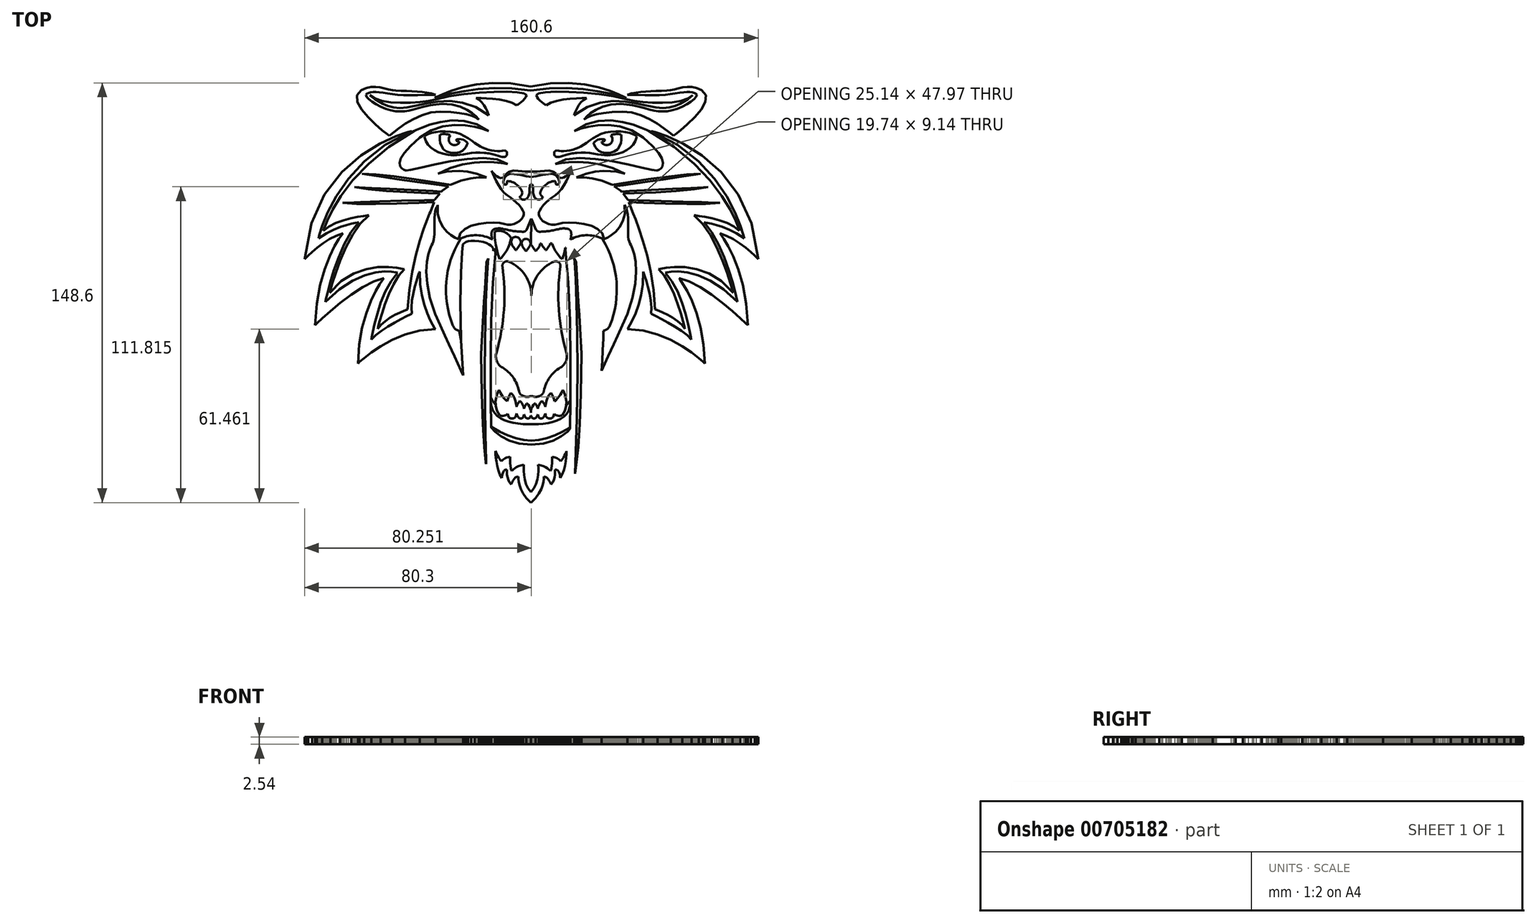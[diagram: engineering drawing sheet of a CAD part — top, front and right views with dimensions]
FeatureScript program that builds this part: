
annotation { "Feature Type Name" : "Feature", "Feature Type Description" : "" }
export const myFeature = defineFeature(function(context is Context, id is Id, definition is map)
    precondition{}
    {
        {
            var Q0;
            Q0=qCreatedBy(makeId("Top.planeOp"),FACE);
            var sketch = newSketch(context, id + "F0", { "sketchPlane" : qUnion([Q0])});
            skLineSegment(sketch, "E0", {"start": v(12.77, -75.29) * mm, "end": v(12.8, -74.69) * mm});
            skLineSegment(sketch, "E1", {"start": v(12.8, -74.69) * mm, "end": v(12.82, -74.1) * mm});
            skLineSegment(sketch, "E2", {"start": v(12.82, -74.1) * mm, "end": v(12.84, -73.5) * mm});
            skLineSegment(sketch, "E3", {"start": v(12.84, -73.5) * mm, "end": v(12.87, -72.9) * mm});
            skLineSegment(sketch, "E4", {"start": v(12.87, -72.9) * mm, "end": v(12.9, -72.3) * mm});
            skLineSegment(sketch, "E5", {"start": v(12.9, -72.3) * mm, "end": v(12.92, -71.7) * mm});
            skLineSegment(sketch, "E6", {"start": v(12.92, -71.7) * mm, "end": v(12.94, -71.1) * mm});
            skLineSegment(sketch, "E7", {"start": v(12.94, -71.1) * mm, "end": v(12.97, -70.5) * mm});
            skLineSegment(sketch, "E8", {"start": v(12.97, -70.5) * mm, "end": v(13.08, -67.74) * mm});
            skLineSegment(sketch, "E9", {"start": v(13.08, -67.74) * mm, "end": v(13.31, -60.6) * mm});
            skLineSegment(sketch, "E10", {"start": v(13.31, -60.6) * mm, "end": v(13.58, -50.1) * mm});
            skLineSegment(sketch, "E11", {"start": v(13.59, -50.63) * mm, "end": v(13.8, -37.88) * mm});
            skLineSegment(sketch, "E12", {"start": v(13.8, -37.88) * mm, "end": v(13.84, -23.18) * mm});
            skLineSegment(sketch, "E13", {"start": v(13.84, -23.18) * mm, "end": v(13.63, -8.86) * mm});
            skLineSegment(sketch, "E14", {"start": v(13.63, -8.86) * mm, "end": v(13.07, 4.68) * mm});
            skLineSegment(sketch, "E15", {"start": v(13.07, 4.68) * mm, "end": v(12.07, 16.37) * mm});
            skLineSegment(sketch, "E16", {"start": v(12.07, 16.37) * mm, "end": v(12.06, 16.4) * mm});
            skLineSegment(sketch, "E17", {"start": v(12.06, 16.4) * mm, "end": v(12.06, 16.43) * mm});
            skLineSegment(sketch, "E18", {"start": v(12.06, 16.43) * mm, "end": v(12.06, 16.46) * mm});
            skLineSegment(sketch, "E19", {"start": v(12.06, 16.46) * mm, "end": v(12.05, 16.49) * mm});
            skLineSegment(sketch, "E20", {"start": v(12.05, 16.49) * mm, "end": v(12.05, 16.52) * mm});
            skLineSegment(sketch, "E21", {"start": v(12.05, 16.52) * mm, "end": v(12.04, 16.54) * mm});
            skLineSegment(sketch, "E22", {"start": v(12.04, 16.54) * mm, "end": v(12.04, 16.57) * mm});
            skLineSegment(sketch, "E23", {"start": v(12.04, 16.57) * mm, "end": v(12.04, 16.6) * mm});
            skLineSegment(sketch, "E24", {"start": v(12.04, 16.6) * mm, "end": v(12.05, 16.63) * mm});
            skLineSegment(sketch, "E25", {"start": v(12.05, 16.63) * mm, "end": v(12.06, 16.66) * mm});
            skLineSegment(sketch, "E26", {"start": v(12.06, 16.66) * mm, "end": v(12.06, 16.69) * mm});
            skLineSegment(sketch, "E27", {"start": v(12.06, 16.69) * mm, "end": v(12.07, 16.71) * mm});
            skLineSegment(sketch, "E28", {"start": v(12.07, 16.71) * mm, "end": v(12.08, 16.74) * mm});
            skLineSegment(sketch, "E29", {"start": v(12.08, 16.74) * mm, "end": v(12.1, 16.77) * mm});
            skLineSegment(sketch, "E30", {"start": v(12.1, 16.77) * mm, "end": v(12.1, 16.8) * mm});
            skLineSegment(sketch, "E31", {"start": v(12.1, 16.8) * mm, "end": v(12.1, 16.82) * mm});
            skLineSegment(sketch, "E32", {"start": v(12.1, 16.82) * mm, "end": v(12.2, 17.03) * mm});
            skLineSegment(sketch, "E33", {"start": v(12.2, 17.03) * mm, "end": v(12.4, 17.4) * mm});
            skLineSegment(sketch, "E34", {"start": v(12.4, 17.4) * mm, "end": v(12.74, 17.88) * mm});
            skLineSegment(sketch, "E35", {"start": v(12.74, 17.88) * mm, "end": v(13.29, 18.43) * mm});
            skLineSegment(sketch, "E36", {"start": v(13.29, 18.43) * mm, "end": v(14.06, 19) * mm});
            skLineSegment(sketch, "E37", {"start": v(14.06, 19) * mm, "end": v(15.09, 19.54) * mm});
            skLineSegment(sketch, "E38", {"start": v(15.09, 19.54) * mm, "end": v(16.42, 20) * mm});
            skLineSegment(sketch, "E39", {"start": v(16.42, 20) * mm, "end": v(18.09, 20.35) * mm});
            skLineSegment(sketch, "E40", {"start": v(18.09, 20.35) * mm, "end": v(18.34, 20.38) * mm});
            skLineSegment(sketch, "E41", {"start": v(18.34, 20.38) * mm, "end": v(18.6, 20.41) * mm});
            skLineSegment(sketch, "E42", {"start": v(18.6, 20.41) * mm, "end": v(18.84, 20.44) * mm});
            skLineSegment(sketch, "E43", {"start": v(18.84, 20.44) * mm, "end": v(19.08, 20.46) * mm});
            skLineSegment(sketch, "E44", {"start": v(19.08, 20.46) * mm, "end": v(19.32, 20.47) * mm});
            skLineSegment(sketch, "E45", {"start": v(19.32, 20.47) * mm, "end": v(19.56, 20.49) * mm});
            skLineSegment(sketch, "E46", {"start": v(19.56, 20.49) * mm, "end": v(19.8, 20.5) * mm});
            skLineSegment(sketch, "E47", {"start": v(19.8, 20.5) * mm, "end": v(20.02, 20.5) * mm});
            skLineSegment(sketch, "E48", {"start": v(20.02, 20.5) * mm, "end": v(21.18, 20.43) * mm});
            skLineSegment(sketch, "E49", {"start": v(21.18, 20.43) * mm, "end": v(22.18, 20.25) * mm});
            skLineSegment(sketch, "E50", {"start": v(22.18, 20.25) * mm, "end": v(23.03, 19.98) * mm});
            skLineSegment(sketch, "E51", {"start": v(23.03, 19.98) * mm, "end": v(23.74, 19.63) * mm});
            skLineSegment(sketch, "E52", {"start": v(23.74, 19.63) * mm, "end": v(24.29, 19.24) * mm});
            skLineSegment(sketch, "E53", {"start": v(24.29, 19.24) * mm, "end": v(24.69, 18.83) * mm});
            skLineSegment(sketch, "E54", {"start": v(24.69, 18.83) * mm, "end": v(24.94, 18.42) * mm});
            skLineSegment(sketch, "E55", {"start": v(24.94, 18.42) * mm, "end": v(25.04, 18.02) * mm});
            skLineSegment(sketch, "E56", {"start": v(25.04, 18.02) * mm, "end": v(25.1, 17.3) * mm});
            skLineSegment(sketch, "E57", {"start": v(25.1, 17.3) * mm, "end": v(25.24, 15.31) * mm});
            skLineSegment(sketch, "E58", {"start": v(25.24, 15.31) * mm, "end": v(25.42, 12.2) * mm});
            skLineSegment(sketch, "E59", {"start": v(25.42, 12.2) * mm, "end": v(25.6, 8.12) * mm});
            skLineSegment(sketch, "E60", {"start": v(25.6, 8.12) * mm, "end": v(25.76, 3.17) * mm});
            skLineSegment(sketch, "E61", {"start": v(25.51, 3.31) * mm, "end": v(25.6, -2.35) * mm});
            skLineSegment(sketch, "E62", {"start": v(25.6, -2.35) * mm, "end": v(25.6, -8.6) * mm});
            skLineSegment(sketch, "E63", {"start": v(25.6, -8.6) * mm, "end": v(25.45, -15.3) * mm});
            skLineSegment(sketch, "E64", {"start": v(25.45, -15.3) * mm, "end": v(25.3, -19.29) * mm});
            skLineSegment(sketch, "E65", {"start": v(25.3, -19.29) * mm, "end": v(25.08, -23.2) * mm});
            skLineSegment(sketch, "E66", {"start": v(25.08, -23.2) * mm, "end": v(24.81, -27) * mm});
            skLineSegment(sketch, "E67", {"start": v(25.06, -27.14) * mm, "end": v(24.74, -30.85) * mm});
            skLineSegment(sketch, "E68", {"start": v(24.74, -30.85) * mm, "end": v(24.37, -34.46) * mm});
            skLineSegment(sketch, "E69", {"start": v(24.37, -34.46) * mm, "end": v(23.95, -37.96) * mm});
            skLineSegment(sketch, "E70", {"start": v(23.95, -37.96) * mm, "end": v(23.48, -41.35) * mm});
            skLineSegment(sketch, "E71", {"start": v(23.48, -41.35) * mm, "end": v(22.96, -44.63) * mm});
            skLineSegment(sketch, "E72", {"start": v(22.96, -44.63) * mm, "end": v(22.24, -48.58) * mm});
            skLineSegment(sketch, "E73", {"start": v(22.24, -48.58) * mm, "end": v(21.43, -52.36) * mm});
            skLineSegment(sketch, "E74", {"start": v(21.43, -52.36) * mm, "end": v(20.54, -55.95) * mm});
            skLineSegment(sketch, "E75", {"start": v(20.54, -55.95) * mm, "end": v(19.58, -59.35) * mm});
            skLineSegment(sketch, "E76", {"start": v(19.58, -59.35) * mm, "end": v(18.54, -62.56) * mm});
            skLineSegment(sketch, "E77", {"start": v(18.54, -62.56) * mm, "end": v(17.42, -65.58) * mm});
            skLineSegment(sketch, "E78", {"start": v(17.42, -65.58) * mm, "end": v(16.23, -68.4) * mm});
            skLineSegment(sketch, "E79", {"start": v(16.23, -68.4) * mm, "end": v(14.96, -71.03) * mm});
            skLineSegment(sketch, "E80", {"start": v(14.96, -71.03) * mm, "end": v(14.69, -71.56) * mm});
            skLineSegment(sketch, "E81", {"start": v(14.69, -71.56) * mm, "end": v(14.41, -72.1) * mm});
            skLineSegment(sketch, "E82", {"start": v(14.41, -72.1) * mm, "end": v(14.14, -72.63) * mm});
            skLineSegment(sketch, "E83", {"start": v(14.14, -72.63) * mm, "end": v(13.87, -73.16) * mm});
            skLineSegment(sketch, "E84", {"start": v(13.87, -73.16) * mm, "end": v(13.6, -73.7) * mm});
            skLineSegment(sketch, "E85", {"start": v(13.6, -73.7) * mm, "end": v(13.32, -74.22) * mm});
            skLineSegment(sketch, "E86", {"start": v(13.32, -74.22) * mm, "end": v(13.04, -74.76) * mm});
            skLineSegment(sketch, "E87", {"start": v(13.04, -74.76) * mm, "end": v(12.77, -75.29) * mm});
            skLineSegment(sketch, "E88", {"start": v(14.2, 16.3) * mm, "end": v(15.05, 6.8) * mm});
            skLineSegment(sketch, "E89", {"start": v(15.05, 6.8) * mm, "end": v(15.6, -4.05) * mm});
            skLineSegment(sketch, "E90", {"start": v(15.6, -4.05) * mm, "end": v(15.88, -15.66) * mm});
            skLineSegment(sketch, "E91", {"start": v(15.88, -15.66) * mm, "end": v(15.96, -27.46) * mm});
            skLineSegment(sketch, "E92", {"start": v(15.96, -27.46) * mm, "end": v(15.88, -38.9) * mm});
            skLineSegment(sketch, "E93", {"start": v(15.88, -38.9) * mm, "end": v(15.71, -49.38) * mm});
            skLineSegment(sketch, "E94", {"start": v(15.71, -49.38) * mm, "end": v(15.5, -58.35) * mm});
            skLineSegment(sketch, "E95", {"start": v(15.5, -58.35) * mm, "end": v(15.28, -65.25) * mm});
            skLineSegment(sketch, "E96", {"start": v(15.28, -65.25) * mm, "end": v(16.97, -60.57) * mm});
            skLineSegment(sketch, "E97", {"start": v(16.97, -60.57) * mm, "end": v(18.48, -55.42) * mm});
            skLineSegment(sketch, "E98", {"start": v(18.48, -55.42) * mm, "end": v(19.81, -49.8) * mm});
            skLineSegment(sketch, "E99", {"start": v(19.81, -49.8) * mm, "end": v(20.95, -43.74) * mm});
            skLineSegment(sketch, "E100", {"start": v(20.95, -43.74) * mm, "end": v(21.9, -37.25) * mm});
            skLineSegment(sketch, "E101", {"start": v(21.9, -37.25) * mm, "end": v(22.66, -30.35) * mm});
            skLineSegment(sketch, "E102", {"start": v(22.66, -30.35) * mm, "end": v(23.22, -23.04) * mm});
            skLineSegment(sketch, "E103", {"start": v(23.22, -23.04) * mm, "end": v(23.58, -15.36) * mm});
            skLineSegment(sketch, "E104", {"start": v(23.58, -15.36) * mm, "end": v(23.73, -9.17) * mm});
            skLineSegment(sketch, "E105", {"start": v(23.73, -9.17) * mm, "end": v(23.75, -3.37) * mm});
            skLineSegment(sketch, "E106", {"start": v(23.75, -3.37) * mm, "end": v(23.68, 1.96) * mm});
            skLineSegment(sketch, "E107", {"start": v(23.68, 1.96) * mm, "end": v(23.54, 6.7) * mm});
            skLineSegment(sketch, "E108", {"start": v(23.54, 6.7) * mm, "end": v(23.37, 10.73) * mm});
            skLineSegment(sketch, "E109", {"start": v(23.37, 10.73) * mm, "end": v(23.2, 13.96) * mm});
            skLineSegment(sketch, "E110", {"start": v(23.2, 13.96) * mm, "end": v(23.05, 16.29) * mm});
            skLineSegment(sketch, "E111", {"start": v(23.05, 16.29) * mm, "end": v(22.96, 17.6) * mm});
            skLineSegment(sketch, "E112", {"start": v(22.96, 17.6) * mm, "end": v(22.84, 17.7) * mm});
            skLineSegment(sketch, "E113", {"start": v(22.84, 17.7) * mm, "end": v(22.67, 17.8) * mm});
            skLineSegment(sketch, "E114", {"start": v(22.67, 17.8) * mm, "end": v(22.43, 17.94) * mm});
            skLineSegment(sketch, "E115", {"start": v(22.43, 17.94) * mm, "end": v(22.11, 18.07) * mm});
            skLineSegment(sketch, "E116", {"start": v(22.11, 18.07) * mm, "end": v(21.72, 18.19) * mm});
            skLineSegment(sketch, "E117", {"start": v(21.72, 18.19) * mm, "end": v(21.25, 18.29) * mm});
            skLineSegment(sketch, "E118", {"start": v(21.25, 18.29) * mm, "end": v(20.68, 18.36) * mm});
            skLineSegment(sketch, "E119", {"start": v(20.68, 18.36) * mm, "end": v(20.02, 18.38) * mm});
            skLineSegment(sketch, "E120", {"start": v(20.02, 18.38) * mm, "end": v(19.83, 18.38) * mm});
            skLineSegment(sketch, "E121", {"start": v(19.83, 18.38) * mm, "end": v(19.63, 18.37) * mm});
            skLineSegment(sketch, "E122", {"start": v(19.63, 18.37) * mm, "end": v(19.43, 18.36) * mm});
            skLineSegment(sketch, "E123", {"start": v(19.43, 18.36) * mm, "end": v(19.23, 18.35) * mm});
            skLineSegment(sketch, "E124", {"start": v(19.23, 18.35) * mm, "end": v(19.02, 18.33) * mm});
            skLineSegment(sketch, "E125", {"start": v(19.02, 18.33) * mm, "end": v(18.81, 18.31) * mm});
            skLineSegment(sketch, "E126", {"start": v(18.81, 18.31) * mm, "end": v(18.6, 18.29) * mm});
            skLineSegment(sketch, "E127", {"start": v(18.6, 18.29) * mm, "end": v(18.38, 18.26) * mm});
            skLineSegment(sketch, "E128", {"start": v(18.38, 18.26) * mm, "end": v(17.38, 18.07) * mm});
            skLineSegment(sketch, "E129", {"start": v(17.38, 18.07) * mm, "end": v(16.55, 17.84) * mm});
            skLineSegment(sketch, "E130", {"start": v(16.55, 17.84) * mm, "end": v(15.86, 17.57) * mm});
            skLineSegment(sketch, "E131", {"start": v(15.86, 17.57) * mm, "end": v(15.31, 17.28) * mm});
            skLineSegment(sketch, "E132", {"start": v(15.31, 17.28) * mm, "end": v(14.88, 17) * mm});
            skLineSegment(sketch, "E133", {"start": v(14.88, 17) * mm, "end": v(14.57, 16.73) * mm});
            skLineSegment(sketch, "E134", {"start": v(14.57, 16.73) * mm, "end": v(14.34, 16.5) * mm});
            skLineSegment(sketch, "E135", {"start": v(14.34, 16.5) * mm, "end": v(14.2, 16.3) * mm});
            skLineSegment(sketch, "E136", {"start": v(-16.27, -43.5) * mm, "end": v(-16.09, -43.9) * mm});
            skLineSegment(sketch, "E137", {"start": v(-16.09, -43.9) * mm, "end": v(-15.49, -44.96) * mm});
            skLineSegment(sketch, "E138", {"start": v(-15.49, -44.96) * mm, "end": v(-14.42, -46.45) * mm});
            skLineSegment(sketch, "E139", {"start": v(-14.42, -46.45) * mm, "end": v(-12.83, -48.16) * mm});
            skLineSegment(sketch, "E140", {"start": v(-12.83, -48.16) * mm, "end": v(-10.66, -49.87) * mm});
            skLineSegment(sketch, "E141", {"start": v(-10.66, -49.87) * mm, "end": v(-7.84, -51.36) * mm});
            skLineSegment(sketch, "E142", {"start": v(-7.84, -51.36) * mm, "end": v(-4.32, -52.41) * mm});
            skLineSegment(sketch, "E143", {"start": v(-4.32, -52.41) * mm, "end": v(-0.05, -52.81) * mm});
            skLineSegment(sketch, "E144", {"start": v(-0.05, -52.81) * mm, "end": v(4.23, -52.41) * mm});
            skLineSegment(sketch, "E145", {"start": v(4.23, -52.41) * mm, "end": v(7.74, -51.36) * mm});
            skLineSegment(sketch, "E146", {"start": v(7.74, -51.36) * mm, "end": v(10.56, -49.87) * mm});
            skLineSegment(sketch, "E147", {"start": v(10.56, -49.87) * mm, "end": v(12.74, -48.16) * mm});
            skLineSegment(sketch, "E148", {"start": v(12.74, -48.16) * mm, "end": v(14.33, -46.45) * mm});
            skLineSegment(sketch, "E149", {"start": v(14.33, -46.45) * mm, "end": v(15.4, -44.96) * mm});
            skLineSegment(sketch, "E150", {"start": v(15.4, -44.96) * mm, "end": v(15.99, -43.9) * mm});
            skLineSegment(sketch, "E151", {"start": v(15.99, -43.9) * mm, "end": v(16.17, -43.5) * mm});
            skLineSegment(sketch, "E152", {"start": v(-13.36, -75.29) * mm, "end": v(-13.64, -74.76) * mm});
            skLineSegment(sketch, "E153", {"start": v(-13.64, -74.76) * mm, "end": v(-13.9, -74.22) * mm});
            skLineSegment(sketch, "E154", {"start": v(-13.9, -74.22) * mm, "end": v(-14.18, -73.7) * mm});
            skLineSegment(sketch, "E155", {"start": v(-14.18, -73.7) * mm, "end": v(-14.46, -73.16) * mm});
            skLineSegment(sketch, "E156", {"start": v(-14.46, -73.16) * mm, "end": v(-14.73, -72.63) * mm});
            skLineSegment(sketch, "E157", {"start": v(-14.73, -72.63) * mm, "end": v(-15, -72.1) * mm});
            skLineSegment(sketch, "E158", {"start": v(-15, -72.1) * mm, "end": v(-15.28, -71.56) * mm});
            skLineSegment(sketch, "E159", {"start": v(-15.28, -71.56) * mm, "end": v(-15.56, -71.03) * mm});
            skLineSegment(sketch, "E160", {"start": v(-15.56, -71.03) * mm, "end": v(-16.83, -68.4) * mm});
            skLineSegment(sketch, "E161", {"start": v(-16.83, -68.4) * mm, "end": v(-18.02, -65.58) * mm});
            skLineSegment(sketch, "E162", {"start": v(-18.02, -65.58) * mm, "end": v(-19.13, -62.56) * mm});
            skLineSegment(sketch, "E163", {"start": v(-19.13, -62.56) * mm, "end": v(-20.18, -59.35) * mm});
            skLineSegment(sketch, "E164", {"start": v(-20.18, -59.35) * mm, "end": v(-21.14, -55.95) * mm});
            skLineSegment(sketch, "E165", {"start": v(-21.14, -55.95) * mm, "end": v(-22.02, -52.36) * mm});
            skLineSegment(sketch, "E166", {"start": v(-22.02, -52.36) * mm, "end": v(-22.83, -48.58) * mm});
            skLineSegment(sketch, "E167", {"start": v(-22.83, -48.58) * mm, "end": v(-23.56, -44.63) * mm});
            skLineSegment(sketch, "E168", {"start": v(-23.56, -44.63) * mm, "end": v(-24.08, -41.35) * mm});
            skLineSegment(sketch, "E169", {"start": v(-24.08, -41.35) * mm, "end": v(-24.55, -37.96) * mm});
            skLineSegment(sketch, "E170", {"start": v(-24.55, -37.96) * mm, "end": v(-24.97, -34.46) * mm});
            skLineSegment(sketch, "E171", {"start": v(-24.97, -34.46) * mm, "end": v(-25.34, -30.85) * mm});
            skLineSegment(sketch, "E172", {"start": v(-25.34, -30.85) * mm, "end": v(-25.65, -27.14) * mm});
            skLineSegment(sketch, "E173", {"start": v(-25.65, -27.14) * mm, "end": v(-25.92, -23.33) * mm});
            skLineSegment(sketch, "E174", {"start": v(-25.92, -23.33) * mm, "end": v(-26.13, -19.43) * mm});
            skLineSegment(sketch, "E175", {"start": v(-26.13, -19.43) * mm, "end": v(-26.3, -15.43) * mm});
            skLineSegment(sketch, "E176", {"start": v(-24.88, -16.29) * mm, "end": v(-26.15, -8.6) * mm});
            skLineSegment(sketch, "E177", {"start": v(-26.44, -8.74) * mm, "end": v(-26.45, -2.49) * mm});
            skLineSegment(sketch, "E178", {"start": v(-26.45, -2.49) * mm, "end": v(-26.35, 3.17) * mm});
            skLineSegment(sketch, "E179", {"start": v(-26.35, 3.17) * mm, "end": v(-26.2, 8.12) * mm});
            skLineSegment(sketch, "E180", {"start": v(-26.2, 8.12) * mm, "end": v(-26, 12.21) * mm});
            skLineSegment(sketch, "E181", {"start": v(-26, 12.21) * mm, "end": v(-25.83, 15.32) * mm});
            skLineSegment(sketch, "E182", {"start": v(-25.83, 15.32) * mm, "end": v(-25.7, 17.3) * mm});
            skLineSegment(sketch, "E183", {"start": v(-25.7, 17.3) * mm, "end": v(-25.64, 18.03) * mm});
            skLineSegment(sketch, "E184", {"start": v(-25.64, 18.03) * mm, "end": v(-25.53, 18.42) * mm});
            skLineSegment(sketch, "E185", {"start": v(-25.53, 18.42) * mm, "end": v(-25.28, 18.83) * mm});
            skLineSegment(sketch, "E186", {"start": v(-25.28, 18.83) * mm, "end": v(-24.88, 19.24) * mm});
            skLineSegment(sketch, "E187", {"start": v(-24.88, 19.24) * mm, "end": v(-24.33, 19.63) * mm});
            skLineSegment(sketch, "E188", {"start": v(-24.33, 19.63) * mm, "end": v(-23.63, 19.98) * mm});
            skLineSegment(sketch, "E189", {"start": v(-23.63, 19.98) * mm, "end": v(-22.78, 20.25) * mm});
            skLineSegment(sketch, "E190", {"start": v(-22.78, 20.25) * mm, "end": v(-21.77, 20.43) * mm});
            skLineSegment(sketch, "E191", {"start": v(-21.77, 20.43) * mm, "end": v(-20.62, 20.5) * mm});
            skLineSegment(sketch, "E192", {"start": v(-20.62, 20.5) * mm, "end": v(-20.39, 20.5) * mm});
            skLineSegment(sketch, "E193", {"start": v(-20.39, 20.5) * mm, "end": v(-20.15, 20.49) * mm});
            skLineSegment(sketch, "E194", {"start": v(-20.15, 20.49) * mm, "end": v(-19.92, 20.47) * mm});
            skLineSegment(sketch, "E195", {"start": v(-19.92, 20.47) * mm, "end": v(-19.68, 20.46) * mm});
            skLineSegment(sketch, "E196", {"start": v(-19.68, 20.46) * mm, "end": v(-19.43, 20.44) * mm});
            skLineSegment(sketch, "E197", {"start": v(-19.43, 20.44) * mm, "end": v(-19.18, 20.41) * mm});
            skLineSegment(sketch, "E198", {"start": v(-19.18, 20.41) * mm, "end": v(-18.93, 20.38) * mm});
            skLineSegment(sketch, "E199", {"start": v(-18.93, 20.38) * mm, "end": v(-18.68, 20.35) * mm});
            skLineSegment(sketch, "E200", {"start": v(-18.68, 20.35) * mm, "end": v(-17.02, 20) * mm});
            skLineSegment(sketch, "E201", {"start": v(-17.02, 20) * mm, "end": v(-15.68, 19.54) * mm});
            skLineSegment(sketch, "E202", {"start": v(-15.68, 19.54) * mm, "end": v(-14.65, 19) * mm});
            skLineSegment(sketch, "E203", {"start": v(-14.65, 19) * mm, "end": v(-13.88, 18.43) * mm});
            skLineSegment(sketch, "E204", {"start": v(-13.88, 18.43) * mm, "end": v(-13.34, 17.88) * mm});
            skLineSegment(sketch, "E205", {"start": v(-13.34, 17.88) * mm, "end": v(-12.99, 17.4) * mm});
            skLineSegment(sketch, "E206", {"start": v(-12.99, 17.4) * mm, "end": v(-12.79, 17.03) * mm});
            skLineSegment(sketch, "E207", {"start": v(-12.79, 17.03) * mm, "end": v(-12.7, 16.82) * mm});
            skLineSegment(sketch, "E208", {"start": v(-12.7, 16.82) * mm, "end": v(-12.7, 16.8) * mm});
            skLineSegment(sketch, "E209", {"start": v(-12.7, 16.8) * mm, "end": v(-12.69, 16.77) * mm});
            skLineSegment(sketch, "E210", {"start": v(-12.69, 16.77) * mm, "end": v(-12.68, 16.74) * mm});
            skLineSegment(sketch, "E211", {"start": v(-12.68, 16.74) * mm, "end": v(-12.67, 16.71) * mm});
            skLineSegment(sketch, "E212", {"start": v(-12.67, 16.71) * mm, "end": v(-12.66, 16.69) * mm});
            skLineSegment(sketch, "E213", {"start": v(-12.66, 16.69) * mm, "end": v(-12.65, 16.66) * mm});
            skLineSegment(sketch, "E214", {"start": v(-12.65, 16.66) * mm, "end": v(-12.64, 16.63) * mm});
            skLineSegment(sketch, "E215", {"start": v(-12.64, 16.63) * mm, "end": v(-12.63, 16.6) * mm});
            skLineSegment(sketch, "E216", {"start": v(-12.63, 16.6) * mm, "end": v(-12.64, 16.57) * mm});
            skLineSegment(sketch, "E217", {"start": v(-12.64, 16.57) * mm, "end": v(-12.64, 16.54) * mm});
            skLineSegment(sketch, "E218", {"start": v(-12.64, 16.54) * mm, "end": v(-12.64, 16.52) * mm});
            skLineSegment(sketch, "E219", {"start": v(-12.64, 16.52) * mm, "end": v(-12.65, 16.49) * mm});
            skLineSegment(sketch, "E220", {"start": v(-12.65, 16.49) * mm, "end": v(-12.65, 16.46) * mm});
            skLineSegment(sketch, "E221", {"start": v(-12.65, 16.46) * mm, "end": v(-12.65, 16.43) * mm});
            skLineSegment(sketch, "E222", {"start": v(-12.65, 16.43) * mm, "end": v(-12.66, 16.4) * mm});
            skLineSegment(sketch, "E223", {"start": v(-12.66, 16.4) * mm, "end": v(-12.66, 16.37) * mm});
            skLineSegment(sketch, "E224", {"start": v(-12.66, 16.37) * mm, "end": v(-13.67, 4.68) * mm});
            skLineSegment(sketch, "E225", {"start": v(-13.67, 4.68) * mm, "end": v(-14.22, -8.86) * mm});
            skLineSegment(sketch, "E226", {"start": v(-14.22, -8.86) * mm, "end": v(-14.43, -23.18) * mm});
            skLineSegment(sketch, "E227", {"start": v(-14.43, -23.18) * mm, "end": v(-14.38, -37.28) * mm});
            skLineSegment(sketch, "E228", {"start": v(-14.38, -37.28) * mm, "end": v(-14.18, -50.1) * mm});
            skLineSegment(sketch, "E229", {"start": v(-14.18, -50.1) * mm, "end": v(-13.9, -60.6) * mm});
            skLineSegment(sketch, "E230", {"start": v(-13.9, -60.6) * mm, "end": v(-13.67, -67.74) * mm});
            skLineSegment(sketch, "E231", {"start": v(-13.67, -67.74) * mm, "end": v(-13.56, -70.5) * mm});
            skLineSegment(sketch, "E232", {"start": v(-13.56, -70.5) * mm, "end": v(-13.54, -71.1) * mm});
            skLineSegment(sketch, "E233", {"start": v(-13.54, -71.1) * mm, "end": v(-13.51, -71.7) * mm});
            skLineSegment(sketch, "E234", {"start": v(-13.51, -71.7) * mm, "end": v(-13.49, -72.3) * mm});
            skLineSegment(sketch, "E235", {"start": v(-13.49, -72.3) * mm, "end": v(-13.46, -72.9) * mm});
            skLineSegment(sketch, "E236", {"start": v(-13.46, -72.9) * mm, "end": v(-13.44, -73.5) * mm});
            skLineSegment(sketch, "E237", {"start": v(-13.44, -73.5) * mm, "end": v(-13.41, -74.1) * mm});
            skLineSegment(sketch, "E238", {"start": v(-13.41, -74.1) * mm, "end": v(-13.39, -74.69) * mm});
            skLineSegment(sketch, "E239", {"start": v(-13.39, -74.69) * mm, "end": v(-13.36, -75.29) * mm});
            skLineSegment(sketch, "E240", {"start": v(-23.55, 17.6) * mm, "end": v(-23.65, 16.28) * mm});
            skLineSegment(sketch, "E241", {"start": v(-23.65, 16.28) * mm, "end": v(-23.8, 13.95) * mm});
            skLineSegment(sketch, "E242", {"start": v(-23.8, 13.95) * mm, "end": v(-23.97, 10.71) * mm});
            skLineSegment(sketch, "E243", {"start": v(-23.97, 10.71) * mm, "end": v(-24.14, 6.67) * mm});
            skLineSegment(sketch, "E244", {"start": v(-24.14, 6.67) * mm, "end": v(-24.27, 1.94) * mm});
            skLineSegment(sketch, "E245", {"start": v(-24.27, 1.94) * mm, "end": v(-24.34, -3.4) * mm});
            skLineSegment(sketch, "E246", {"start": v(-24.34, -3.4) * mm, "end": v(-24.32, -9.2) * mm});
            skLineSegment(sketch, "E247", {"start": v(-24.32, -9.2) * mm, "end": v(-24.18, -15.39) * mm});
            skLineSegment(sketch, "E248", {"start": v(-24.18, -15.39) * mm, "end": v(-23.82, -23.06) * mm});
            skLineSegment(sketch, "E249", {"start": v(-23.82, -23.06) * mm, "end": v(-23.26, -30.36) * mm});
            skLineSegment(sketch, "E250", {"start": v(-23.26, -30.36) * mm, "end": v(-22.5, -37.26) * mm});
            skLineSegment(sketch, "E251", {"start": v(-22.5, -37.26) * mm, "end": v(-21.55, -43.75) * mm});
            skLineSegment(sketch, "E252", {"start": v(-21.55, -43.75) * mm, "end": v(-20.4, -49.8) * mm});
            skLineSegment(sketch, "E253", {"start": v(-20.4, -49.8) * mm, "end": v(-19.08, -55.42) * mm});
            skLineSegment(sketch, "E254", {"start": v(-19.08, -55.42) * mm, "end": v(-17.57, -60.57) * mm});
            skLineSegment(sketch, "E255", {"start": v(-17.57, -60.57) * mm, "end": v(-15.87, -65.25) * mm});
            skLineSegment(sketch, "E256", {"start": v(-15.87, -65.25) * mm, "end": v(-16.08, -58.35) * mm});
            skLineSegment(sketch, "E257", {"start": v(-16.08, -58.35) * mm, "end": v(-16.3, -49.38) * mm});
            skLineSegment(sketch, "E258", {"start": v(-16.3, -49.38) * mm, "end": v(-16.48, -38.9) * mm});
            skLineSegment(sketch, "E259", {"start": v(-16.48, -38.9) * mm, "end": v(-16.55, -27.46) * mm});
            skLineSegment(sketch, "E260", {"start": v(-16.55, -27.46) * mm, "end": v(-16.47, -15.66) * mm});
            skLineSegment(sketch, "E261", {"start": v(-16.47, -15.66) * mm, "end": v(-16.19, -4.05) * mm});
            skLineSegment(sketch, "E262", {"start": v(-16.19, -4.05) * mm, "end": v(-15.65, 6.8) * mm});
            skLineSegment(sketch, "E263", {"start": v(-15.65, 6.8) * mm, "end": v(-14.8, 16.3) * mm});
            skLineSegment(sketch, "E264", {"start": v(-14.8, 16.3) * mm, "end": v(-14.94, 16.5) * mm});
            skLineSegment(sketch, "E265", {"start": v(-14.94, 16.5) * mm, "end": v(-15.16, 16.73) * mm});
            skLineSegment(sketch, "E266", {"start": v(-15.16, 16.73) * mm, "end": v(-15.48, 17) * mm});
            skLineSegment(sketch, "E267", {"start": v(-15.48, 17) * mm, "end": v(-15.9, 17.28) * mm});
            skLineSegment(sketch, "E268", {"start": v(-15.9, 17.28) * mm, "end": v(-16.46, 17.57) * mm});
            skLineSegment(sketch, "E269", {"start": v(-16.46, 17.57) * mm, "end": v(-17.14, 17.84) * mm});
            skLineSegment(sketch, "E270", {"start": v(-17.14, 17.84) * mm, "end": v(-17.98, 18.07) * mm});
            skLineSegment(sketch, "E271", {"start": v(-17.98, 18.07) * mm, "end": v(-18.98, 18.26) * mm});
            skLineSegment(sketch, "E272", {"start": v(-18.98, 18.26) * mm, "end": v(-19.2, 18.29) * mm});
            skLineSegment(sketch, "E273", {"start": v(-19.2, 18.29) * mm, "end": v(-19.4, 18.31) * mm});
            skLineSegment(sketch, "E274", {"start": v(-19.4, 18.31) * mm, "end": v(-19.62, 18.33) * mm});
            skLineSegment(sketch, "E275", {"start": v(-19.62, 18.33) * mm, "end": v(-19.82, 18.35) * mm});
            skLineSegment(sketch, "E276", {"start": v(-19.82, 18.35) * mm, "end": v(-20.03, 18.36) * mm});
            skLineSegment(sketch, "E277", {"start": v(-20.03, 18.36) * mm, "end": v(-20.23, 18.37) * mm});
            skLineSegment(sketch, "E278", {"start": v(-20.23, 18.37) * mm, "end": v(-20.42, 18.38) * mm});
            skLineSegment(sketch, "E279", {"start": v(-20.42, 18.38) * mm, "end": v(-20.62, 18.38) * mm});
            skLineSegment(sketch, "E280", {"start": v(-20.62, 18.38) * mm, "end": v(-21.28, 18.36) * mm});
            skLineSegment(sketch, "E281", {"start": v(-21.28, 18.36) * mm, "end": v(-21.84, 18.29) * mm});
            skLineSegment(sketch, "E282", {"start": v(-21.84, 18.29) * mm, "end": v(-22.32, 18.19) * mm});
            skLineSegment(sketch, "E283", {"start": v(-22.32, 18.19) * mm, "end": v(-22.7, 18.07) * mm});
            skLineSegment(sketch, "E284", {"start": v(-22.7, 18.07) * mm, "end": v(-23.02, 17.94) * mm});
            skLineSegment(sketch, "E285", {"start": v(-23.02, 17.94) * mm, "end": v(-23.26, 17.8) * mm});
            skLineSegment(sketch, "E286", {"start": v(-23.26, 17.8) * mm, "end": v(-23.43, 17.7) * mm});
            skLineSegment(sketch, "E287", {"start": v(-23.43, 17.7) * mm, "end": v(-23.55, 17.6) * mm});
            skLineSegment(sketch, "E288", {"start": v(-0.05, 43.85) * mm, "end": v(-0.03, 43.85) * mm});
            skLineSegment(sketch, "E289", {"start": v(-0.03, 43.85) * mm, "end": v(0.06, 43.84) * mm});
            skLineSegment(sketch, "E290", {"start": v(0.06, 43.84) * mm, "end": v(0.27, 43.84) * mm});
            skLineSegment(sketch, "E291", {"start": v(0.27, 43.84) * mm, "end": v(0.64, 43.86) * mm});
            skLineSegment(sketch, "E292", {"start": v(0.64, 43.86) * mm, "end": v(1.22, 43.89) * mm});
            skLineSegment(sketch, "E293", {"start": v(1.22, 43.89) * mm, "end": v(2.06, 43.95) * mm});
            skLineSegment(sketch, "E294", {"start": v(2.06, 43.95) * mm, "end": v(3.2, 44.04) * mm});
            skLineSegment(sketch, "E295", {"start": v(3.2, 44.04) * mm, "end": v(4.68, 44.17) * mm});
            skLineSegment(sketch, "E296", {"start": v(4.68, 44.17) * mm, "end": v(6.13, 44.22) * mm});
            skLineSegment(sketch, "E297", {"start": v(6.13, 44.22) * mm, "end": v(7.18, 44.08) * mm});
            skLineSegment(sketch, "E298", {"start": v(7.18, 44.08) * mm, "end": v(7.92, 43.8) * mm});
            skLineSegment(sketch, "E299", {"start": v(7.92, 43.8) * mm, "end": v(8.44, 43.4) * mm});
            skLineSegment(sketch, "E300", {"start": v(8.44, 43.4) * mm, "end": v(8.84, 42.97) * mm});
            skLineSegment(sketch, "E301", {"start": v(8.84, 42.97) * mm, "end": v(9.2, 42.52) * mm});
            skLineSegment(sketch, "E302", {"start": v(9.2, 42.52) * mm, "end": v(9.6, 42.1) * mm});
            skLineSegment(sketch, "E303", {"start": v(9.6, 42.1) * mm, "end": v(10.15, 41.77) * mm});
            skLineSegment(sketch, "E304", {"start": v(10.15, 41.77) * mm, "end": v(10.82, 41.66) * mm});
            skLineSegment(sketch, "E305", {"start": v(10.82, 41.66) * mm, "end": v(11.5, 41.83) * mm});
            skLineSegment(sketch, "E306", {"start": v(11.5, 41.83) * mm, "end": v(12.14, 42.2) * mm});
            skLineSegment(sketch, "E307", {"start": v(12.14, 42.2) * mm, "end": v(12.74, 42.7) * mm});
            skLineSegment(sketch, "E308", {"start": v(12.74, 42.7) * mm, "end": v(13.26, 43.22) * mm});
            skLineSegment(sketch, "E309", {"start": v(13.26, 43.22) * mm, "end": v(13.66, 43.7) * mm});
            skLineSegment(sketch, "E310", {"start": v(13.66, 43.7) * mm, "end": v(13.93, 44.04) * mm});
            skLineSegment(sketch, "E311", {"start": v(13.93, 44.04) * mm, "end": v(14.02, 44.17) * mm});
            skLineSegment(sketch, "E312", {"start": v(14.02, 44.17) * mm, "end": v(13.9, 43.88) * mm});
            skLineSegment(sketch, "E313", {"start": v(13.9, 43.88) * mm, "end": v(13.57, 43.1) * mm});
            skLineSegment(sketch, "E314", {"start": v(13.57, 43.1) * mm, "end": v(13.05, 41.94) * mm});
            skLineSegment(sketch, "E315", {"start": v(13.05, 41.94) * mm, "end": v(12.36, 40.57) * mm});
            skLineSegment(sketch, "E316", {"start": v(12.36, 40.57) * mm, "end": v(11.53, 39.1) * mm});
            skLineSegment(sketch, "E317", {"start": v(11.53, 39.1) * mm, "end": v(10.58, 37.67) * mm});
            skLineSegment(sketch, "E318", {"start": v(10.58, 37.67) * mm, "end": v(9.55, 36.42) * mm});
            skLineSegment(sketch, "E319", {"start": v(9.55, 36.42) * mm, "end": v(8.45, 35.47) * mm});
            skLineSegment(sketch, "E320", {"start": v(8.45, 35.47) * mm, "end": v(7.33, 34.69) * mm});
            skLineSegment(sketch, "E321", {"start": v(7.33, 34.69) * mm, "end": v(6.24, 33.84) * mm});
            skLineSegment(sketch, "E322", {"start": v(6.24, 33.84) * mm, "end": v(5.21, 32.94) * mm});
            skLineSegment(sketch, "E323", {"start": v(5.21, 32.94) * mm, "end": v(4.3, 32.03) * mm});
            skLineSegment(sketch, "E324", {"start": v(4.3, 32.03) * mm, "end": v(3.53, 31.12) * mm});
            skLineSegment(sketch, "E325", {"start": v(3.53, 31.12) * mm, "end": v(2.97, 30.23) * mm});
            skLineSegment(sketch, "E326", {"start": v(2.97, 30.23) * mm, "end": v(2.64, 29.38) * mm});
            skLineSegment(sketch, "E327", {"start": v(2.64, 29.38) * mm, "end": v(2.6, 28.6) * mm});
            skLineSegment(sketch, "E328", {"start": v(2.6, 28.6) * mm, "end": v(2.86, 27.84) * mm});
            skLineSegment(sketch, "E329", {"start": v(2.86, 27.84) * mm, "end": v(3.37, 27.1) * mm});
            skLineSegment(sketch, "E330", {"start": v(3.37, 27.1) * mm, "end": v(4.1, 26.42) * mm});
            skLineSegment(sketch, "E331", {"start": v(4.1, 26.42) * mm, "end": v(5, 25.84) * mm});
            skLineSegment(sketch, "E332", {"start": v(5, 25.84) * mm, "end": v(6.02, 25.4) * mm});
            skLineSegment(sketch, "E333", {"start": v(6.02, 25.4) * mm, "end": v(7.14, 25.15) * mm});
            skLineSegment(sketch, "E334", {"start": v(7.14, 25.15) * mm, "end": v(8.31, 25.12) * mm});
            skLineSegment(sketch, "E335", {"start": v(8.31, 25.12) * mm, "end": v(9.49, 25.36) * mm});
            skLineSegment(sketch, "E336", {"start": v(9.49, 25.36) * mm, "end": v(11.07, 25.68) * mm});
            skLineSegment(sketch, "E337", {"start": v(11.07, 25.68) * mm, "end": v(13.3, 25.83) * mm});
            skLineSegment(sketch, "E338", {"start": v(13.3, 25.83) * mm, "end": v(15.92, 25.76) * mm});
            skLineSegment(sketch, "E339", {"start": v(15.92, 25.76) * mm, "end": v(18.66, 25.4) * mm});
            skLineSegment(sketch, "E340", {"start": v(18.66, 25.4) * mm, "end": v(21.28, 24.7) * mm});
            skLineSegment(sketch, "E341", {"start": v(21.28, 24.7) * mm, "end": v(23.5, 23.59) * mm});
            skLineSegment(sketch, "E342", {"start": v(23.5, 23.59) * mm, "end": v(25.05, 22.03) * mm});
            skLineSegment(sketch, "E343", {"start": v(25.05, 22.03) * mm, "end": v(25.7, 19.95) * mm});
            skLineSegment(sketch, "E344", {"start": v(25.7, 19.95) * mm, "end": v(26.06, 20.1) * mm});
            skLineSegment(sketch, "E345", {"start": v(26.06, 20.1) * mm, "end": v(27, 20.56) * mm});
            skLineSegment(sketch, "E346", {"start": v(27, 20.56) * mm, "end": v(28.33, 21.37) * mm});
            skLineSegment(sketch, "E347", {"start": v(28.33, 21.37) * mm, "end": v(29.8, 22.58) * mm});
            skLineSegment(sketch, "E348", {"start": v(29.8, 22.58) * mm, "end": v(31.23, 24.22) * mm});
            skLineSegment(sketch, "E349", {"start": v(31.23, 24.22) * mm, "end": v(32.39, 26.32) * mm});
            skLineSegment(sketch, "E350", {"start": v(32.39, 26.32) * mm, "end": v(33.06, 28.92) * mm});
            skLineSegment(sketch, "E351", {"start": v(33.06, 28.92) * mm, "end": v(33.04, 32.06) * mm});
            skLineSegment(sketch, "E352", {"start": v(33.04, 32.06) * mm, "end": v(33.1, 31.98) * mm});
            skLineSegment(sketch, "E353", {"start": v(33.1, 31.98) * mm, "end": v(33.25, 31.74) * mm});
            skLineSegment(sketch, "E354", {"start": v(33.25, 31.74) * mm, "end": v(33.46, 31.3) * mm});
            skLineSegment(sketch, "E355", {"start": v(33.46, 31.3) * mm, "end": v(33.7, 30.67) * mm});
            skLineSegment(sketch, "E356", {"start": v(33.7, 30.67) * mm, "end": v(33.94, 29.81) * mm});
            skLineSegment(sketch, "E357", {"start": v(33.94, 29.81) * mm, "end": v(34.13, 28.71) * mm});
            skLineSegment(sketch, "E358", {"start": v(34.13, 28.71) * mm, "end": v(34.25, 27.36) * mm});
            skLineSegment(sketch, "E359", {"start": v(34.25, 27.36) * mm, "end": v(34.27, 25.73) * mm});
            skLineSegment(sketch, "E360", {"start": v(34.27, 25.73) * mm, "end": v(34.23, 24.12) * mm});
            skLineSegment(sketch, "E361", {"start": v(34.23, 24.12) * mm, "end": v(34.22, 22.78) * mm});
            skLineSegment(sketch, "E362", {"start": v(34.22, 22.78) * mm, "end": v(34.24, 21.67) * mm});
            skLineSegment(sketch, "E363", {"start": v(34.24, 21.67) * mm, "end": v(34.3, 20.74) * mm});
            skLineSegment(sketch, "E364", {"start": v(34.3, 20.74) * mm, "end": v(34.43, 19.94) * mm});
            skLineSegment(sketch, "E365", {"start": v(34.43, 19.94) * mm, "end": v(34.62, 19.22) * mm});
            skLineSegment(sketch, "E366", {"start": v(34.62, 19.22) * mm, "end": v(34.9, 18.52) * mm});
            skLineSegment(sketch, "E367", {"start": v(34.9, 18.52) * mm, "end": v(35.27, 17.8) * mm});
            skLineSegment(sketch, "E368", {"start": v(35.27, 17.8) * mm, "end": v(35.8, 16.65) * mm});
            skLineSegment(sketch, "E369", {"start": v(35.8, 16.65) * mm, "end": v(36.4, 14.71) * mm});
            skLineSegment(sketch, "E370", {"start": v(36.4, 14.71) * mm, "end": v(36.91, 12) * mm});
            skLineSegment(sketch, "E371", {"start": v(36.91, 12) * mm, "end": v(37.12, 8.52) * mm});
            skLineSegment(sketch, "E372", {"start": v(37.12, 8.52) * mm, "end": v(36.82, 4.26) * mm});
            skLineSegment(sketch, "E373", {"start": v(36.82, 4.26) * mm, "end": v(35.84, -0.75) * mm});
            skLineSegment(sketch, "E374", {"start": v(35.84, -0.75) * mm, "end": v(33.98, -6.53) * mm});
            skLineSegment(sketch, "E375", {"start": v(33.98, -6.53) * mm, "end": v(31.04, -13.05) * mm});
            skLineSegment(sketch, "E376", {"start": v(31.04, -13.05) * mm, "end": v(30.52, -14.19) * mm});
            skLineSegment(sketch, "E377", {"start": v(30.52, -14.19) * mm, "end": v(29.13, -17.2) * mm});
            skLineSegment(sketch, "E378", {"start": v(29.13, -17.2) * mm, "end": v(27.15, -21.52) * mm});
            skLineSegment(sketch, "E379", {"start": v(27.15, -21.52) * mm, "end": v(24.86, -26.57) * mm});
            skLineSegment(sketch, "E380", {"start": v(24.86, -26.57) * mm, "end": v(22.51, -31.77) * mm});
            skLineSegment(sketch, "E381", {"start": v(22.51, -31.77) * mm, "end": v(20.4, -36.55) * mm});
            skLineSegment(sketch, "E382", {"start": v(20.4, -36.55) * mm, "end": v(18.78, -40.34) * mm});
            skLineSegment(sketch, "E383", {"start": v(18.78, -40.34) * mm, "end": v(17.93, -42.56) * mm});
            skLineSegment(sketch, "E384", {"start": v(17.93, -42.56) * mm, "end": v(17.14, -43.88) * mm});
            skLineSegment(sketch, "E385", {"start": v(17.14, -43.88) * mm, "end": v(15.64, -45.33) * mm});
            skLineSegment(sketch, "E386", {"start": v(15.64, -45.33) * mm, "end": v(13.56, -46.8) * mm});
            skLineSegment(sketch, "E387", {"start": v(13.56, -46.8) * mm, "end": v(11.06, -48.2) * mm});
            skLineSegment(sketch, "E388", {"start": v(11.06, -48.2) * mm, "end": v(8.3, -49.44) * mm});
            skLineSegment(sketch, "E389", {"start": v(8.3, -49.44) * mm, "end": v(5.43, -50.44) * mm});
            skLineSegment(sketch, "E390", {"start": v(5.43, -50.44) * mm, "end": v(2.6, -51.1) * mm});
            skLineSegment(sketch, "E391", {"start": v(2.6, -51.1) * mm, "end": v(-0.05, -51.35) * mm});
            skLineSegment(sketch, "E392", {"start": v(-0.05, -51.35) * mm, "end": v(-2.7, -51.1) * mm});
            skLineSegment(sketch, "E393", {"start": v(-2.7, -51.1) * mm, "end": v(-5.53, -50.44) * mm});
            skLineSegment(sketch, "E394", {"start": v(-5.53, -50.44) * mm, "end": v(-8.4, -49.44) * mm});
            skLineSegment(sketch, "E395", {"start": v(-8.4, -49.44) * mm, "end": v(-11.16, -48.2) * mm});
            skLineSegment(sketch, "E396", {"start": v(-11.16, -48.2) * mm, "end": v(-13.66, -46.8) * mm});
            skLineSegment(sketch, "E397", {"start": v(-13.66, -46.8) * mm, "end": v(-15.73, -45.33) * mm});
            skLineSegment(sketch, "E398", {"start": v(-15.73, -45.33) * mm, "end": v(-17.24, -43.88) * mm});
            skLineSegment(sketch, "E399", {"start": v(-17.24, -43.88) * mm, "end": v(-18.03, -42.56) * mm});
            skLineSegment(sketch, "E400", {"start": v(-18.03, -42.56) * mm, "end": v(-18.87, -40.34) * mm});
            skLineSegment(sketch, "E401", {"start": v(-18.87, -40.34) * mm, "end": v(-20.5, -36.55) * mm});
            skLineSegment(sketch, "E402", {"start": v(-20.5, -36.55) * mm, "end": v(-22.61, -31.77) * mm});
            skLineSegment(sketch, "E403", {"start": v(-22.61, -31.77) * mm, "end": v(-24.95, -26.57) * mm});
            skLineSegment(sketch, "E404", {"start": v(-24.95, -26.57) * mm, "end": v(-27.25, -21.52) * mm});
            skLineSegment(sketch, "E405", {"start": v(-27.25, -21.52) * mm, "end": v(-29.23, -17.2) * mm});
            skLineSegment(sketch, "E406", {"start": v(-29.23, -17.2) * mm, "end": v(-30.61, -14.19) * mm});
            skLineSegment(sketch, "E407", {"start": v(-30.61, -14.19) * mm, "end": v(-31.14, -13.05) * mm});
            skLineSegment(sketch, "E408", {"start": v(-31.14, -13.05) * mm, "end": v(-34.08, -6.53) * mm});
            skLineSegment(sketch, "E409", {"start": v(-34.08, -6.53) * mm, "end": v(-35.94, -0.75) * mm});
            skLineSegment(sketch, "E410", {"start": v(-35.94, -0.75) * mm, "end": v(-36.92, 4.26) * mm});
            skLineSegment(sketch, "E411", {"start": v(-36.92, 4.26) * mm, "end": v(-37.21, 8.52) * mm});
            skLineSegment(sketch, "E412", {"start": v(-37.21, 8.52) * mm, "end": v(-37, 12) * mm});
            skLineSegment(sketch, "E413", {"start": v(-37, 12) * mm, "end": v(-36.5, 14.71) * mm});
            skLineSegment(sketch, "E414", {"start": v(-36.5, 14.71) * mm, "end": v(-35.89, 16.65) * mm});
            skLineSegment(sketch, "E415", {"start": v(-35.89, 16.65) * mm, "end": v(-35.36, 17.8) * mm});
            skLineSegment(sketch, "E416", {"start": v(-35.36, 17.8) * mm, "end": v(-35, 18.52) * mm});
            skLineSegment(sketch, "E417", {"start": v(-35, 18.52) * mm, "end": v(-34.72, 19.22) * mm});
            skLineSegment(sketch, "E418", {"start": v(-34.72, 19.22) * mm, "end": v(-34.52, 19.94) * mm});
            skLineSegment(sketch, "E419", {"start": v(-34.52, 19.94) * mm, "end": v(-34.4, 20.74) * mm});
            skLineSegment(sketch, "E420", {"start": v(-34.4, 20.74) * mm, "end": v(-34.33, 21.67) * mm});
            skLineSegment(sketch, "E421", {"start": v(-34.33, 21.67) * mm, "end": v(-34.31, 22.78) * mm});
            skLineSegment(sketch, "E422", {"start": v(-34.31, 22.78) * mm, "end": v(-34.33, 24.12) * mm});
            skLineSegment(sketch, "E423", {"start": v(-34.33, 24.12) * mm, "end": v(-34.37, 25.73) * mm});
            skLineSegment(sketch, "E424", {"start": v(-34.37, 25.73) * mm, "end": v(-34.35, 27.36) * mm});
            skLineSegment(sketch, "E425", {"start": v(-34.35, 27.36) * mm, "end": v(-34.23, 28.71) * mm});
            skLineSegment(sketch, "E426", {"start": v(-34.23, 28.71) * mm, "end": v(-34.03, 29.81) * mm});
            skLineSegment(sketch, "E427", {"start": v(-34.03, 29.81) * mm, "end": v(-33.8, 30.67) * mm});
            skLineSegment(sketch, "E428", {"start": v(-33.8, 30.67) * mm, "end": v(-33.56, 31.3) * mm});
            skLineSegment(sketch, "E429", {"start": v(-33.56, 31.3) * mm, "end": v(-33.35, 31.74) * mm});
            skLineSegment(sketch, "E430", {"start": v(-33.35, 31.74) * mm, "end": v(-33.2, 31.98) * mm});
            skLineSegment(sketch, "E431", {"start": v(-33.2, 31.98) * mm, "end": v(-33.14, 32.06) * mm});
            skLineSegment(sketch, "E432", {"start": v(-33.14, 32.06) * mm, "end": v(-33.16, 28.92) * mm});
            skLineSegment(sketch, "E433", {"start": v(-33.16, 28.92) * mm, "end": v(-32.49, 26.32) * mm});
            skLineSegment(sketch, "E434", {"start": v(-32.49, 26.32) * mm, "end": v(-31.33, 24.22) * mm});
            skLineSegment(sketch, "E435", {"start": v(-31.33, 24.22) * mm, "end": v(-29.9, 22.58) * mm});
            skLineSegment(sketch, "E436", {"start": v(-29.9, 22.58) * mm, "end": v(-28.42, 21.37) * mm});
            skLineSegment(sketch, "E437", {"start": v(-28.42, 21.37) * mm, "end": v(-27.1, 20.56) * mm});
            skLineSegment(sketch, "E438", {"start": v(-27.1, 20.56) * mm, "end": v(-26.15, 20.1) * mm});
            skLineSegment(sketch, "E439", {"start": v(-26.15, 20.1) * mm, "end": v(-25.79, 19.95) * mm});
            skLineSegment(sketch, "E440", {"start": v(-25.79, 19.95) * mm, "end": v(-25.15, 22.03) * mm});
            skLineSegment(sketch, "E441", {"start": v(-25.15, 22.03) * mm, "end": v(-23.6, 23.59) * mm});
            skLineSegment(sketch, "E442", {"start": v(-23.6, 23.59) * mm, "end": v(-21.37, 24.7) * mm});
            skLineSegment(sketch, "E443", {"start": v(-21.37, 24.7) * mm, "end": v(-18.76, 25.4) * mm});
            skLineSegment(sketch, "E444", {"start": v(-18.76, 25.4) * mm, "end": v(-16.01, 25.76) * mm});
            skLineSegment(sketch, "E445", {"start": v(-16.01, 25.76) * mm, "end": v(-13.4, 25.83) * mm});
            skLineSegment(sketch, "E446", {"start": v(-13.4, 25.83) * mm, "end": v(-11.16, 25.68) * mm});
            skLineSegment(sketch, "E447", {"start": v(-11.16, 25.68) * mm, "end": v(-9.59, 25.36) * mm});
            skLineSegment(sketch, "E448", {"start": v(-9.59, 25.36) * mm, "end": v(-8.4, 25.12) * mm});
            skLineSegment(sketch, "E449", {"start": v(-8.4, 25.12) * mm, "end": v(-7.24, 25.15) * mm});
            skLineSegment(sketch, "E450", {"start": v(-7.24, 25.15) * mm, "end": v(-6.12, 25.4) * mm});
            skLineSegment(sketch, "E451", {"start": v(-6.12, 25.4) * mm, "end": v(-5.09, 25.84) * mm});
            skLineSegment(sketch, "E452", {"start": v(-5.09, 25.84) * mm, "end": v(-4.19, 26.42) * mm});
            skLineSegment(sketch, "E453", {"start": v(-4.19, 26.42) * mm, "end": v(-3.46, 27.1) * mm});
            skLineSegment(sketch, "E454", {"start": v(-3.46, 27.1) * mm, "end": v(-2.95, 27.84) * mm});
            skLineSegment(sketch, "E455", {"start": v(-2.95, 27.84) * mm, "end": v(-2.7, 28.6) * mm});
            skLineSegment(sketch, "E456", {"start": v(-2.7, 28.6) * mm, "end": v(-2.74, 29.38) * mm});
            skLineSegment(sketch, "E457", {"start": v(-2.74, 29.38) * mm, "end": v(-3.07, 30.23) * mm});
            skLineSegment(sketch, "E458", {"start": v(-3.07, 30.23) * mm, "end": v(-3.63, 31.12) * mm});
            skLineSegment(sketch, "E459", {"start": v(-3.63, 31.12) * mm, "end": v(-4.4, 32.03) * mm});
            skLineSegment(sketch, "E460", {"start": v(-4.4, 32.03) * mm, "end": v(-5.3, 32.94) * mm});
            skLineSegment(sketch, "E461", {"start": v(-5.3, 32.94) * mm, "end": v(-6.34, 33.84) * mm});
            skLineSegment(sketch, "E462", {"start": v(-6.34, 33.84) * mm, "end": v(-7.43, 34.69) * mm});
            skLineSegment(sketch, "E463", {"start": v(-7.43, 34.69) * mm, "end": v(-8.55, 35.47) * mm});
            skLineSegment(sketch, "E464", {"start": v(-8.55, 35.47) * mm, "end": v(-9.65, 36.42) * mm});
            skLineSegment(sketch, "E465", {"start": v(-9.65, 36.42) * mm, "end": v(-10.68, 37.67) * mm});
            skLineSegment(sketch, "E466", {"start": v(-10.68, 37.67) * mm, "end": v(-11.62, 39.1) * mm});
            skLineSegment(sketch, "E467", {"start": v(-11.62, 39.1) * mm, "end": v(-12.45, 40.57) * mm});
            skLineSegment(sketch, "E468", {"start": v(-12.45, 40.57) * mm, "end": v(-13.14, 41.94) * mm});
            skLineSegment(sketch, "E469", {"start": v(-13.14, 41.94) * mm, "end": v(-13.67, 43.1) * mm});
            skLineSegment(sketch, "E470", {"start": v(-13.67, 43.1) * mm, "end": v(-14, 43.88) * mm});
            skLineSegment(sketch, "E471", {"start": v(-14, 43.88) * mm, "end": v(-14.12, 44.17) * mm});
            skLineSegment(sketch, "E472", {"start": v(-14.12, 44.17) * mm, "end": v(-14.03, 44.04) * mm});
            skLineSegment(sketch, "E473", {"start": v(-14.03, 44.04) * mm, "end": v(-13.76, 43.7) * mm});
            skLineSegment(sketch, "E474", {"start": v(-13.76, 43.7) * mm, "end": v(-13.35, 43.22) * mm});
            skLineSegment(sketch, "E475", {"start": v(-13.35, 43.22) * mm, "end": v(-12.84, 42.7) * mm});
            skLineSegment(sketch, "E476", {"start": v(-12.84, 42.7) * mm, "end": v(-12.24, 42.2) * mm});
            skLineSegment(sketch, "E477", {"start": v(-12.24, 42.2) * mm, "end": v(-11.59, 41.83) * mm});
            skLineSegment(sketch, "E478", {"start": v(-11.59, 41.83) * mm, "end": v(-10.92, 41.66) * mm});
            skLineSegment(sketch, "E479", {"start": v(-10.92, 41.66) * mm, "end": v(-10.25, 41.77) * mm});
            skLineSegment(sketch, "E480", {"start": v(-10.25, 41.77) * mm, "end": v(-9.7, 42.1) * mm});
            skLineSegment(sketch, "E481", {"start": v(-9.7, 42.1) * mm, "end": v(-9.3, 42.52) * mm});
            skLineSegment(sketch, "E482", {"start": v(-9.3, 42.52) * mm, "end": v(-8.93, 42.97) * mm});
            skLineSegment(sketch, "E483", {"start": v(-8.93, 42.97) * mm, "end": v(-8.54, 43.4) * mm});
            skLineSegment(sketch, "E484", {"start": v(-8.54, 43.4) * mm, "end": v(-8.02, 43.8) * mm});
            skLineSegment(sketch, "E485", {"start": v(-8.02, 43.8) * mm, "end": v(-7.28, 44.08) * mm});
            skLineSegment(sketch, "E486", {"start": v(-7.28, 44.08) * mm, "end": v(-6.23, 44.22) * mm});
            skLineSegment(sketch, "E487", {"start": v(-6.23, 44.22) * mm, "end": v(-4.78, 44.17) * mm});
            skLineSegment(sketch, "E488", {"start": v(-4.78, 44.17) * mm, "end": v(-3.3, 44.04) * mm});
            skLineSegment(sketch, "E489", {"start": v(-3.3, 44.04) * mm, "end": v(-2.15, 43.95) * mm});
            skLineSegment(sketch, "E490", {"start": v(-2.15, 43.95) * mm, "end": v(-1.32, 43.89) * mm});
            skLineSegment(sketch, "E491", {"start": v(-1.32, 43.89) * mm, "end": v(-0.74, 43.86) * mm});
            skLineSegment(sketch, "E492", {"start": v(-0.74, 43.86) * mm, "end": v(-0.37, 43.84) * mm});
            skLineSegment(sketch, "E493", {"start": v(-0.37, 43.84) * mm, "end": v(-0.16, 43.84) * mm});
            skLineSegment(sketch, "E494", {"start": v(-0.16, 43.84) * mm, "end": v(-0.07, 43.85) * mm});
            skLineSegment(sketch, "E495", {"start": v(-0.07, 43.85) * mm, "end": v(-0.05, 43.85) * mm});
            skLineSegment(sketch, "E496", {"start": v(0.06, -42.54) * mm, "end": v(0.3, -42.5) * mm});
            skLineSegment(sketch, "E497", {"start": v(0.3, -42.5) * mm, "end": v(0.96, -42.36) * mm});
            skLineSegment(sketch, "E498", {"start": v(0.96, -42.36) * mm, "end": v(1.98, -42.16) * mm});
            skLineSegment(sketch, "E499", {"start": v(1.98, -42.16) * mm, "end": v(3.3, -41.89) * mm});
            skLineSegment(sketch, "E500", {"start": v(3.3, -41.89) * mm, "end": v(4.84, -41.57) * mm});
            skLineSegment(sketch, "E501", {"start": v(4.84, -41.57) * mm, "end": v(6.55, -41.2) * mm});
            skLineSegment(sketch, "E502", {"start": v(6.55, -41.2) * mm, "end": v(8.35, -40.8) * mm});
            skLineSegment(sketch, "E503", {"start": v(8.35, -40.8) * mm, "end": v(10.2, -40.38) * mm});
            skLineSegment(sketch, "E504", {"start": v(10.2, -40.38) * mm, "end": v(11.93, -39.42) * mm});
            skLineSegment(sketch, "E505", {"start": v(11.93, -39.42) * mm, "end": v(13.48, -37.58) * mm});
            skLineSegment(sketch, "E506", {"start": v(13.48, -37.58) * mm, "end": v(14.82, -35.18) * mm});
            skLineSegment(sketch, "E507", {"start": v(14.82, -35.18) * mm, "end": v(15.95, -32.53) * mm});
            skLineSegment(sketch, "E508", {"start": v(15.95, -32.53) * mm, "end": v(16.84, -29.94) * mm});
            skLineSegment(sketch, "E509", {"start": v(16.84, -29.94) * mm, "end": v(17.5, -27.7) * mm});
            skLineSegment(sketch, "E510", {"start": v(17.5, -27.7) * mm, "end": v(17.9, -26.13) * mm});
            skLineSegment(sketch, "E511", {"start": v(17.9, -26.13) * mm, "end": v(18.04, -25.54) * mm});
            skLineSegment(sketch, "E512", {"start": v(18.04, -25.54) * mm, "end": v(17.76, -20.88) * mm});
            skLineSegment(sketch, "E513", {"start": v(17.76, -20.88) * mm, "end": v(17.48, -16.22) * mm});
            skLineSegment(sketch, "E514", {"start": v(17.48, -16.22) * mm, "end": v(17.2, -11.56) * mm});
            skLineSegment(sketch, "E515", {"start": v(17.2, -11.56) * mm, "end": v(16.92, -6.9) * mm});
            skLineSegment(sketch, "E516", {"start": v(16.92, -6.9) * mm, "end": v(16.65, -2.23) * mm});
            skLineSegment(sketch, "E517", {"start": v(16.65, -2.23) * mm, "end": v(16.37, 2.43) * mm});
            skLineSegment(sketch, "E518", {"start": v(16.37, 2.43) * mm, "end": v(16.09, 7.1) * mm});
            skLineSegment(sketch, "E519", {"start": v(16.09, 7.1) * mm, "end": v(15.8, 11.76) * mm});
            skLineSegment(sketch, "E520", {"start": v(15.8, 11.76) * mm, "end": v(14.44, 14.82) * mm});
            skLineSegment(sketch, "E521", {"start": v(14.44, 14.82) * mm, "end": v(12.32, 16.83) * mm});
            skLineSegment(sketch, "E522", {"start": v(12.32, 16.83) * mm, "end": v(9.74, 17.98) * mm});
            skLineSegment(sketch, "E523", {"start": v(9.74, 17.98) * mm, "end": v(6.98, 18.48) * mm});
            skLineSegment(sketch, "E524", {"start": v(6.98, 18.48) * mm, "end": v(4.34, 18.52) * mm});
            skLineSegment(sketch, "E525", {"start": v(4.34, 18.52) * mm, "end": v(2.1, 18.3) * mm});
            skLineSegment(sketch, "E526", {"start": v(2.1, 18.3) * mm, "end": v(0.53, 18.02) * mm});
            skLineSegment(sketch, "E527", {"start": v(0.53, 18.02) * mm, "end": v(-0.05, 17.89) * mm});
            skLineSegment(sketch, "E528", {"start": v(-0.05, 17.89) * mm, "end": v(-0.63, 18.02) * mm});
            skLineSegment(sketch, "E529", {"start": v(-0.63, 18.02) * mm, "end": v(-2.2, 18.3) * mm});
            skLineSegment(sketch, "E530", {"start": v(-2.2, 18.3) * mm, "end": v(-4.44, 18.52) * mm});
            skLineSegment(sketch, "E531", {"start": v(-4.44, 18.52) * mm, "end": v(-7.08, 18.48) * mm});
            skLineSegment(sketch, "E532", {"start": v(-7.08, 18.48) * mm, "end": v(-9.84, 17.98) * mm});
            skLineSegment(sketch, "E533", {"start": v(-9.84, 17.98) * mm, "end": v(-12.42, 16.83) * mm});
            skLineSegment(sketch, "E534", {"start": v(-12.42, 16.83) * mm, "end": v(-14.54, 14.82) * mm});
            skLineSegment(sketch, "E535", {"start": v(-14.54, 14.82) * mm, "end": v(-15.9, 11.76) * mm});
            skLineSegment(sketch, "E536", {"start": v(-15.9, 11.76) * mm, "end": v(-16.18, 7.1) * mm});
            skLineSegment(sketch, "E537", {"start": v(-16.18, 7.1) * mm, "end": v(-16.46, 2.43) * mm});
            skLineSegment(sketch, "E538", {"start": v(-16.46, 2.43) * mm, "end": v(-16.74, -2.23) * mm});
            skLineSegment(sketch, "E539", {"start": v(-16.74, -2.23) * mm, "end": v(-17.02, -6.9) * mm});
            skLineSegment(sketch, "E540", {"start": v(-17.02, -6.9) * mm, "end": v(-17.3, -11.56) * mm});
            skLineSegment(sketch, "E541", {"start": v(-17.3, -11.56) * mm, "end": v(-17.58, -16.22) * mm});
            skLineSegment(sketch, "E542", {"start": v(-17.58, -16.22) * mm, "end": v(-17.86, -20.88) * mm});
            skLineSegment(sketch, "E543", {"start": v(-17.86, -20.88) * mm, "end": v(-18.14, -25.54) * mm});
            skLineSegment(sketch, "E544", {"start": v(-18.14, -25.54) * mm, "end": v(-18, -26.13) * mm});
            skLineSegment(sketch, "E545", {"start": v(-18, -26.13) * mm, "end": v(-17.6, -27.7) * mm});
            skLineSegment(sketch, "E546", {"start": v(-17.6, -27.7) * mm, "end": v(-16.94, -29.94) * mm});
            skLineSegment(sketch, "E547", {"start": v(-16.94, -29.94) * mm, "end": v(-16.04, -32.53) * mm});
            skLineSegment(sketch, "E548", {"start": v(-16.04, -32.53) * mm, "end": v(-14.92, -35.18) * mm});
            skLineSegment(sketch, "E549", {"start": v(-14.92, -35.18) * mm, "end": v(-13.57, -37.58) * mm});
            skLineSegment(sketch, "E550", {"start": v(-13.57, -37.58) * mm, "end": v(-12.03, -39.42) * mm});
            skLineSegment(sketch, "E551", {"start": v(-12.03, -39.42) * mm, "end": v(-10.29, -40.38) * mm});
            skLineSegment(sketch, "E552", {"start": v(-10.29, -40.38) * mm, "end": v(-8.45, -40.8) * mm});
            skLineSegment(sketch, "E553", {"start": v(-8.45, -40.8) * mm, "end": v(-6.64, -41.2) * mm});
            skLineSegment(sketch, "E554", {"start": v(-6.64, -41.2) * mm, "end": v(-4.94, -41.57) * mm});
            skLineSegment(sketch, "E555", {"start": v(-4.94, -41.57) * mm, "end": v(-3.4, -41.89) * mm});
            skLineSegment(sketch, "E556", {"start": v(-3.4, -41.89) * mm, "end": v(-2.08, -42.16) * mm});
            skLineSegment(sketch, "E557", {"start": v(-2.08, -42.16) * mm, "end": v(-1.05, -42.36) * mm});
            skLineSegment(sketch, "E558", {"start": v(-1.05, -42.36) * mm, "end": v(-0.4, -42.5) * mm});
            skLineSegment(sketch, "E559", {"start": v(-0.4, -42.5) * mm, "end": v(-0.16, -42.54) * mm});
            skLineSegment(sketch, "E560", {"start": v(-0.16, -42.54) * mm, "end": v(-0.13, -42.54) * mm});
            skLineSegment(sketch, "E561", {"start": v(-0.13, -42.54) * mm, "end": v(-0.1, -42.54) * mm});
            skLineSegment(sketch, "E562", {"start": v(-0.1, -42.54) * mm, "end": v(-0.08, -42.54) * mm});
            skLineSegment(sketch, "E563", {"start": v(-0.08, -42.54) * mm, "end": v(-0.05, -42.54) * mm});
            skLineSegment(sketch, "E564", {"start": v(-0.05, -42.54) * mm, "end": v(-0.02, -42.54) * mm});
            skLineSegment(sketch, "E565", {"start": v(-0.02, -42.54) * mm, "end": v(0, -42.54) * mm});
            skLineSegment(sketch, "E566", {"start": v(0, -42.54) * mm, "end": v(0.03, -42.54) * mm});
            skLineSegment(sketch, "E567", {"start": v(0.03, -42.54) * mm, "end": v(0.06, -42.54) * mm});
            skLineSegment(sketch, "E568", {"start": v(-24.33, 17.94) * mm, "end": v(-24.52, 15.33) * mm});
            skLineSegment(sketch, "E569", {"start": v(-24.52, 15.33) * mm, "end": v(-24.9, 8.2) * mm});
            skLineSegment(sketch, "E570", {"start": v(-24.9, 8.2) * mm, "end": v(-25.14, -2.39) * mm});
            skLineSegment(sketch, "E571", {"start": v(-25.14, -2.39) * mm, "end": v(-24.99, -15.4) * mm});
            skLineSegment(sketch, "E572", {"start": v(-24.99, -15.4) * mm, "end": v(-24.13, -29.77) * mm});
            skLineSegment(sketch, "E573", {"start": v(-24.13, -29.77) * mm, "end": v(-22.27, -44.45) * mm});
            skLineSegment(sketch, "E574", {"start": v(-22.27, -44.45) * mm, "end": v(-19.11, -58.4) * mm});
            skLineSegment(sketch, "E575", {"start": v(-19.11, -58.4) * mm, "end": v(-14.37, -70.55) * mm});
            skLineSegment(sketch, "E576", {"start": v(-14.37, -70.55) * mm, "end": v(-14.47, -67.96) * mm});
            skLineSegment(sketch, "E577", {"start": v(-14.47, -67.96) * mm, "end": v(-14.7, -60.91) * mm});
            skLineSegment(sketch, "E578", {"start": v(-14.7, -60.91) * mm, "end": v(-14.98, -50.45) * mm});
            skLineSegment(sketch, "E579", {"start": v(-14.98, -50.45) * mm, "end": v(-15.2, -37.6) * mm});
            skLineSegment(sketch, "E580", {"start": v(-15.2, -37.6) * mm, "end": v(-15.25, -23.45) * mm});
            skLineSegment(sketch, "E581", {"start": v(-15.25, -23.45) * mm, "end": v(-15.04, -9) * mm});
            skLineSegment(sketch, "E582", {"start": v(-15.04, -9) * mm, "end": v(-14.48, 4.65) * mm});
            skLineSegment(sketch, "E583", {"start": v(-14.48, 4.65) * mm, "end": v(-13.46, 16.5) * mm});
            skLineSegment(sketch, "E584", {"start": v(-13.46, 16.5) * mm, "end": v(-13.5, 16.6) * mm});
            skLineSegment(sketch, "E585", {"start": v(-13.5, 16.6) * mm, "end": v(-13.64, 16.85) * mm});
            skLineSegment(sketch, "E586", {"start": v(-13.64, 16.85) * mm, "end": v(-13.92, 17.22) * mm});
            skLineSegment(sketch, "E587", {"start": v(-13.92, 17.22) * mm, "end": v(-14.37, 17.67) * mm});
            skLineSegment(sketch, "E588", {"start": v(-14.37, 17.67) * mm, "end": v(-15.02, 18.14) * mm});
            skLineSegment(sketch, "E589", {"start": v(-15.02, 18.14) * mm, "end": v(-15.92, 18.6) * mm});
            skLineSegment(sketch, "E590", {"start": v(-15.92, 18.6) * mm, "end": v(-17.1, 19) * mm});
            skLineSegment(sketch, "E591", {"start": v(-17.1, 19) * mm, "end": v(-18.58, 19.3) * mm});
            skLineSegment(sketch, "E592", {"start": v(-18.58, 19.3) * mm, "end": v(-20.09, 19.43) * mm});
            skLineSegment(sketch, "E593", {"start": v(-20.09, 19.43) * mm, "end": v(-21.33, 19.39) * mm});
            skLineSegment(sketch, "E594", {"start": v(-21.33, 19.39) * mm, "end": v(-22.33, 19.21) * mm});
            skLineSegment(sketch, "E595", {"start": v(-22.33, 19.21) * mm, "end": v(-23.1, 18.95) * mm});
            skLineSegment(sketch, "E596", {"start": v(-23.1, 18.95) * mm, "end": v(-23.66, 18.65) * mm});
            skLineSegment(sketch, "E597", {"start": v(-23.66, 18.65) * mm, "end": v(-24.04, 18.35) * mm});
            skLineSegment(sketch, "E598", {"start": v(-24.04, 18.35) * mm, "end": v(-24.26, 18.1) * mm});
            skLineSegment(sketch, "E599", {"start": v(-24.26, 18.1) * mm, "end": v(-24.33, 17.94) * mm});
            skLineSegment(sketch, "E600", {"start": v(-13.02, 22.63) * mm, "end": v(-13.02, 22.4) * mm});
            skLineSegment(sketch, "E601", {"start": v(-13.02, 22.4) * mm, "end": v(-13, 21.75) * mm});
            skLineSegment(sketch, "E602", {"start": v(-13, 21.75) * mm, "end": v(-12.93, 20.76) * mm});
            skLineSegment(sketch, "E603", {"start": v(-12.93, 20.76) * mm, "end": v(-12.8, 19.48) * mm});
            skLineSegment(sketch, "E604", {"start": v(-12.8, 19.48) * mm, "end": v(-12.6, 17.99) * mm});
            skLineSegment(sketch, "E605", {"start": v(-12.6, 17.99) * mm, "end": v(-12.28, 16.34) * mm});
            skLineSegment(sketch, "E606", {"start": v(-12.28, 16.34) * mm, "end": v(-11.84, 14.6) * mm});
            skLineSegment(sketch, "E607", {"start": v(-11.84, 14.6) * mm, "end": v(-11.26, 12.85) * mm});
            skLineSegment(sketch, "E608", {"start": v(-11.26, 12.85) * mm, "end": v(-11.12, 12.97) * mm});
            skLineSegment(sketch, "E609", {"start": v(-11.12, 12.97) * mm, "end": v(-10.75, 13.34) * mm});
            skLineSegment(sketch, "E610", {"start": v(-10.75, 13.34) * mm, "end": v(-10.2, 13.93) * mm});
            skLineSegment(sketch, "E611", {"start": v(-10.2, 13.93) * mm, "end": v(-9.54, 14.76) * mm});
            skLineSegment(sketch, "E612", {"start": v(-9.54, 14.76) * mm, "end": v(-8.85, 15.82) * mm});
            skLineSegment(sketch, "E613", {"start": v(-8.85, 15.82) * mm, "end": v(-8.18, 17.1) * mm});
            skLineSegment(sketch, "E614", {"start": v(-8.18, 17.1) * mm, "end": v(-7.6, 18.6) * mm});
            skLineSegment(sketch, "E615", {"start": v(-7.6, 18.6) * mm, "end": v(-7.18, 20.3) * mm});
            skLineSegment(sketch, "E616", {"start": v(-7.18, 20.3) * mm, "end": v(-7.21, 20.37) * mm});
            skLineSegment(sketch, "E617", {"start": v(-7.21, 20.37) * mm, "end": v(-7.3, 20.52) * mm});
            skLineSegment(sketch, "E618", {"start": v(-7.3, 20.52) * mm, "end": v(-7.43, 20.75) * mm});
            skLineSegment(sketch, "E619", {"start": v(-7.43, 20.75) * mm, "end": v(-7.63, 21.04) * mm});
            skLineSegment(sketch, "E620", {"start": v(-7.63, 21.04) * mm, "end": v(-7.9, 21.37) * mm});
            skLineSegment(sketch, "E621", {"start": v(-7.9, 21.37) * mm, "end": v(-8.23, 21.71) * mm});
            skLineSegment(sketch, "E622", {"start": v(-8.23, 21.71) * mm, "end": v(-8.64, 22.05) * mm});
            skLineSegment(sketch, "E623", {"start": v(-8.64, 22.05) * mm, "end": v(-9.13, 22.36) * mm});
            skLineSegment(sketch, "E624", {"start": v(-9.13, 22.36) * mm, "end": v(-9.53, 22.55) * mm});
            skLineSegment(sketch, "E625", {"start": v(-9.53, 22.55) * mm, "end": v(-9.98, 22.7) * mm});
            skLineSegment(sketch, "E626", {"start": v(-9.98, 22.7) * mm, "end": v(-10.47, 22.83) * mm});
            skLineSegment(sketch, "E627", {"start": v(-10.47, 22.83) * mm, "end": v(-10.98, 22.9) * mm});
            skLineSegment(sketch, "E628", {"start": v(-10.98, 22.9) * mm, "end": v(-11.5, 22.93) * mm});
            skLineSegment(sketch, "E629", {"start": v(-11.5, 22.93) * mm, "end": v(-12.02, 22.9) * mm});
            skLineSegment(sketch, "E630", {"start": v(-12.02, 22.9) * mm, "end": v(-12.54, 22.8) * mm});
            skLineSegment(sketch, "E631", {"start": v(-12.54, 22.8) * mm, "end": v(-13.02, 22.63) * mm});
            skLineSegment(sketch, "E632", {"start": v(-5.45, 20.74) * mm, "end": v(-5.03, 20.68) * mm});
            skLineSegment(sketch, "E633", {"start": v(-5.03, 20.68) * mm, "end": v(-4.65, 20.5) * mm});
            skLineSegment(sketch, "E634", {"start": v(-4.65, 20.5) * mm, "end": v(-4.32, 20.25) * mm});
            skLineSegment(sketch, "E635", {"start": v(-4.32, 20.25) * mm, "end": v(-4.05, 19.92) * mm});
            skLineSegment(sketch, "E636", {"start": v(-4.05, 19.92) * mm, "end": v(-3.85, 19.55) * mm});
            skLineSegment(sketch, "E637", {"start": v(-3.85, 19.55) * mm, "end": v(-3.74, 19.15) * mm});
            skLineSegment(sketch, "E638", {"start": v(-3.74, 19.15) * mm, "end": v(-3.74, 18.75) * mm});
            skLineSegment(sketch, "E639", {"start": v(-3.74, 18.75) * mm, "end": v(-3.85, 18.38) * mm});
            skLineSegment(sketch, "E640", {"start": v(-3.85, 18.38) * mm, "end": v(-4.05, 18) * mm});
            skLineSegment(sketch, "E641", {"start": v(-4.05, 18) * mm, "end": v(-4.29, 17.6) * mm});
            skLineSegment(sketch, "E642", {"start": v(-4.29, 17.6) * mm, "end": v(-4.55, 17.22) * mm});
            skLineSegment(sketch, "E643", {"start": v(-4.55, 17.22) * mm, "end": v(-4.82, 16.85) * mm});
            skLineSegment(sketch, "E644", {"start": v(-4.82, 16.85) * mm, "end": v(-5.07, 16.53) * mm});
            skLineSegment(sketch, "E645", {"start": v(-5.07, 16.53) * mm, "end": v(-5.27, 16.28) * mm});
            skLineSegment(sketch, "E646", {"start": v(-5.27, 16.28) * mm, "end": v(-5.4, 16.11) * mm});
            skLineSegment(sketch, "E647", {"start": v(-5.4, 16.11) * mm, "end": v(-5.46, 16.05) * mm});
            skLineSegment(sketch, "E648", {"start": v(-5.46, 16.05) * mm, "end": v(-5.53, 16.13) * mm});
            skLineSegment(sketch, "E649", {"start": v(-5.53, 16.13) * mm, "end": v(-5.71, 16.34) * mm});
            skLineSegment(sketch, "E650", {"start": v(-5.71, 16.34) * mm, "end": v(-5.98, 16.65) * mm});
            skLineSegment(sketch, "E651", {"start": v(-5.98, 16.65) * mm, "end": v(-6.29, 17.04) * mm});
            skLineSegment(sketch, "E652", {"start": v(-6.29, 17.04) * mm, "end": v(-6.6, 17.49) * mm});
            skLineSegment(sketch, "E653", {"start": v(-6.6, 17.49) * mm, "end": v(-6.88, 17.96) * mm});
            skLineSegment(sketch, "E654", {"start": v(-6.88, 17.96) * mm, "end": v(-7.08, 18.44) * mm});
            skLineSegment(sketch, "E655", {"start": v(-7.08, 18.44) * mm, "end": v(-7.18, 18.9) * mm});
            skLineSegment(sketch, "E656", {"start": v(-7.18, 18.9) * mm, "end": v(-7.17, 19.3) * mm});
            skLineSegment(sketch, "E657", {"start": v(-7.17, 19.3) * mm, "end": v(-7.08, 19.67) * mm});
            skLineSegment(sketch, "E658", {"start": v(-7.08, 19.67) * mm, "end": v(-6.93, 19.99) * mm});
            skLineSegment(sketch, "E659", {"start": v(-6.93, 19.99) * mm, "end": v(-6.72, 20.25) * mm});
            skLineSegment(sketch, "E660", {"start": v(-6.72, 20.25) * mm, "end": v(-6.45, 20.46) * mm});
            skLineSegment(sketch, "E661", {"start": v(-6.45, 20.46) * mm, "end": v(-6.15, 20.62) * mm});
            skLineSegment(sketch, "E662", {"start": v(-6.15, 20.62) * mm, "end": v(-5.81, 20.71) * mm});
            skLineSegment(sketch, "E663", {"start": v(-5.81, 20.71) * mm, "end": v(-5.45, 20.74) * mm});
            skLineSegment(sketch, "E664", {"start": v(-1.9, 20.08) * mm, "end": v(-1.5, 20.02) * mm});
            skLineSegment(sketch, "E665", {"start": v(-1.5, 20.02) * mm, "end": v(-1.15, 19.86) * mm});
            skLineSegment(sketch, "E666", {"start": v(-1.15, 19.86) * mm, "end": v(-0.84, 19.62) * mm});
            skLineSegment(sketch, "E667", {"start": v(-0.84, 19.62) * mm, "end": v(-0.6, 19.32) * mm});
            skLineSegment(sketch, "E668", {"start": v(-0.6, 19.32) * mm, "end": v(-0.41, 18.97) * mm});
            skLineSegment(sketch, "E669", {"start": v(-0.41, 18.97) * mm, "end": v(-0.31, 18.6) * mm});
            skLineSegment(sketch, "E670", {"start": v(-0.31, 18.6) * mm, "end": v(-0.3, 18.24) * mm});
            skLineSegment(sketch, "E671", {"start": v(-0.3, 18.24) * mm, "end": v(-0.4, 17.89) * mm});
            skLineSegment(sketch, "E672", {"start": v(-0.4, 17.89) * mm, "end": v(-0.6, 17.54) * mm});
            skLineSegment(sketch, "E673", {"start": v(-0.6, 17.54) * mm, "end": v(-0.82, 17.18) * mm});
            skLineSegment(sketch, "E674", {"start": v(-0.82, 17.18) * mm, "end": v(-1.06, 16.82) * mm});
            skLineSegment(sketch, "E675", {"start": v(-1.06, 16.82) * mm, "end": v(-1.3, 16.48) * mm});
            skLineSegment(sketch, "E676", {"start": v(-1.3, 16.48) * mm, "end": v(-1.54, 16.18) * mm});
            skLineSegment(sketch, "E677", {"start": v(-1.54, 16.18) * mm, "end": v(-1.72, 15.95) * mm});
            skLineSegment(sketch, "E678", {"start": v(-1.72, 15.95) * mm, "end": v(-1.85, 15.8) * mm});
            skLineSegment(sketch, "E679", {"start": v(-1.85, 15.8) * mm, "end": v(-1.9, 15.74) * mm});
            skLineSegment(sketch, "E680", {"start": v(-1.9, 15.74) * mm, "end": v(-1.96, 15.8) * mm});
            skLineSegment(sketch, "E681", {"start": v(-1.96, 15.8) * mm, "end": v(-2.14, 16) * mm});
            skLineSegment(sketch, "E682", {"start": v(-2.14, 16) * mm, "end": v(-2.38, 16.29) * mm});
            skLineSegment(sketch, "E683", {"start": v(-2.38, 16.29) * mm, "end": v(-2.67, 16.65) * mm});
            skLineSegment(sketch, "E684", {"start": v(-2.67, 16.65) * mm, "end": v(-2.95, 17.07) * mm});
            skLineSegment(sketch, "E685", {"start": v(-2.95, 17.07) * mm, "end": v(-3.21, 17.5) * mm});
            skLineSegment(sketch, "E686", {"start": v(-3.21, 17.5) * mm, "end": v(-3.4, 17.95) * mm});
            skLineSegment(sketch, "E687", {"start": v(-3.4, 17.95) * mm, "end": v(-3.5, 18.37) * mm});
            skLineSegment(sketch, "E688", {"start": v(-3.5, 18.37) * mm, "end": v(-3.48, 18.75) * mm});
            skLineSegment(sketch, "E689", {"start": v(-3.48, 18.75) * mm, "end": v(-3.4, 19.08) * mm});
            skLineSegment(sketch, "E690", {"start": v(-3.4, 19.08) * mm, "end": v(-3.26, 19.38) * mm});
            skLineSegment(sketch, "E691", {"start": v(-3.26, 19.38) * mm, "end": v(-3.06, 19.62) * mm});
            skLineSegment(sketch, "E692", {"start": v(-3.06, 19.62) * mm, "end": v(-2.82, 19.82) * mm});
            skLineSegment(sketch, "E693", {"start": v(-2.82, 19.82) * mm, "end": v(-2.54, 19.96) * mm});
            skLineSegment(sketch, "E694", {"start": v(-2.54, 19.96) * mm, "end": v(-2.23, 20.05) * mm});
            skLineSegment(sketch, "E695", {"start": v(-2.23, 20.05) * mm, "end": v(-1.9, 20.08) * mm});
            skLineSegment(sketch, "E696", {"start": v(12.68, 22.63) * mm, "end": v(12.67, 22.4) * mm});
            skLineSegment(sketch, "E697", {"start": v(12.67, 22.4) * mm, "end": v(12.65, 21.75) * mm});
            skLineSegment(sketch, "E698", {"start": v(12.65, 21.75) * mm, "end": v(12.58, 20.76) * mm});
            skLineSegment(sketch, "E699", {"start": v(12.58, 20.76) * mm, "end": v(12.46, 19.48) * mm});
            skLineSegment(sketch, "E700", {"start": v(12.46, 19.48) * mm, "end": v(12.25, 17.99) * mm});
            skLineSegment(sketch, "E701", {"start": v(12.25, 17.99) * mm, "end": v(11.94, 16.34) * mm});
            skLineSegment(sketch, "E702", {"start": v(11.94, 16.34) * mm, "end": v(11.5, 14.6) * mm});
            skLineSegment(sketch, "E703", {"start": v(11.5, 14.6) * mm, "end": v(10.92, 12.85) * mm});
            skLineSegment(sketch, "E704", {"start": v(10.92, 12.85) * mm, "end": v(10.78, 12.97) * mm});
            skLineSegment(sketch, "E705", {"start": v(10.78, 12.97) * mm, "end": v(10.4, 13.34) * mm});
            skLineSegment(sketch, "E706", {"start": v(10.4, 13.34) * mm, "end": v(9.85, 13.93) * mm});
            skLineSegment(sketch, "E707", {"start": v(9.85, 13.93) * mm, "end": v(9.2, 14.76) * mm});
            skLineSegment(sketch, "E708", {"start": v(9.2, 14.76) * mm, "end": v(8.5, 15.82) * mm});
            skLineSegment(sketch, "E709", {"start": v(8.5, 15.82) * mm, "end": v(7.83, 17.1) * mm});
            skLineSegment(sketch, "E710", {"start": v(7.83, 17.1) * mm, "end": v(7.26, 18.6) * mm});
            skLineSegment(sketch, "E711", {"start": v(7.26, 18.6) * mm, "end": v(6.84, 20.3) * mm});
            skLineSegment(sketch, "E712", {"start": v(6.84, 20.3) * mm, "end": v(6.87, 20.37) * mm});
            skLineSegment(sketch, "E713", {"start": v(6.87, 20.37) * mm, "end": v(6.95, 20.52) * mm});
            skLineSegment(sketch, "E714", {"start": v(6.95, 20.52) * mm, "end": v(7.09, 20.75) * mm});
            skLineSegment(sketch, "E715", {"start": v(7.09, 20.75) * mm, "end": v(7.29, 21.04) * mm});
            skLineSegment(sketch, "E716", {"start": v(7.29, 21.04) * mm, "end": v(7.55, 21.37) * mm});
            skLineSegment(sketch, "E717", {"start": v(7.55, 21.37) * mm, "end": v(7.89, 21.71) * mm});
            skLineSegment(sketch, "E718", {"start": v(7.89, 21.71) * mm, "end": v(8.3, 22.05) * mm});
            skLineSegment(sketch, "E719", {"start": v(8.3, 22.05) * mm, "end": v(8.79, 22.36) * mm});
            skLineSegment(sketch, "E720", {"start": v(8.79, 22.36) * mm, "end": v(9.19, 22.55) * mm});
            skLineSegment(sketch, "E721", {"start": v(9.19, 22.55) * mm, "end": v(9.64, 22.7) * mm});
            skLineSegment(sketch, "E722", {"start": v(9.64, 22.7) * mm, "end": v(10.12, 22.83) * mm});
            skLineSegment(sketch, "E723", {"start": v(10.12, 22.83) * mm, "end": v(10.63, 22.9) * mm});
            skLineSegment(sketch, "E724", {"start": v(10.63, 22.9) * mm, "end": v(11.16, 22.93) * mm});
            skLineSegment(sketch, "E725", {"start": v(11.16, 22.93) * mm, "end": v(11.68, 22.9) * mm});
            skLineSegment(sketch, "E726", {"start": v(11.68, 22.9) * mm, "end": v(12.2, 22.8) * mm});
            skLineSegment(sketch, "E727", {"start": v(12.2, 22.8) * mm, "end": v(12.68, 22.63) * mm});
            skLineSegment(sketch, "E728", {"start": v(5.1, 20.74) * mm, "end": v(4.69, 20.68) * mm});
            skLineSegment(sketch, "E729", {"start": v(4.69, 20.68) * mm, "end": v(4.3, 20.5) * mm});
            skLineSegment(sketch, "E730", {"start": v(4.3, 20.5) * mm, "end": v(3.97, 20.25) * mm});
            skLineSegment(sketch, "E731", {"start": v(3.97, 20.25) * mm, "end": v(3.7, 19.92) * mm});
            skLineSegment(sketch, "E732", {"start": v(3.7, 19.92) * mm, "end": v(3.5, 19.55) * mm});
            skLineSegment(sketch, "E733", {"start": v(3.5, 19.55) * mm, "end": v(3.4, 19.15) * mm});
            skLineSegment(sketch, "E734", {"start": v(3.4, 19.15) * mm, "end": v(3.4, 18.75) * mm});
            skLineSegment(sketch, "E735", {"start": v(3.4, 18.75) * mm, "end": v(3.5, 18.38) * mm});
            skLineSegment(sketch, "E736", {"start": v(3.5, 18.38) * mm, "end": v(3.7, 18) * mm});
            skLineSegment(sketch, "E737", {"start": v(3.7, 18) * mm, "end": v(3.94, 17.6) * mm});
            skLineSegment(sketch, "E738", {"start": v(3.94, 17.6) * mm, "end": v(4.2, 17.22) * mm});
            skLineSegment(sketch, "E739", {"start": v(4.2, 17.22) * mm, "end": v(4.47, 16.85) * mm});
            skLineSegment(sketch, "E740", {"start": v(4.47, 16.85) * mm, "end": v(4.72, 16.53) * mm});
            skLineSegment(sketch, "E741", {"start": v(4.72, 16.53) * mm, "end": v(4.92, 16.28) * mm});
            skLineSegment(sketch, "E742", {"start": v(4.92, 16.28) * mm, "end": v(5.06, 16.11) * mm});
            skLineSegment(sketch, "E743", {"start": v(5.06, 16.11) * mm, "end": v(5.1, 16.05) * mm});
            skLineSegment(sketch, "E744", {"start": v(5.1, 16.05) * mm, "end": v(5.18, 16.13) * mm});
            skLineSegment(sketch, "E745", {"start": v(5.18, 16.13) * mm, "end": v(5.37, 16.34) * mm});
            skLineSegment(sketch, "E746", {"start": v(5.37, 16.34) * mm, "end": v(5.63, 16.65) * mm});
            skLineSegment(sketch, "E747", {"start": v(5.63, 16.65) * mm, "end": v(5.94, 17.04) * mm});
            skLineSegment(sketch, "E748", {"start": v(5.94, 17.04) * mm, "end": v(6.25, 17.49) * mm});
            skLineSegment(sketch, "E749", {"start": v(6.25, 17.49) * mm, "end": v(6.53, 17.96) * mm});
            skLineSegment(sketch, "E750", {"start": v(6.53, 17.96) * mm, "end": v(6.74, 18.44) * mm});
            skLineSegment(sketch, "E751", {"start": v(6.74, 18.44) * mm, "end": v(6.83, 18.9) * mm});
            skLineSegment(sketch, "E752", {"start": v(6.83, 18.9) * mm, "end": v(6.82, 19.3) * mm});
            skLineSegment(sketch, "E753", {"start": v(6.82, 19.3) * mm, "end": v(6.74, 19.67) * mm});
            skLineSegment(sketch, "E754", {"start": v(6.74, 19.67) * mm, "end": v(6.58, 19.99) * mm});
            skLineSegment(sketch, "E755", {"start": v(6.58, 19.99) * mm, "end": v(6.37, 20.25) * mm});
            skLineSegment(sketch, "E756", {"start": v(6.37, 20.25) * mm, "end": v(6.1, 20.46) * mm});
            skLineSegment(sketch, "E757", {"start": v(6.1, 20.46) * mm, "end": v(5.8, 20.62) * mm});
            skLineSegment(sketch, "E758", {"start": v(5.8, 20.62) * mm, "end": v(5.47, 20.71) * mm});
            skLineSegment(sketch, "E759", {"start": v(5.47, 20.71) * mm, "end": v(5.1, 20.74) * mm});
            skLineSegment(sketch, "E760", {"start": v(1.55, 20.08) * mm, "end": v(1.16, 20.02) * mm});
            skLineSegment(sketch, "E761", {"start": v(1.16, 20.02) * mm, "end": v(0.8, 19.86) * mm});
            skLineSegment(sketch, "E762", {"start": v(0.8, 19.86) * mm, "end": v(0.5, 19.62) * mm});
            skLineSegment(sketch, "E763", {"start": v(0.5, 19.62) * mm, "end": v(0.25, 19.32) * mm});
            skLineSegment(sketch, "E764", {"start": v(0.25, 19.32) * mm, "end": v(0.07, 18.97) * mm});
            skLineSegment(sketch, "E765", {"start": v(0.07, 18.97) * mm, "end": v(-0.03, 18.6) * mm});
            skLineSegment(sketch, "E766", {"start": v(-0.03, 18.6) * mm, "end": v(-0.04, 18.24) * mm});
            skLineSegment(sketch, "E767", {"start": v(-0.04, 18.24) * mm, "end": v(0.06, 17.89) * mm});
            skLineSegment(sketch, "E768", {"start": v(0.06, 17.89) * mm, "end": v(0.25, 17.54) * mm});
            skLineSegment(sketch, "E769", {"start": v(0.25, 17.54) * mm, "end": v(0.47, 17.18) * mm});
            skLineSegment(sketch, "E770", {"start": v(0.47, 17.18) * mm, "end": v(0.72, 16.82) * mm});
            skLineSegment(sketch, "E771", {"start": v(0.72, 16.82) * mm, "end": v(0.96, 16.48) * mm});
            skLineSegment(sketch, "E772", {"start": v(0.96, 16.48) * mm, "end": v(1.2, 16.18) * mm});
            skLineSegment(sketch, "E773", {"start": v(1.2, 16.18) * mm, "end": v(1.38, 15.95) * mm});
            skLineSegment(sketch, "E774", {"start": v(1.38, 15.95) * mm, "end": v(1.5, 15.8) * mm});
            skLineSegment(sketch, "E775", {"start": v(1.5, 15.8) * mm, "end": v(1.55, 15.74) * mm});
            skLineSegment(sketch, "E776", {"start": v(1.55, 15.74) * mm, "end": v(1.62, 15.8) * mm});
            skLineSegment(sketch, "E777", {"start": v(1.62, 15.8) * mm, "end": v(1.8, 16) * mm});
            skLineSegment(sketch, "E778", {"start": v(1.8, 16) * mm, "end": v(2.04, 16.29) * mm});
            skLineSegment(sketch, "E779", {"start": v(2.04, 16.29) * mm, "end": v(2.32, 16.65) * mm});
            skLineSegment(sketch, "E780", {"start": v(2.32, 16.65) * mm, "end": v(2.6, 17.07) * mm});
            skLineSegment(sketch, "E781", {"start": v(2.6, 17.07) * mm, "end": v(2.87, 17.5) * mm});
            skLineSegment(sketch, "E782", {"start": v(2.87, 17.5) * mm, "end": v(3.06, 17.95) * mm});
            skLineSegment(sketch, "E783", {"start": v(3.06, 17.95) * mm, "end": v(3.15, 18.37) * mm});
            skLineSegment(sketch, "E784", {"start": v(3.15, 18.37) * mm, "end": v(3.14, 18.75) * mm});
            skLineSegment(sketch, "E785", {"start": v(3.14, 18.75) * mm, "end": v(3.06, 19.08) * mm});
            skLineSegment(sketch, "E786", {"start": v(3.06, 19.08) * mm, "end": v(2.92, 19.38) * mm});
            skLineSegment(sketch, "E787", {"start": v(2.92, 19.38) * mm, "end": v(2.72, 19.62) * mm});
            skLineSegment(sketch, "E788", {"start": v(2.72, 19.62) * mm, "end": v(2.48, 19.82) * mm});
            skLineSegment(sketch, "E789", {"start": v(2.48, 19.82) * mm, "end": v(2.2, 19.96) * mm});
            skLineSegment(sketch, "E790", {"start": v(2.2, 19.96) * mm, "end": v(1.88, 20.05) * mm});
            skLineSegment(sketch, "E791", {"start": v(1.88, 20.05) * mm, "end": v(1.55, 20.08) * mm});
            skLineSegment(sketch, "E792", {"start": v(-8.28, -41.69) * mm, "end": v(-8.62, -42.08) * mm});
            skLineSegment(sketch, "E793", {"start": v(-8.62, -42.08) * mm, "end": v(-9.07, -42.34) * mm});
            skLineSegment(sketch, "E794", {"start": v(-9.07, -42.34) * mm, "end": v(-9.56, -42.49) * mm});
            skLineSegment(sketch, "E795", {"start": v(-9.56, -42.49) * mm, "end": v(-10.06, -42.55) * mm});
            skLineSegment(sketch, "E796", {"start": v(-10.06, -42.55) * mm, "end": v(-10.53, -42.56) * mm});
            skLineSegment(sketch, "E797", {"start": v(-10.53, -42.56) * mm, "end": v(-10.91, -42.53) * mm});
            skLineSegment(sketch, "E798", {"start": v(-10.91, -42.53) * mm, "end": v(-11.18, -42.49) * mm});
            skLineSegment(sketch, "E799", {"start": v(-11.18, -42.49) * mm, "end": v(-11.28, -42.47) * mm});
            skLineSegment(sketch, "E800", {"start": v(-11.28, -42.47) * mm, "end": v(-12.19, -40.75) * mm});
            skLineSegment(sketch, "E801", {"start": v(-12.19, -40.75) * mm, "end": v(-12.63, -39.1) * mm});
            skLineSegment(sketch, "E802", {"start": v(-12.63, -39.1) * mm, "end": v(-12.7, -37.56) * mm});
            skLineSegment(sketch, "E803", {"start": v(-12.7, -37.56) * mm, "end": v(-12.53, -36.2) * mm});
            skLineSegment(sketch, "E804", {"start": v(-12.53, -36.2) * mm, "end": v(-12.2, -35.05) * mm});
            skLineSegment(sketch, "E805", {"start": v(-12.2, -35.05) * mm, "end": v(-11.84, -34.17) * mm});
            skLineSegment(sketch, "E806", {"start": v(-11.84, -34.17) * mm, "end": v(-11.55, -33.6) * mm});
            skLineSegment(sketch, "E807", {"start": v(-11.55, -33.6) * mm, "end": v(-11.42, -33.4) * mm});
            skLineSegment(sketch, "E808", {"start": v(-11.42, -33.4) * mm, "end": v(-11.37, -33.53) * mm});
            skLineSegment(sketch, "E809", {"start": v(-11.37, -33.53) * mm, "end": v(-11.2, -33.9) * mm});
            skLineSegment(sketch, "E810", {"start": v(-11.2, -33.9) * mm, "end": v(-10.94, -34.41) * mm});
            skLineSegment(sketch, "E811", {"start": v(-10.94, -34.41) * mm, "end": v(-10.58, -35.04) * mm});
            skLineSegment(sketch, "E812", {"start": v(-10.58, -35.04) * mm, "end": v(-10.15, -35.72) * mm});
            skLineSegment(sketch, "E813", {"start": v(-10.15, -35.72) * mm, "end": v(-9.64, -36.4) * mm});
            skLineSegment(sketch, "E814", {"start": v(-9.64, -36.4) * mm, "end": v(-9.07, -37) * mm});
            skLineSegment(sketch, "E815", {"start": v(-9.07, -37) * mm, "end": v(-8.45, -37.47) * mm});
            skLineSegment(sketch, "E816", {"start": v(-8.45, -37.47) * mm, "end": v(-7.95, -37.96) * mm});
            skLineSegment(sketch, "E817", {"start": v(-7.95, -37.96) * mm, "end": v(-7.7, -38.58) * mm});
            skLineSegment(sketch, "E818", {"start": v(-7.7, -38.58) * mm, "end": v(-7.64, -39.27) * mm});
            skLineSegment(sketch, "E819", {"start": v(-7.64, -39.27) * mm, "end": v(-7.72, -39.97) * mm});
            skLineSegment(sketch, "E820", {"start": v(-7.72, -39.97) * mm, "end": v(-7.88, -40.63) * mm});
            skLineSegment(sketch, "E821", {"start": v(-7.88, -40.63) * mm, "end": v(-8.06, -41.17) * mm});
            skLineSegment(sketch, "E822", {"start": v(-8.06, -41.17) * mm, "end": v(-8.22, -41.55) * mm});
            skLineSegment(sketch, "E823", {"start": v(-8.22, -41.55) * mm, "end": v(-8.28, -41.69) * mm});
            skLineSegment(sketch, "E824", {"start": v(-7.3, -34.49) * mm, "end": v(-7.42, -34.65) * mm});
            skLineSegment(sketch, "E825", {"start": v(-7.42, -34.65) * mm, "end": v(-7.68, -35.1) * mm});
            skLineSegment(sketch, "E826", {"start": v(-7.68, -35.1) * mm, "end": v(-8.03, -35.85) * mm});
            skLineSegment(sketch, "E827", {"start": v(-8.03, -35.85) * mm, "end": v(-8.37, -36.85) * mm});
            skLineSegment(sketch, "E828", {"start": v(-8.37, -36.85) * mm, "end": v(-8.63, -38.08) * mm});
            skLineSegment(sketch, "E829", {"start": v(-8.63, -38.08) * mm, "end": v(-8.72, -39.54) * mm});
            skLineSegment(sketch, "E830", {"start": v(-8.72, -39.54) * mm, "end": v(-8.56, -41.19) * mm});
            skLineSegment(sketch, "E831", {"start": v(-8.56, -41.19) * mm, "end": v(-8.06, -43.02) * mm});
            skLineSegment(sketch, "E832", {"start": v(-8.06, -43.02) * mm, "end": v(-8.03, -43.06) * mm});
            skLineSegment(sketch, "E833", {"start": v(-8.03, -43.06) * mm, "end": v(-7.96, -43.14) * mm});
            skLineSegment(sketch, "E834", {"start": v(-7.96, -43.14) * mm, "end": v(-7.86, -43.22) * mm});
            skLineSegment(sketch, "E835", {"start": v(-7.86, -43.22) * mm, "end": v(-7.7, -43.32) * mm});
            skLineSegment(sketch, "E836", {"start": v(-7.7, -43.32) * mm, "end": v(-7.51, -43.4) * mm});
            skLineSegment(sketch, "E837", {"start": v(-7.51, -43.4) * mm, "end": v(-7.27, -43.47) * mm});
            skLineSegment(sketch, "E838", {"start": v(-7.27, -43.47) * mm, "end": v(-6.98, -43.5) * mm});
            skLineSegment(sketch, "E839", {"start": v(-6.98, -43.5) * mm, "end": v(-6.64, -43.5) * mm});
            skLineSegment(sketch, "E840", {"start": v(-6.64, -43.5) * mm, "end": v(-6.42, -43.45) * mm});
            skLineSegment(sketch, "E841", {"start": v(-6.42, -43.45) * mm, "end": v(-6.22, -43.4) * mm});
            skLineSegment(sketch, "E842", {"start": v(-6.22, -43.4) * mm, "end": v(-6.05, -43.33) * mm});
            skLineSegment(sketch, "E843", {"start": v(-6.05, -43.33) * mm, "end": v(-5.9, -43.24) * mm});
            skLineSegment(sketch, "E844", {"start": v(-5.9, -43.24) * mm, "end": v(-5.78, -43.16) * mm});
            skLineSegment(sketch, "E845", {"start": v(-5.78, -43.16) * mm, "end": v(-5.68, -43.07) * mm});
            skLineSegment(sketch, "E846", {"start": v(-5.68, -43.07) * mm, "end": v(-5.6, -43) * mm});
            skLineSegment(sketch, "E847", {"start": v(-5.6, -43) * mm, "end": v(-5.56, -42.92) * mm});
            skLineSegment(sketch, "E848", {"start": v(-5.56, -42.92) * mm, "end": v(-5.33, -42.2) * mm});
            skLineSegment(sketch, "E849", {"start": v(-5.33, -42.2) * mm, "end": v(-5.2, -41.2) * mm});
            skLineSegment(sketch, "E850", {"start": v(-5.2, -41.2) * mm, "end": v(-5.2, -40) * mm});
            skLineSegment(sketch, "E851", {"start": v(-5.2, -40) * mm, "end": v(-5.32, -38.72) * mm});
            skLineSegment(sketch, "E852", {"start": v(-5.32, -38.72) * mm, "end": v(-5.59, -37.43) * mm});
            skLineSegment(sketch, "E853", {"start": v(-5.59, -37.43) * mm, "end": v(-6, -36.23) * mm});
            skLineSegment(sketch, "E854", {"start": v(-6, -36.23) * mm, "end": v(-6.57, -35.22) * mm});
            skLineSegment(sketch, "E855", {"start": v(-6.57, -35.22) * mm, "end": v(-7.3, -34.49) * mm});
            skLineSegment(sketch, "E856", {"start": v(-4.14, -37.26) * mm, "end": v(-4.21, -37.35) * mm});
            skLineSegment(sketch, "E857", {"start": v(-4.21, -37.35) * mm, "end": v(-4.4, -37.6) * mm});
            skLineSegment(sketch, "E858", {"start": v(-4.4, -37.6) * mm, "end": v(-4.67, -38.01) * mm});
            skLineSegment(sketch, "E859", {"start": v(-4.67, -38.01) * mm, "end": v(-4.95, -38.55) * mm});
            skLineSegment(sketch, "E860", {"start": v(-4.95, -38.55) * mm, "end": v(-5.2, -39.18) * mm});
            skLineSegment(sketch, "E861", {"start": v(-5.2, -39.18) * mm, "end": v(-5.37, -39.9) * mm});
            skLineSegment(sketch, "E862", {"start": v(-5.37, -39.9) * mm, "end": v(-5.42, -40.7) * mm});
            skLineSegment(sketch, "E863", {"start": v(-5.42, -40.7) * mm, "end": v(-5.3, -41.52) * mm});
            skLineSegment(sketch, "E864", {"start": v(-5.3, -41.52) * mm, "end": v(-5.21, -41.81) * mm});
            skLineSegment(sketch, "E865", {"start": v(-5.21, -41.81) * mm, "end": v(-5.14, -42.06) * mm});
            skLineSegment(sketch, "E866", {"start": v(-5.14, -42.06) * mm, "end": v(-5.06, -42.28) * mm});
            skLineSegment(sketch, "E867", {"start": v(-5.06, -42.28) * mm, "end": v(-4.99, -42.47) * mm});
            skLineSegment(sketch, "E868", {"start": v(-4.99, -42.47) * mm, "end": v(-4.91, -42.63) * mm});
            skLineSegment(sketch, "E869", {"start": v(-4.91, -42.63) * mm, "end": v(-4.83, -42.78) * mm});
            skLineSegment(sketch, "E870", {"start": v(-4.83, -42.78) * mm, "end": v(-4.75, -42.9) * mm});
            skLineSegment(sketch, "E871", {"start": v(-4.75, -42.9) * mm, "end": v(-4.66, -43.01) * mm});
            skLineSegment(sketch, "E872", {"start": v(-4.66, -43.01) * mm, "end": v(-4.5, -43.18) * mm});
            skLineSegment(sketch, "E873", {"start": v(-4.5, -43.18) * mm, "end": v(-4.37, -43.3) * mm});
            skLineSegment(sketch, "E874", {"start": v(-4.37, -43.3) * mm, "end": v(-4.25, -43.38) * mm});
            skLineSegment(sketch, "E875", {"start": v(-4.25, -43.38) * mm, "end": v(-4.13, -43.44) * mm});
            skLineSegment(sketch, "E876", {"start": v(-4.13, -43.44) * mm, "end": v(-4.01, -43.48) * mm});
            skLineSegment(sketch, "E877", {"start": v(-4.01, -43.48) * mm, "end": v(-3.88, -43.5) * mm});
            skLineSegment(sketch, "E878", {"start": v(-3.88, -43.5) * mm, "end": v(-3.74, -43.5) * mm});
            skLineSegment(sketch, "E879", {"start": v(-3.74, -43.5) * mm, "end": v(-3.57, -43.5) * mm});
            skLineSegment(sketch, "E880", {"start": v(-3.57, -43.5) * mm, "end": v(-3.45, -43.49) * mm});
            skLineSegment(sketch, "E881", {"start": v(-3.45, -43.49) * mm, "end": v(-3.34, -43.44) * mm});
            skLineSegment(sketch, "E882", {"start": v(-3.34, -43.44) * mm, "end": v(-3.23, -43.38) * mm});
            skLineSegment(sketch, "E883", {"start": v(-3.23, -43.38) * mm, "end": v(-3.13, -43.3) * mm});
            skLineSegment(sketch, "E884", {"start": v(-3.13, -43.3) * mm, "end": v(-3.04, -43.2) * mm});
            skLineSegment(sketch, "E885", {"start": v(-3.04, -43.2) * mm, "end": v(-2.96, -43.08) * mm});
            skLineSegment(sketch, "E886", {"start": v(-2.96, -43.08) * mm, "end": v(-2.89, -42.97) * mm});
            skLineSegment(sketch, "E887", {"start": v(-2.89, -42.97) * mm, "end": v(-2.83, -42.85) * mm});
            skLineSegment(sketch, "E888", {"start": v(-2.83, -42.85) * mm, "end": v(-2.68, -42.34) * mm});
            skLineSegment(sketch, "E889", {"start": v(-2.68, -42.34) * mm, "end": v(-2.57, -41.7) * mm});
            skLineSegment(sketch, "E890", {"start": v(-2.57, -41.7) * mm, "end": v(-2.53, -41) * mm});
            skLineSegment(sketch, "E891", {"start": v(-2.53, -41) * mm, "end": v(-2.6, -40.22) * mm});
            skLineSegment(sketch, "E892", {"start": v(-2.6, -40.22) * mm, "end": v(-2.76, -39.43) * mm});
            skLineSegment(sketch, "E893", {"start": v(-2.76, -39.43) * mm, "end": v(-3.06, -38.65) * mm});
            skLineSegment(sketch, "E894", {"start": v(-3.06, -38.65) * mm, "end": v(-3.51, -37.92) * mm});
            skLineSegment(sketch, "E895", {"start": v(-3.51, -37.92) * mm, "end": v(-4.14, -37.26) * mm});
            skLineSegment(sketch, "E896", {"start": v(-1.6, -38.11) * mm, "end": v(-1.67, -38.2) * mm});
            skLineSegment(sketch, "E897", {"start": v(-1.67, -38.2) * mm, "end": v(-1.84, -38.42) * mm});
            skLineSegment(sketch, "E898", {"start": v(-1.84, -38.42) * mm, "end": v(-2.08, -38.77) * mm});
            skLineSegment(sketch, "E899", {"start": v(-2.08, -38.77) * mm, "end": v(-2.33, -39.22) * mm});
            skLineSegment(sketch, "E900", {"start": v(-2.33, -39.22) * mm, "end": v(-2.56, -39.77) * mm});
            skLineSegment(sketch, "E901", {"start": v(-2.56, -39.77) * mm, "end": v(-2.72, -40.4) * mm});
            skLineSegment(sketch, "E902", {"start": v(-2.72, -40.4) * mm, "end": v(-2.77, -41.08) * mm});
            skLineSegment(sketch, "E903", {"start": v(-2.77, -41.08) * mm, "end": v(-2.65, -41.8) * mm});
            skLineSegment(sketch, "E904", {"start": v(-2.65, -41.8) * mm, "end": v(-2.58, -42.02) * mm});
            skLineSegment(sketch, "E905", {"start": v(-2.58, -42.02) * mm, "end": v(-2.51, -42.23) * mm});
            skLineSegment(sketch, "E906", {"start": v(-2.51, -42.23) * mm, "end": v(-2.44, -42.42) * mm});
            skLineSegment(sketch, "E907", {"start": v(-2.44, -42.42) * mm, "end": v(-2.36, -42.6) * mm});
            skLineSegment(sketch, "E908", {"start": v(-2.36, -42.6) * mm, "end": v(-2.29, -42.74) * mm});
            skLineSegment(sketch, "E909", {"start": v(-2.29, -42.74) * mm, "end": v(-2.21, -42.88) * mm});
            skLineSegment(sketch, "E910", {"start": v(-2.21, -42.88) * mm, "end": v(-2.13, -43) * mm});
            skLineSegment(sketch, "E911", {"start": v(-2.13, -43) * mm, "end": v(-2.06, -43.1) * mm});
            skLineSegment(sketch, "E912", {"start": v(-2.06, -43.1) * mm, "end": v(-1.98, -43.19) * mm});
            skLineSegment(sketch, "E913", {"start": v(-1.98, -43.19) * mm, "end": v(-1.9, -43.27) * mm});
            skLineSegment(sketch, "E914", {"start": v(-1.9, -43.27) * mm, "end": v(-1.81, -43.34) * mm});
            skLineSegment(sketch, "E915", {"start": v(-1.81, -43.34) * mm, "end": v(-1.72, -43.4) * mm});
            skLineSegment(sketch, "E916", {"start": v(-1.72, -43.4) * mm, "end": v(-1.61, -43.44) * mm});
            skLineSegment(sketch, "E917", {"start": v(-1.61, -43.44) * mm, "end": v(-1.5, -43.47) * mm});
            skLineSegment(sketch, "E918", {"start": v(-1.5, -43.47) * mm, "end": v(-1.35, -43.5) * mm});
            skLineSegment(sketch, "E919", {"start": v(-1.35, -43.5) * mm, "end": v(-1.19, -43.5) * mm});
            skLineSegment(sketch, "E920", {"start": v(-1.19, -43.5) * mm, "end": v(-1.02, -43.49) * mm});
            skLineSegment(sketch, "E921", {"start": v(-1.02, -43.49) * mm, "end": v(-0.88, -43.45) * mm});
            skLineSegment(sketch, "E922", {"start": v(-0.88, -43.45) * mm, "end": v(-0.76, -43.4) * mm});
            skLineSegment(sketch, "E923", {"start": v(-0.76, -43.4) * mm, "end": v(-0.66, -43.33) * mm});
            skLineSegment(sketch, "E924", {"start": v(-0.66, -43.33) * mm, "end": v(-0.59, -43.25) * mm});
            skLineSegment(sketch, "E925", {"start": v(-0.59, -43.25) * mm, "end": v(-0.53, -43.18) * mm});
            skLineSegment(sketch, "E926", {"start": v(-0.53, -43.18) * mm, "end": v(-0.48, -43.1) * mm});
            skLineSegment(sketch, "E927", {"start": v(-0.48, -43.1) * mm, "end": v(-0.45, -43.05) * mm});
            skLineSegment(sketch, "E928", {"start": v(-0.45, -43.05) * mm, "end": v(-0.31, -42.6) * mm});
            skLineSegment(sketch, "E929", {"start": v(-0.31, -42.6) * mm, "end": v(-0.21, -42.04) * mm});
            skLineSegment(sketch, "E930", {"start": v(-0.21, -42.04) * mm, "end": v(-0.17, -41.4) * mm});
            skLineSegment(sketch, "E931", {"start": v(-0.17, -41.4) * mm, "end": v(-0.22, -40.72) * mm});
            skLineSegment(sketch, "E932", {"start": v(-0.22, -40.72) * mm, "end": v(-0.36, -40.02) * mm});
            skLineSegment(sketch, "E933", {"start": v(-0.36, -40.02) * mm, "end": v(-0.63, -39.33) * mm});
            skLineSegment(sketch, "E934", {"start": v(-0.63, -39.33) * mm, "end": v(-1.03, -38.69) * mm});
            skLineSegment(sketch, "E935", {"start": v(-1.03, -38.69) * mm, "end": v(-1.6, -38.11) * mm});
            skLineSegment(sketch, "E936", {"start": v(7.93, -41.69) * mm, "end": v(8.28, -42.08) * mm});
            skLineSegment(sketch, "E937", {"start": v(8.28, -42.08) * mm, "end": v(8.72, -42.34) * mm});
            skLineSegment(sketch, "E938", {"start": v(8.72, -42.34) * mm, "end": v(9.21, -42.49) * mm});
            skLineSegment(sketch, "E939", {"start": v(9.21, -42.49) * mm, "end": v(9.72, -42.55) * mm});
            skLineSegment(sketch, "E940", {"start": v(9.72, -42.55) * mm, "end": v(10.18, -42.56) * mm});
            skLineSegment(sketch, "E941", {"start": v(10.18, -42.56) * mm, "end": v(10.57, -42.53) * mm});
            skLineSegment(sketch, "E942", {"start": v(10.57, -42.53) * mm, "end": v(10.83, -42.49) * mm});
            skLineSegment(sketch, "E943", {"start": v(10.83, -42.49) * mm, "end": v(10.93, -42.47) * mm});
            skLineSegment(sketch, "E944", {"start": v(10.93, -42.47) * mm, "end": v(11.84, -40.75) * mm});
            skLineSegment(sketch, "E945", {"start": v(11.84, -40.75) * mm, "end": v(12.29, -39.1) * mm});
            skLineSegment(sketch, "E946", {"start": v(12.29, -39.1) * mm, "end": v(12.37, -37.56) * mm});
            skLineSegment(sketch, "E947", {"start": v(12.37, -37.56) * mm, "end": v(12.19, -36.2) * mm});
            skLineSegment(sketch, "E948", {"start": v(12.19, -36.2) * mm, "end": v(11.86, -35.05) * mm});
            skLineSegment(sketch, "E949", {"start": v(11.86, -35.05) * mm, "end": v(11.5, -34.17) * mm});
            skLineSegment(sketch, "E950", {"start": v(11.5, -34.17) * mm, "end": v(11.2, -33.6) * mm});
            skLineSegment(sketch, "E951", {"start": v(11.2, -33.6) * mm, "end": v(11.08, -33.4) * mm});
            skLineSegment(sketch, "E952", {"start": v(11.08, -33.4) * mm, "end": v(11.02, -33.53) * mm});
            skLineSegment(sketch, "E953", {"start": v(11.02, -33.53) * mm, "end": v(10.86, -33.9) * mm});
            skLineSegment(sketch, "E954", {"start": v(10.86, -33.9) * mm, "end": v(10.6, -34.41) * mm});
            skLineSegment(sketch, "E955", {"start": v(10.6, -34.41) * mm, "end": v(10.24, -35.04) * mm});
            skLineSegment(sketch, "E956", {"start": v(10.24, -35.04) * mm, "end": v(9.8, -35.72) * mm});
            skLineSegment(sketch, "E957", {"start": v(9.8, -35.72) * mm, "end": v(9.3, -36.4) * mm});
            skLineSegment(sketch, "E958", {"start": v(9.3, -36.4) * mm, "end": v(8.72, -37) * mm});
            skLineSegment(sketch, "E959", {"start": v(8.72, -37) * mm, "end": v(8.1, -37.47) * mm});
            skLineSegment(sketch, "E960", {"start": v(8.1, -37.47) * mm, "end": v(7.6, -37.96) * mm});
            skLineSegment(sketch, "E961", {"start": v(7.6, -37.96) * mm, "end": v(7.35, -38.58) * mm});
            skLineSegment(sketch, "E962", {"start": v(7.35, -38.58) * mm, "end": v(7.3, -39.27) * mm});
            skLineSegment(sketch, "E963", {"start": v(7.3, -39.27) * mm, "end": v(7.37, -39.97) * mm});
            skLineSegment(sketch, "E964", {"start": v(7.37, -39.97) * mm, "end": v(7.53, -40.63) * mm});
            skLineSegment(sketch, "E965", {"start": v(7.53, -40.63) * mm, "end": v(7.72, -41.17) * mm});
            skLineSegment(sketch, "E966", {"start": v(7.72, -41.17) * mm, "end": v(7.87, -41.55) * mm});
            skLineSegment(sketch, "E967", {"start": v(7.87, -41.55) * mm, "end": v(7.93, -41.69) * mm});
            skLineSegment(sketch, "E968", {"start": v(6.96, -34.49) * mm, "end": v(7.07, -34.65) * mm});
            skLineSegment(sketch, "E969", {"start": v(7.07, -34.65) * mm, "end": v(7.34, -35.1) * mm});
            skLineSegment(sketch, "E970", {"start": v(7.34, -35.1) * mm, "end": v(7.69, -35.85) * mm});
            skLineSegment(sketch, "E971", {"start": v(7.69, -35.85) * mm, "end": v(8.03, -36.85) * mm});
            skLineSegment(sketch, "E972", {"start": v(8.03, -36.85) * mm, "end": v(8.29, -38.08) * mm});
            skLineSegment(sketch, "E973", {"start": v(8.29, -38.08) * mm, "end": v(8.37, -39.54) * mm});
            skLineSegment(sketch, "E974", {"start": v(8.37, -39.54) * mm, "end": v(8.21, -41.19) * mm});
            skLineSegment(sketch, "E975", {"start": v(8.21, -41.19) * mm, "end": v(7.71, -43.02) * mm});
            skLineSegment(sketch, "E976", {"start": v(7.71, -43.02) * mm, "end": v(7.69, -43.06) * mm});
            skLineSegment(sketch, "E977", {"start": v(7.69, -43.06) * mm, "end": v(7.62, -43.14) * mm});
            skLineSegment(sketch, "E978", {"start": v(7.62, -43.14) * mm, "end": v(7.5, -43.22) * mm});
            skLineSegment(sketch, "E979", {"start": v(7.5, -43.22) * mm, "end": v(7.36, -43.32) * mm});
            skLineSegment(sketch, "E980", {"start": v(7.36, -43.32) * mm, "end": v(7.17, -43.4) * mm});
            skLineSegment(sketch, "E981", {"start": v(7.17, -43.4) * mm, "end": v(6.92, -43.47) * mm});
            skLineSegment(sketch, "E982", {"start": v(6.92, -43.47) * mm, "end": v(6.64, -43.5) * mm});
            skLineSegment(sketch, "E983", {"start": v(6.64, -43.5) * mm, "end": v(6.3, -43.5) * mm});
            skLineSegment(sketch, "E984", {"start": v(6.3, -43.5) * mm, "end": v(6.08, -43.45) * mm});
            skLineSegment(sketch, "E985", {"start": v(6.08, -43.45) * mm, "end": v(5.88, -43.4) * mm});
            skLineSegment(sketch, "E986", {"start": v(5.88, -43.4) * mm, "end": v(5.7, -43.33) * mm});
            skLineSegment(sketch, "E987", {"start": v(5.7, -43.33) * mm, "end": v(5.56, -43.24) * mm});
            skLineSegment(sketch, "E988", {"start": v(5.56, -43.24) * mm, "end": v(5.43, -43.16) * mm});
            skLineSegment(sketch, "E989", {"start": v(5.43, -43.16) * mm, "end": v(5.33, -43.07) * mm});
            skLineSegment(sketch, "E990", {"start": v(5.33, -43.07) * mm, "end": v(5.26, -43) * mm});
            skLineSegment(sketch, "E991", {"start": v(5.26, -43) * mm, "end": v(5.22, -42.92) * mm});
            skLineSegment(sketch, "E992", {"start": v(5.22, -42.92) * mm, "end": v(4.98, -42.2) * mm});
            skLineSegment(sketch, "E993", {"start": v(4.98, -42.2) * mm, "end": v(4.86, -41.2) * mm});
            skLineSegment(sketch, "E994", {"start": v(4.86, -41.2) * mm, "end": v(4.85, -40) * mm});
            skLineSegment(sketch, "E995", {"start": v(4.85, -40) * mm, "end": v(4.98, -38.72) * mm});
            skLineSegment(sketch, "E996", {"start": v(4.98, -38.72) * mm, "end": v(5.24, -37.43) * mm});
            skLineSegment(sketch, "E997", {"start": v(5.24, -37.43) * mm, "end": v(5.66, -36.23) * mm});
            skLineSegment(sketch, "E998", {"start": v(5.66, -36.23) * mm, "end": v(6.23, -35.22) * mm});
            skLineSegment(sketch, "E999", {"start": v(6.23, -35.22) * mm, "end": v(6.96, -34.49) * mm});
            skLineSegment(sketch, "E1000", {"start": v(3.8, -37.26) * mm, "end": v(3.87, -37.35) * mm});
            skLineSegment(sketch, "E1001", {"start": v(3.87, -37.35) * mm, "end": v(4.06, -37.6) * mm});
            skLineSegment(sketch, "E1002", {"start": v(4.06, -37.6) * mm, "end": v(4.32, -38.01) * mm});
            skLineSegment(sketch, "E1003", {"start": v(4.32, -38.01) * mm, "end": v(4.6, -38.55) * mm});
            skLineSegment(sketch, "E1004", {"start": v(4.6, -38.55) * mm, "end": v(4.85, -39.18) * mm});
            skLineSegment(sketch, "E1005", {"start": v(4.85, -39.18) * mm, "end": v(5.03, -39.9) * mm});
            skLineSegment(sketch, "E1006", {"start": v(5.03, -39.9) * mm, "end": v(5.08, -40.7) * mm});
            skLineSegment(sketch, "E1007", {"start": v(5.08, -40.7) * mm, "end": v(4.95, -41.52) * mm});
            skLineSegment(sketch, "E1008", {"start": v(4.95, -41.52) * mm, "end": v(4.87, -41.81) * mm});
            skLineSegment(sketch, "E1009", {"start": v(4.87, -41.81) * mm, "end": v(4.8, -42.06) * mm});
            skLineSegment(sketch, "E1010", {"start": v(4.8, -42.06) * mm, "end": v(4.72, -42.28) * mm});
            skLineSegment(sketch, "E1011", {"start": v(4.72, -42.28) * mm, "end": v(4.64, -42.47) * mm});
            skLineSegment(sketch, "E1012", {"start": v(4.64, -42.47) * mm, "end": v(4.57, -42.63) * mm});
            skLineSegment(sketch, "E1013", {"start": v(4.57, -42.63) * mm, "end": v(4.49, -42.78) * mm});
            skLineSegment(sketch, "E1014", {"start": v(4.49, -42.78) * mm, "end": v(4.4, -42.9) * mm});
            skLineSegment(sketch, "E1015", {"start": v(4.4, -42.9) * mm, "end": v(4.3, -43.01) * mm});
            skLineSegment(sketch, "E1016", {"start": v(4.3, -43.01) * mm, "end": v(4.16, -43.18) * mm});
            skLineSegment(sketch, "E1017", {"start": v(4.16, -43.18) * mm, "end": v(4.02, -43.3) * mm});
            skLineSegment(sketch, "E1018", {"start": v(4.02, -43.3) * mm, "end": v(3.9, -43.38) * mm});
            skLineSegment(sketch, "E1019", {"start": v(3.9, -43.38) * mm, "end": v(3.78, -43.44) * mm});
            skLineSegment(sketch, "E1020", {"start": v(3.78, -43.44) * mm, "end": v(3.67, -43.48) * mm});
            skLineSegment(sketch, "E1021", {"start": v(3.67, -43.48) * mm, "end": v(3.54, -43.5) * mm});
            skLineSegment(sketch, "E1022", {"start": v(3.54, -43.5) * mm, "end": v(3.4, -43.5) * mm});
            skLineSegment(sketch, "E1023", {"start": v(3.4, -43.5) * mm, "end": v(3.22, -43.5) * mm});
            skLineSegment(sketch, "E1024", {"start": v(3.22, -43.5) * mm, "end": v(3.1, -43.49) * mm});
            skLineSegment(sketch, "E1025", {"start": v(3.1, -43.49) * mm, "end": v(3, -43.44) * mm});
            skLineSegment(sketch, "E1026", {"start": v(3, -43.44) * mm, "end": v(2.88, -43.38) * mm});
            skLineSegment(sketch, "E1027", {"start": v(2.88, -43.38) * mm, "end": v(2.78, -43.3) * mm});
            skLineSegment(sketch, "E1028", {"start": v(2.78, -43.3) * mm, "end": v(2.7, -43.2) * mm});
            skLineSegment(sketch, "E1029", {"start": v(2.7, -43.2) * mm, "end": v(2.61, -43.08) * mm});
            skLineSegment(sketch, "E1030", {"start": v(2.61, -43.08) * mm, "end": v(2.54, -42.97) * mm});
            skLineSegment(sketch, "E1031", {"start": v(2.54, -42.97) * mm, "end": v(2.49, -42.85) * mm});
            skLineSegment(sketch, "E1032", {"start": v(2.49, -42.85) * mm, "end": v(2.33, -42.34) * mm});
            skLineSegment(sketch, "E1033", {"start": v(2.33, -42.34) * mm, "end": v(2.22, -41.7) * mm});
            skLineSegment(sketch, "E1034", {"start": v(2.22, -41.7) * mm, "end": v(2.19, -41) * mm});
            skLineSegment(sketch, "E1035", {"start": v(2.19, -41) * mm, "end": v(2.25, -40.22) * mm});
            skLineSegment(sketch, "E1036", {"start": v(2.25, -40.22) * mm, "end": v(2.41, -39.43) * mm});
            skLineSegment(sketch, "E1037", {"start": v(2.41, -39.43) * mm, "end": v(2.72, -38.65) * mm});
            skLineSegment(sketch, "E1038", {"start": v(2.72, -38.65) * mm, "end": v(3.17, -37.92) * mm});
            skLineSegment(sketch, "E1039", {"start": v(3.17, -37.92) * mm, "end": v(3.8, -37.26) * mm});
            skLineSegment(sketch, "E1040", {"start": v(1.25, -38.11) * mm, "end": v(1.32, -38.2) * mm});
            skLineSegment(sketch, "E1041", {"start": v(1.32, -38.2) * mm, "end": v(1.5, -38.42) * mm});
            skLineSegment(sketch, "E1042", {"start": v(1.5, -38.42) * mm, "end": v(1.73, -38.77) * mm});
            skLineSegment(sketch, "E1043", {"start": v(1.73, -38.77) * mm, "end": v(1.99, -39.22) * mm});
            skLineSegment(sketch, "E1044", {"start": v(1.99, -39.22) * mm, "end": v(2.22, -39.77) * mm});
            skLineSegment(sketch, "E1045", {"start": v(2.22, -39.77) * mm, "end": v(2.38, -40.4) * mm});
            skLineSegment(sketch, "E1046", {"start": v(2.38, -40.4) * mm, "end": v(2.42, -41.08) * mm});
            skLineSegment(sketch, "E1047", {"start": v(2.42, -41.08) * mm, "end": v(2.3, -41.8) * mm});
            skLineSegment(sketch, "E1048", {"start": v(2.3, -41.8) * mm, "end": v(2.24, -42.02) * mm});
            skLineSegment(sketch, "E1049", {"start": v(2.24, -42.02) * mm, "end": v(2.17, -42.23) * mm});
            skLineSegment(sketch, "E1050", {"start": v(2.17, -42.23) * mm, "end": v(2.1, -42.42) * mm});
            skLineSegment(sketch, "E1051", {"start": v(2.1, -42.42) * mm, "end": v(2.02, -42.6) * mm});
            skLineSegment(sketch, "E1052", {"start": v(2.02, -42.6) * mm, "end": v(1.94, -42.74) * mm});
            skLineSegment(sketch, "E1053", {"start": v(1.94, -42.74) * mm, "end": v(1.87, -42.88) * mm});
            skLineSegment(sketch, "E1054", {"start": v(1.87, -42.88) * mm, "end": v(1.79, -43) * mm});
            skLineSegment(sketch, "E1055", {"start": v(1.79, -43) * mm, "end": v(1.71, -43.1) * mm});
            skLineSegment(sketch, "E1056", {"start": v(1.71, -43.1) * mm, "end": v(1.63, -43.19) * mm});
            skLineSegment(sketch, "E1057", {"start": v(1.63, -43.19) * mm, "end": v(1.55, -43.27) * mm});
            skLineSegment(sketch, "E1058", {"start": v(1.55, -43.27) * mm, "end": v(1.47, -43.34) * mm});
            skLineSegment(sketch, "E1059", {"start": v(1.47, -43.34) * mm, "end": v(1.37, -43.4) * mm});
            skLineSegment(sketch, "E1060", {"start": v(1.37, -43.4) * mm, "end": v(1.27, -43.44) * mm});
            skLineSegment(sketch, "E1061", {"start": v(1.27, -43.44) * mm, "end": v(1.14, -43.47) * mm});
            skLineSegment(sketch, "E1062", {"start": v(1.14, -43.47) * mm, "end": v(1, -43.5) * mm});
            skLineSegment(sketch, "E1063", {"start": v(1, -43.5) * mm, "end": v(0.84, -43.5) * mm});
            skLineSegment(sketch, "E1064", {"start": v(0.84, -43.5) * mm, "end": v(0.68, -43.49) * mm});
            skLineSegment(sketch, "E1065", {"start": v(0.68, -43.49) * mm, "end": v(0.53, -43.45) * mm});
            skLineSegment(sketch, "E1066", {"start": v(0.53, -43.45) * mm, "end": v(0.42, -43.4) * mm});
            skLineSegment(sketch, "E1067", {"start": v(0.42, -43.4) * mm, "end": v(0.32, -43.33) * mm});
            skLineSegment(sketch, "E1068", {"start": v(0.32, -43.33) * mm, "end": v(0.24, -43.25) * mm});
            skLineSegment(sketch, "E1069", {"start": v(0.24, -43.25) * mm, "end": v(0.18, -43.18) * mm});
            skLineSegment(sketch, "E1070", {"start": v(0.18, -43.18) * mm, "end": v(0.14, -43.1) * mm});
            skLineSegment(sketch, "E1071", {"start": v(0.14, -43.1) * mm, "end": v(0.1, -43.05) * mm});
            skLineSegment(sketch, "E1072", {"start": v(0.1, -43.05) * mm, "end": v(-0.04, -42.6) * mm});
            skLineSegment(sketch, "E1073", {"start": v(-0.04, -42.6) * mm, "end": v(-0.14, -42.04) * mm});
            skLineSegment(sketch, "E1074", {"start": v(-0.14, -42.04) * mm, "end": v(-0.17, -41.4) * mm});
            skLineSegment(sketch, "E1075", {"start": v(-0.17, -41.4) * mm, "end": v(-0.13, -40.72) * mm});
            skLineSegment(sketch, "E1076", {"start": v(-0.13, -40.72) * mm, "end": v(0.02, -40.02) * mm});
            skLineSegment(sketch, "E1077", {"start": v(0.02, -40.02) * mm, "end": v(0.28, -39.33) * mm});
            skLineSegment(sketch, "E1078", {"start": v(0.28, -39.33) * mm, "end": v(0.69, -38.69) * mm});
            skLineSegment(sketch, "E1079", {"start": v(0.69, -38.69) * mm, "end": v(1.25, -38.11) * mm});
            skLineSegment(sketch, "E1080", {"start": v(-0.05, 39.46) * mm, "end": v(0.17, 39.39) * mm});
            skLineSegment(sketch, "E1081", {"start": v(0.17, 39.39) * mm, "end": v(0.33, 39.19) * mm});
            skLineSegment(sketch, "E1082", {"start": v(0.33, 39.19) * mm, "end": v(0.43, 38.88) * mm});
            skLineSegment(sketch, "E1083", {"start": v(0.43, 38.88) * mm, "end": v(0.5, 38.48) * mm});
            skLineSegment(sketch, "E1084", {"start": v(0.5, 38.48) * mm, "end": v(0.53, 38.02) * mm});
            skLineSegment(sketch, "E1085", {"start": v(0.53, 38.02) * mm, "end": v(0.56, 37.51) * mm});
            skLineSegment(sketch, "E1086", {"start": v(0.56, 37.51) * mm, "end": v(0.58, 36.98) * mm});
            skLineSegment(sketch, "E1087", {"start": v(0.58, 36.98) * mm, "end": v(0.62, 36.45) * mm});
            skLineSegment(sketch, "E1088", {"start": v(0.62, 36.45) * mm, "end": v(0.69, 35.95) * mm});
            skLineSegment(sketch, "E1089", {"start": v(0.69, 35.95) * mm, "end": v(0.8, 35.49) * mm});
            skLineSegment(sketch, "E1090", {"start": v(0.8, 35.49) * mm, "end": v(0.97, 35.07) * mm});
            skLineSegment(sketch, "E1091", {"start": v(0.97, 35.07) * mm, "end": v(1.17, 34.71) * mm});
            skLineSegment(sketch, "E1092", {"start": v(1.17, 34.71) * mm, "end": v(1.42, 34.41) * mm});
            skLineSegment(sketch, "E1093", {"start": v(1.42, 34.41) * mm, "end": v(1.72, 34.18) * mm});
            skLineSegment(sketch, "E1094", {"start": v(1.72, 34.18) * mm, "end": v(2.07, 34.02) * mm});
            skLineSegment(sketch, "E1095", {"start": v(2.07, 34.02) * mm, "end": v(2.47, 33.93) * mm});
            skLineSegment(sketch, "E1096", {"start": v(2.47, 33.93) * mm, "end": v(2.86, 33.95) * mm});
            skLineSegment(sketch, "E1097", {"start": v(2.86, 33.95) * mm, "end": v(3.2, 34.04) * mm});
            skLineSegment(sketch, "E1098", {"start": v(3.2, 34.04) * mm, "end": v(3.47, 34.2) * mm});
            skLineSegment(sketch, "E1099", {"start": v(3.47, 34.2) * mm, "end": v(3.69, 34.38) * mm});
            skLineSegment(sketch, "E1100", {"start": v(3.69, 34.38) * mm, "end": v(3.86, 34.57) * mm});
            skLineSegment(sketch, "E1101", {"start": v(3.86, 34.57) * mm, "end": v(3.98, 34.73) * mm});
            skLineSegment(sketch, "E1102", {"start": v(3.98, 34.73) * mm, "end": v(4.04, 34.85) * mm});
            skLineSegment(sketch, "E1103", {"start": v(4.04, 34.85) * mm, "end": v(4.07, 34.9) * mm});
            skLineSegment(sketch, "E1104", {"start": v(4.07, 34.9) * mm, "end": v(3.49, 35.36) * mm});
            skLineSegment(sketch, "E1105", {"start": v(3.49, 35.36) * mm, "end": v(3.2, 35.88) * mm});
            skLineSegment(sketch, "E1106", {"start": v(3.2, 35.88) * mm, "end": v(3.15, 36.42) * mm});
            skLineSegment(sketch, "E1107", {"start": v(3.15, 36.42) * mm, "end": v(3.27, 36.96) * mm});
            skLineSegment(sketch, "E1108", {"start": v(3.27, 36.96) * mm, "end": v(3.5, 37.47) * mm});
            skLineSegment(sketch, "E1109", {"start": v(3.5, 37.47) * mm, "end": v(3.8, 37.9) * mm});
            skLineSegment(sketch, "E1110", {"start": v(3.8, 37.9) * mm, "end": v(4.08, 38.26) * mm});
            skLineSegment(sketch, "E1111", {"start": v(4.08, 38.26) * mm, "end": v(4.3, 38.5) * mm});
            skLineSegment(sketch, "E1112", {"start": v(4.3, 38.5) * mm, "end": v(4.49, 38.68) * mm});
            skLineSegment(sketch, "E1113", {"start": v(4.49, 38.68) * mm, "end": v(4.74, 38.92) * mm});
            skLineSegment(sketch, "E1114", {"start": v(4.74, 38.92) * mm, "end": v(5.04, 39.2) * mm});
            skLineSegment(sketch, "E1115", {"start": v(5.04, 39.2) * mm, "end": v(5.4, 39.48) * mm});
            skLineSegment(sketch, "E1116", {"start": v(5.4, 39.48) * mm, "end": v(5.8, 39.76) * mm});
            skLineSegment(sketch, "E1117", {"start": v(5.8, 39.76) * mm, "end": v(6.26, 40.03) * mm});
            skLineSegment(sketch, "E1118", {"start": v(6.26, 40.03) * mm, "end": v(6.76, 40.25) * mm});
            skLineSegment(sketch, "E1119", {"start": v(6.76, 40.25) * mm, "end": v(7.3, 40.42) * mm});
            skLineSegment(sketch, "E1120", {"start": v(7.3, 40.42) * mm, "end": v(7.79, 40.52) * mm});
            skLineSegment(sketch, "E1121", {"start": v(7.79, 40.52) * mm, "end": v(8.14, 40.53) * mm});
            skLineSegment(sketch, "E1122", {"start": v(8.14, 40.53) * mm, "end": v(8.38, 40.47) * mm});
            skLineSegment(sketch, "E1123", {"start": v(8.38, 40.47) * mm, "end": v(8.53, 40.36) * mm});
            skLineSegment(sketch, "E1124", {"start": v(8.53, 40.36) * mm, "end": v(8.6, 40.21) * mm});
            skLineSegment(sketch, "E1125", {"start": v(8.6, 40.21) * mm, "end": v(8.62, 40.05) * mm});
            skLineSegment(sketch, "E1126", {"start": v(8.62, 40.05) * mm, "end": v(8.6, 39.88) * mm});
            skLineSegment(sketch, "E1127", {"start": v(8.6, 39.88) * mm, "end": v(8.59, 39.73) * mm});
            skLineSegment(sketch, "E1128", {"start": v(8.59, 39.73) * mm, "end": v(8.62, 39.59) * mm});
            skLineSegment(sketch, "E1129", {"start": v(8.62, 39.59) * mm, "end": v(8.75, 39.47) * mm});
            skLineSegment(sketch, "E1130", {"start": v(8.75, 39.47) * mm, "end": v(8.94, 39.38) * mm});
            skLineSegment(sketch, "E1131", {"start": v(8.94, 39.38) * mm, "end": v(9.16, 39.34) * mm});
            skLineSegment(sketch, "E1132", {"start": v(9.16, 39.34) * mm, "end": v(9.4, 39.36) * mm});
            skLineSegment(sketch, "E1133", {"start": v(9.4, 39.36) * mm, "end": v(9.6, 39.47) * mm});
            skLineSegment(sketch, "E1134", {"start": v(9.6, 39.47) * mm, "end": v(9.75, 39.68) * mm});
            skLineSegment(sketch, "E1135", {"start": v(9.75, 39.68) * mm, "end": v(9.82, 40) * mm});
            skLineSegment(sketch, "E1136", {"start": v(9.82, 40) * mm, "end": v(9.82, 40.4) * mm});
            skLineSegment(sketch, "E1137", {"start": v(9.82, 40.4) * mm, "end": v(9.76, 40.8) * mm});
            skLineSegment(sketch, "E1138", {"start": v(9.76, 40.8) * mm, "end": v(9.64, 41.22) * mm});
            skLineSegment(sketch, "E1139", {"start": v(9.64, 41.22) * mm, "end": v(9.44, 41.63) * mm});
            skLineSegment(sketch, "E1140", {"start": v(9.44, 41.63) * mm, "end": v(9.17, 42.02) * mm});
            skLineSegment(sketch, "E1141", {"start": v(9.17, 42.02) * mm, "end": v(8.8, 42.38) * mm});
            skLineSegment(sketch, "E1142", {"start": v(8.8, 42.38) * mm, "end": v(8.33, 42.7) * mm});
            skLineSegment(sketch, "E1143", {"start": v(8.33, 42.7) * mm, "end": v(7.75, 42.94) * mm});
            skLineSegment(sketch, "E1144", {"start": v(7.75, 42.94) * mm, "end": v(7, 43.08) * mm});
            skLineSegment(sketch, "E1145", {"start": v(7, 43.08) * mm, "end": v(6.07, 43.05) * mm});
            skLineSegment(sketch, "E1146", {"start": v(6.07, 43.05) * mm, "end": v(5, 42.92) * mm});
            skLineSegment(sketch, "E1147", {"start": v(5, 42.92) * mm, "end": v(3.87, 42.71) * mm});
            skLineSegment(sketch, "E1148", {"start": v(3.87, 42.71) * mm, "end": v(2.74, 42.48) * mm});
            skLineSegment(sketch, "E1149", {"start": v(2.74, 42.48) * mm, "end": v(1.67, 42.26) * mm});
            skLineSegment(sketch, "E1150", {"start": v(1.67, 42.26) * mm, "end": v(0.72, 42.1) * mm});
            skLineSegment(sketch, "E1151", {"start": v(0.72, 42.1) * mm, "end": v(-0.05, 42.03) * mm});
            skLineSegment(sketch, "E1152", {"start": v(-0.05, 42.03) * mm, "end": v(-0.82, 42.1) * mm});
            skLineSegment(sketch, "E1153", {"start": v(-0.82, 42.1) * mm, "end": v(-1.77, 42.26) * mm});
            skLineSegment(sketch, "E1154", {"start": v(-1.77, 42.26) * mm, "end": v(-2.84, 42.48) * mm});
            skLineSegment(sketch, "E1155", {"start": v(-2.84, 42.48) * mm, "end": v(-3.97, 42.71) * mm});
            skLineSegment(sketch, "E1156", {"start": v(-3.97, 42.71) * mm, "end": v(-5.1, 42.92) * mm});
            skLineSegment(sketch, "E1157", {"start": v(-5.1, 42.92) * mm, "end": v(-6.17, 43.05) * mm});
            skLineSegment(sketch, "E1158", {"start": v(-6.17, 43.05) * mm, "end": v(-7.1, 43.08) * mm});
            skLineSegment(sketch, "E1159", {"start": v(-7.1, 43.08) * mm, "end": v(-7.85, 42.94) * mm});
            skLineSegment(sketch, "E1160", {"start": v(-7.85, 42.94) * mm, "end": v(-8.43, 42.7) * mm});
            skLineSegment(sketch, "E1161", {"start": v(-8.43, 42.7) * mm, "end": v(-8.9, 42.38) * mm});
            skLineSegment(sketch, "E1162", {"start": v(-8.9, 42.38) * mm, "end": v(-9.26, 42.02) * mm});
            skLineSegment(sketch, "E1163", {"start": v(-9.26, 42.02) * mm, "end": v(-9.54, 41.63) * mm});
            skLineSegment(sketch, "E1164", {"start": v(-9.54, 41.63) * mm, "end": v(-9.73, 41.22) * mm});
            skLineSegment(sketch, "E1165", {"start": v(-9.73, 41.22) * mm, "end": v(-9.86, 40.8) * mm});
            skLineSegment(sketch, "E1166", {"start": v(-9.86, 40.8) * mm, "end": v(-9.91, 40.4) * mm});
            skLineSegment(sketch, "E1167", {"start": v(-9.91, 40.4) * mm, "end": v(-9.92, 40) * mm});
            skLineSegment(sketch, "E1168", {"start": v(-9.92, 40) * mm, "end": v(-9.85, 39.68) * mm});
            skLineSegment(sketch, "E1169", {"start": v(-9.85, 39.68) * mm, "end": v(-9.7, 39.47) * mm});
            skLineSegment(sketch, "E1170", {"start": v(-9.7, 39.47) * mm, "end": v(-9.5, 39.36) * mm});
            skLineSegment(sketch, "E1171", {"start": v(-9.5, 39.36) * mm, "end": v(-9.26, 39.34) * mm});
            skLineSegment(sketch, "E1172", {"start": v(-9.26, 39.34) * mm, "end": v(-9.04, 39.38) * mm});
            skLineSegment(sketch, "E1173", {"start": v(-9.04, 39.38) * mm, "end": v(-8.85, 39.47) * mm});
            skLineSegment(sketch, "E1174", {"start": v(-8.85, 39.47) * mm, "end": v(-8.72, 39.59) * mm});
            skLineSegment(sketch, "E1175", {"start": v(-8.72, 39.59) * mm, "end": v(-8.68, 39.73) * mm});
            skLineSegment(sketch, "E1176", {"start": v(-8.68, 39.73) * mm, "end": v(-8.7, 39.88) * mm});
            skLineSegment(sketch, "E1177", {"start": v(-8.7, 39.88) * mm, "end": v(-8.72, 40.05) * mm});
            skLineSegment(sketch, "E1178", {"start": v(-8.72, 40.05) * mm, "end": v(-8.7, 40.21) * mm});
            skLineSegment(sketch, "E1179", {"start": v(-8.7, 40.21) * mm, "end": v(-8.62, 40.36) * mm});
            skLineSegment(sketch, "E1180", {"start": v(-8.62, 40.36) * mm, "end": v(-8.48, 40.47) * mm});
            skLineSegment(sketch, "E1181", {"start": v(-8.48, 40.47) * mm, "end": v(-8.24, 40.53) * mm});
            skLineSegment(sketch, "E1182", {"start": v(-8.24, 40.53) * mm, "end": v(-7.89, 40.52) * mm});
            skLineSegment(sketch, "E1183", {"start": v(-7.89, 40.52) * mm, "end": v(-7.4, 40.42) * mm});
            skLineSegment(sketch, "E1184", {"start": v(-7.4, 40.42) * mm, "end": v(-6.85, 40.25) * mm});
            skLineSegment(sketch, "E1185", {"start": v(-6.85, 40.25) * mm, "end": v(-6.35, 40.03) * mm});
            skLineSegment(sketch, "E1186", {"start": v(-6.35, 40.03) * mm, "end": v(-5.9, 39.76) * mm});
            skLineSegment(sketch, "E1187", {"start": v(-5.9, 39.76) * mm, "end": v(-5.5, 39.48) * mm});
            skLineSegment(sketch, "E1188", {"start": v(-5.5, 39.48) * mm, "end": v(-5.14, 39.2) * mm});
            skLineSegment(sketch, "E1189", {"start": v(-5.14, 39.2) * mm, "end": v(-4.83, 38.92) * mm});
            skLineSegment(sketch, "E1190", {"start": v(-4.83, 38.92) * mm, "end": v(-4.58, 38.68) * mm});
            skLineSegment(sketch, "E1191", {"start": v(-4.58, 38.68) * mm, "end": v(-4.4, 38.5) * mm});
            skLineSegment(sketch, "E1192", {"start": v(-4.4, 38.5) * mm, "end": v(-4.18, 38.26) * mm});
            skLineSegment(sketch, "E1193", {"start": v(-4.18, 38.26) * mm, "end": v(-3.9, 37.9) * mm});
            skLineSegment(sketch, "E1194", {"start": v(-3.9, 37.9) * mm, "end": v(-3.6, 37.47) * mm});
            skLineSegment(sketch, "E1195", {"start": v(-3.6, 37.47) * mm, "end": v(-3.37, 36.96) * mm});
            skLineSegment(sketch, "E1196", {"start": v(-3.37, 36.96) * mm, "end": v(-3.25, 36.42) * mm});
            skLineSegment(sketch, "E1197", {"start": v(-3.25, 36.42) * mm, "end": v(-3.3, 35.88) * mm});
            skLineSegment(sketch, "E1198", {"start": v(-3.3, 35.88) * mm, "end": v(-3.58, 35.36) * mm});
            skLineSegment(sketch, "E1199", {"start": v(-3.58, 35.36) * mm, "end": v(-4.17, 34.9) * mm});
            skLineSegment(sketch, "E1200", {"start": v(-4.17, 34.9) * mm, "end": v(-4.14, 34.85) * mm});
            skLineSegment(sketch, "E1201", {"start": v(-4.14, 34.85) * mm, "end": v(-4.07, 34.73) * mm});
            skLineSegment(sketch, "E1202", {"start": v(-4.07, 34.73) * mm, "end": v(-3.95, 34.57) * mm});
            skLineSegment(sketch, "E1203", {"start": v(-3.95, 34.57) * mm, "end": v(-3.79, 34.38) * mm});
            skLineSegment(sketch, "E1204", {"start": v(-3.79, 34.38) * mm, "end": v(-3.56, 34.2) * mm});
            skLineSegment(sketch, "E1205", {"start": v(-3.56, 34.2) * mm, "end": v(-3.29, 34.04) * mm});
            skLineSegment(sketch, "E1206", {"start": v(-3.29, 34.04) * mm, "end": v(-2.95, 33.95) * mm});
            skLineSegment(sketch, "E1207", {"start": v(-2.95, 33.95) * mm, "end": v(-2.56, 33.93) * mm});
            skLineSegment(sketch, "E1208", {"start": v(-2.56, 33.93) * mm, "end": v(-2.17, 34.02) * mm});
            skLineSegment(sketch, "E1209", {"start": v(-2.17, 34.02) * mm, "end": v(-1.82, 34.18) * mm});
            skLineSegment(sketch, "E1210", {"start": v(-1.82, 34.18) * mm, "end": v(-1.52, 34.41) * mm});
            skLineSegment(sketch, "E1211", {"start": v(-1.52, 34.41) * mm, "end": v(-1.27, 34.71) * mm});
            skLineSegment(sketch, "E1212", {"start": v(-1.27, 34.71) * mm, "end": v(-1.06, 35.07) * mm});
            skLineSegment(sketch, "E1213", {"start": v(-1.06, 35.07) * mm, "end": v(-0.9, 35.49) * mm});
            skLineSegment(sketch, "E1214", {"start": v(-0.9, 35.49) * mm, "end": v(-0.79, 35.95) * mm});
            skLineSegment(sketch, "E1215", {"start": v(-0.79, 35.95) * mm, "end": v(-0.72, 36.45) * mm});
            skLineSegment(sketch, "E1216", {"start": v(-0.72, 36.45) * mm, "end": v(-0.68, 36.98) * mm});
            skLineSegment(sketch, "E1217", {"start": v(-0.68, 36.98) * mm, "end": v(-0.65, 37.51) * mm});
            skLineSegment(sketch, "E1218", {"start": v(-0.65, 37.51) * mm, "end": v(-0.63, 38.02) * mm});
            skLineSegment(sketch, "E1219", {"start": v(-0.63, 38.02) * mm, "end": v(-0.6, 38.48) * mm});
            skLineSegment(sketch, "E1220", {"start": v(-0.6, 38.48) * mm, "end": v(-0.53, 38.88) * mm});
            skLineSegment(sketch, "E1221", {"start": v(-0.53, 38.88) * mm, "end": v(-0.43, 39.19) * mm});
            skLineSegment(sketch, "E1222", {"start": v(-0.43, 39.19) * mm, "end": v(-0.27, 39.39) * mm});
            skLineSegment(sketch, "E1223", {"start": v(-0.27, 39.39) * mm, "end": v(-0.05, 39.46) * mm});
            skLineSegment(sketch, "E1224", {"start": v(-37.92, 56.2) * mm, "end": v(-37.78, 56.47) * mm});
            skLineSegment(sketch, "E1225", {"start": v(-37.78, 56.47) * mm, "end": v(-37.27, 56.81) * mm});
            skLineSegment(sketch, "E1226", {"start": v(-37.27, 56.81) * mm, "end": v(-36.43, 57.2) * mm});
            skLineSegment(sketch, "E1227", {"start": v(-36.43, 57.2) * mm, "end": v(-35.3, 57.57) * mm});
            skLineSegment(sketch, "E1228", {"start": v(-35.3, 57.57) * mm, "end": v(-33.91, 57.89) * mm});
            skLineSegment(sketch, "E1229", {"start": v(-33.91, 57.89) * mm, "end": v(-32.3, 58.1) * mm});
            skLineSegment(sketch, "E1230", {"start": v(-32.3, 58.1) * mm, "end": v(-30.5, 58.17) * mm});
            skLineSegment(sketch, "E1231", {"start": v(-30.5, 58.17) * mm, "end": v(-28.56, 58.05) * mm});
            skLineSegment(sketch, "E1232", {"start": v(-28.56, 58.05) * mm, "end": v(-26.83, 57.71) * mm});
            skLineSegment(sketch, "E1233", {"start": v(-26.83, 57.71) * mm, "end": v(-25.24, 57.17) * mm});
            skLineSegment(sketch, "E1234", {"start": v(-25.24, 57.17) * mm, "end": v(-23.78, 56.48) * mm});
            skLineSegment(sketch, "E1235", {"start": v(-23.78, 56.48) * mm, "end": v(-22.45, 55.7) * mm});
            skLineSegment(sketch, "E1236", {"start": v(-22.45, 55.7) * mm, "end": v(-21.22, 54.88) * mm});
            skLineSegment(sketch, "E1237", {"start": v(-21.22, 54.88) * mm, "end": v(-20.1, 54.08) * mm});
            skLineSegment(sketch, "E1238", {"start": v(-20.1, 54.08) * mm, "end": v(-19.07, 53.37) * mm});
            skLineSegment(sketch, "E1239", {"start": v(-19.07, 53.37) * mm, "end": v(-18.12, 52.8) * mm});
            skLineSegment(sketch, "E1240", {"start": v(-18.12, 52.8) * mm, "end": v(-17.27, 52.39) * mm});
            skLineSegment(sketch, "E1241", {"start": v(-17.27, 52.39) * mm, "end": v(-16.29, 52) * mm});
            skLineSegment(sketch, "E1242", {"start": v(-16.29, 52) * mm, "end": v(-15.24, 51.67) * mm});
            skLineSegment(sketch, "E1243", {"start": v(-15.24, 51.67) * mm, "end": v(-14.15, 51.4) * mm});
            skLineSegment(sketch, "E1244", {"start": v(-14.15, 51.4) * mm, "end": v(-13.07, 51.2) * mm});
            skLineSegment(sketch, "E1245", {"start": v(-13.07, 51.2) * mm, "end": v(-12.03, 51.11) * mm});
            skLineSegment(sketch, "E1246", {"start": v(-12.03, 51.11) * mm, "end": v(-11.09, 51.13) * mm});
            skLineSegment(sketch, "E1247", {"start": v(-11.09, 51.13) * mm, "end": v(-10.28, 51.28) * mm});
            skLineSegment(sketch, "E1248", {"start": v(-10.28, 51.28) * mm, "end": v(-9.64, 51.39) * mm});
            skLineSegment(sketch, "E1249", {"start": v(-9.64, 51.39) * mm, "end": v(-9.17, 51.29) * mm});
            skLineSegment(sketch, "E1250", {"start": v(-9.17, 51.29) * mm, "end": v(-8.86, 51.04) * mm});
            skLineSegment(sketch, "E1251", {"start": v(-8.86, 51.04) * mm, "end": v(-8.69, 50.7) * mm});
            skLineSegment(sketch, "E1252", {"start": v(-8.69, 50.7) * mm, "end": v(-8.63, 50.3) * mm});
            skLineSegment(sketch, "E1253", {"start": v(-8.63, 50.3) * mm, "end": v(-8.68, 49.9) * mm});
            skLineSegment(sketch, "E1254", {"start": v(-8.68, 49.9) * mm, "end": v(-8.8, 49.56) * mm});
            skLineSegment(sketch, "E1255", {"start": v(-8.8, 49.56) * mm, "end": v(-9, 49.33) * mm});
            skLineSegment(sketch, "E1256", {"start": v(-9, 49.33) * mm, "end": v(-9.22, 49.2) * mm});
            skLineSegment(sketch, "E1257", {"start": v(-9.22, 49.2) * mm, "end": v(-9.44, 49.1) * mm});
            skLineSegment(sketch, "E1258", {"start": v(-9.44, 49.1) * mm, "end": v(-9.7, 49.04) * mm});
            skLineSegment(sketch, "E1259", {"start": v(-9.7, 49.04) * mm, "end": v(-10.02, 49.04) * mm});
            skLineSegment(sketch, "E1260", {"start": v(-10.02, 49.04) * mm, "end": v(-10.44, 49.1) * mm});
            skLineSegment(sketch, "E1261", {"start": v(-10.44, 49.1) * mm, "end": v(-10.99, 49.24) * mm});
            skLineSegment(sketch, "E1262", {"start": v(-10.99, 49.24) * mm, "end": v(-11.68, 49.45) * mm});
            skLineSegment(sketch, "E1263", {"start": v(-11.68, 49.45) * mm, "end": v(-12.57, 49.76) * mm});
            skLineSegment(sketch, "E1264", {"start": v(-12.57, 49.76) * mm, "end": v(-13, 49.9) * mm});
            skLineSegment(sketch, "E1265", {"start": v(-13, 49.9) * mm, "end": v(-13.47, 50.02) * mm});
            skLineSegment(sketch, "E1266", {"start": v(-13.47, 50.02) * mm, "end": v(-13.97, 50.13) * mm});
            skLineSegment(sketch, "E1267", {"start": v(-13.97, 50.13) * mm, "end": v(-14.5, 50.23) * mm});
            skLineSegment(sketch, "E1268", {"start": v(-14.5, 50.23) * mm, "end": v(-15.03, 50.32) * mm});
            skLineSegment(sketch, "E1269", {"start": v(-15.03, 50.32) * mm, "end": v(-15.58, 50.4) * mm});
            skLineSegment(sketch, "E1270", {"start": v(-15.58, 50.4) * mm, "end": v(-16.13, 50.48) * mm});
            skLineSegment(sketch, "E1271", {"start": v(-16.13, 50.48) * mm, "end": v(-16.69, 50.55) * mm});
            skLineSegment(sketch, "E1272", {"start": v(-16.69, 50.55) * mm, "end": v(-18.21, 50.65) * mm});
            skLineSegment(sketch, "E1273", {"start": v(-18.21, 50.65) * mm, "end": v(-19.72, 50.6) * mm});
            skLineSegment(sketch, "E1274", {"start": v(-19.72, 50.6) * mm, "end": v(-21.2, 50.45) * mm});
            skLineSegment(sketch, "E1275", {"start": v(-21.2, 50.45) * mm, "end": v(-22.63, 50.24) * mm});
            skLineSegment(sketch, "E1276", {"start": v(-22.63, 50.24) * mm, "end": v(-24, 50.02) * mm});
            skLineSegment(sketch, "E1277", {"start": v(-24, 50.02) * mm, "end": v(-25.29, 49.82) * mm});
            skLineSegment(sketch, "E1278", {"start": v(-25.29, 49.82) * mm, "end": v(-26.47, 49.68) * mm});
            skLineSegment(sketch, "E1279", {"start": v(-26.47, 49.68) * mm, "end": v(-27.54, 49.66) * mm});
            skLineSegment(sketch, "E1280", {"start": v(-27.54, 49.66) * mm, "end": v(-29.5, 49.84) * mm});
            skLineSegment(sketch, "E1281", {"start": v(-29.5, 49.84) * mm, "end": v(-31.3, 50.2) * mm});
            skLineSegment(sketch, "E1282", {"start": v(-31.3, 50.2) * mm, "end": v(-32.94, 50.75) * mm});
            skLineSegment(sketch, "E1283", {"start": v(-32.94, 50.75) * mm, "end": v(-34.38, 51.47) * mm});
            skLineSegment(sketch, "E1284", {"start": v(-34.38, 51.47) * mm, "end": v(-35.61, 52.37) * mm});
            skLineSegment(sketch, "E1285", {"start": v(-35.61, 52.37) * mm, "end": v(-36.63, 53.46) * mm});
            skLineSegment(sketch, "E1286", {"start": v(-36.63, 53.46) * mm, "end": v(-37.4, 54.74) * mm});
            skLineSegment(sketch, "E1287", {"start": v(-37.4, 54.74) * mm, "end": v(-37.92, 56.2) * mm});
            skLineSegment(sketch, "E1288", {"start": v(-28.76, 56.87) * mm, "end": v(-28.86, 56.9) * mm});
            skLineSegment(sketch, "E1289", {"start": v(-28.86, 56.9) * mm, "end": v(-29.15, 56.96) * mm});
            skLineSegment(sketch, "E1290", {"start": v(-29.15, 56.96) * mm, "end": v(-29.59, 57.04) * mm});
            skLineSegment(sketch, "E1291", {"start": v(-29.59, 57.04) * mm, "end": v(-30.12, 57.12) * mm});
            skLineSegment(sketch, "E1292", {"start": v(-30.12, 57.12) * mm, "end": v(-30.7, 57.17) * mm});
            skLineSegment(sketch, "E1293", {"start": v(-30.7, 57.17) * mm, "end": v(-31.3, 57.17) * mm});
            skLineSegment(sketch, "E1294", {"start": v(-31.3, 57.17) * mm, "end": v(-31.87, 57.1) * mm});
            skLineSegment(sketch, "E1295", {"start": v(-31.87, 57.1) * mm, "end": v(-32.36, 56.95) * mm});
            skLineSegment(sketch, "E1296", {"start": v(-32.36, 56.95) * mm, "end": v(-32.4, 56.7) * mm});
            skLineSegment(sketch, "E1297", {"start": v(-32.4, 56.7) * mm, "end": v(-32.44, 56.05) * mm});
            skLineSegment(sketch, "E1298", {"start": v(-32.44, 56.05) * mm, "end": v(-32.42, 55.1) * mm});
            skLineSegment(sketch, "E1299", {"start": v(-32.42, 55.1) * mm, "end": v(-32.25, 54) * mm});
            skLineSegment(sketch, "E1300", {"start": v(-32.25, 54) * mm, "end": v(-31.84, 52.86) * mm});
            skLineSegment(sketch, "E1301", {"start": v(-31.84, 52.86) * mm, "end": v(-31.1, 51.82) * mm});
            skLineSegment(sketch, "E1302", {"start": v(-31.1, 51.82) * mm, "end": v(-29.95, 51) * mm});
            skLineSegment(sketch, "E1303", {"start": v(-29.95, 51) * mm, "end": v(-28.32, 50.5) * mm});
            skLineSegment(sketch, "E1304", {"start": v(-28.32, 50.5) * mm, "end": v(-26.7, 50.46) * mm});
            skLineSegment(sketch, "E1305", {"start": v(-26.7, 50.46) * mm, "end": v(-25.42, 50.76) * mm});
            skLineSegment(sketch, "E1306", {"start": v(-25.42, 50.76) * mm, "end": v(-24.43, 51.3) * mm});
            skLineSegment(sketch, "E1307", {"start": v(-24.43, 51.3) * mm, "end": v(-23.69, 52) * mm});
            skLineSegment(sketch, "E1308", {"start": v(-23.69, 52) * mm, "end": v(-23.18, 52.7) * mm});
            skLineSegment(sketch, "E1309", {"start": v(-23.18, 52.7) * mm, "end": v(-22.85, 53.35) * mm});
            skLineSegment(sketch, "E1310", {"start": v(-22.85, 53.35) * mm, "end": v(-22.68, 53.8) * mm});
            skLineSegment(sketch, "E1311", {"start": v(-22.68, 53.8) * mm, "end": v(-22.63, 53.99) * mm});
            skLineSegment(sketch, "E1312", {"start": v(-22.63, 53.99) * mm, "end": v(-22.69, 54.07) * mm});
            skLineSegment(sketch, "E1313", {"start": v(-22.69, 54.07) * mm, "end": v(-22.86, 54.27) * mm});
            skLineSegment(sketch, "E1314", {"start": v(-22.86, 54.27) * mm, "end": v(-23.15, 54.55) * mm});
            skLineSegment(sketch, "E1315", {"start": v(-23.15, 54.55) * mm, "end": v(-23.55, 54.86) * mm});
            skLineSegment(sketch, "E1316", {"start": v(-23.55, 54.86) * mm, "end": v(-24.08, 55.14) * mm});
            skLineSegment(sketch, "E1317", {"start": v(-24.08, 55.14) * mm, "end": v(-24.74, 55.35) * mm});
            skLineSegment(sketch, "E1318", {"start": v(-24.74, 55.35) * mm, "end": v(-25.53, 55.43) * mm});
            skLineSegment(sketch, "E1319", {"start": v(-25.53, 55.43) * mm, "end": v(-26.46, 55.34) * mm});
            skLineSegment(sketch, "E1320", {"start": v(-26.46, 55.34) * mm, "end": v(-26.48, 55.31) * mm});
            skLineSegment(sketch, "E1321", {"start": v(-26.48, 55.31) * mm, "end": v(-26.53, 55.25) * mm});
            skLineSegment(sketch, "E1322", {"start": v(-26.53, 55.25) * mm, "end": v(-26.58, 55.15) * mm});
            skLineSegment(sketch, "E1323", {"start": v(-26.58, 55.15) * mm, "end": v(-26.61, 55.03) * mm});
            skLineSegment(sketch, "E1324", {"start": v(-26.61, 55.03) * mm, "end": v(-26.59, 54.91) * mm});
            skLineSegment(sketch, "E1325", {"start": v(-26.59, 54.91) * mm, "end": v(-26.48, 54.8) * mm});
            skLineSegment(sketch, "E1326", {"start": v(-26.48, 54.8) * mm, "end": v(-26.27, 54.7) * mm});
            skLineSegment(sketch, "E1327", {"start": v(-26.27, 54.7) * mm, "end": v(-25.93, 54.61) * mm});
            skLineSegment(sketch, "E1328", {"start": v(-25.93, 54.61) * mm, "end": v(-25.62, 54.5) * mm});
            skLineSegment(sketch, "E1329", {"start": v(-25.62, 54.5) * mm, "end": v(-25.5, 54.32) * mm});
            skLineSegment(sketch, "E1330", {"start": v(-25.5, 54.32) * mm, "end": v(-25.56, 54.09) * mm});
            skLineSegment(sketch, "E1331", {"start": v(-25.56, 54.09) * mm, "end": v(-25.76, 53.84) * mm});
            skLineSegment(sketch, "E1332", {"start": v(-25.76, 53.84) * mm, "end": v(-26.09, 53.6) * mm});
            skLineSegment(sketch, "E1333", {"start": v(-26.09, 53.6) * mm, "end": v(-26.5, 53.42) * mm});
            skLineSegment(sketch, "E1334", {"start": v(-26.5, 53.42) * mm, "end": v(-27, 53.31) * mm});
            skLineSegment(sketch, "E1335", {"start": v(-27, 53.31) * mm, "end": v(-27.53, 53.31) * mm});
            skLineSegment(sketch, "E1336", {"start": v(-27.53, 53.31) * mm, "end": v(-28, 53.43) * mm});
            skLineSegment(sketch, "E1337", {"start": v(-28, 53.43) * mm, "end": v(-28.45, 53.66) * mm});
            skLineSegment(sketch, "E1338", {"start": v(-28.45, 53.66) * mm, "end": v(-28.83, 53.99) * mm});
            skLineSegment(sketch, "E1339", {"start": v(-28.83, 53.99) * mm, "end": v(-29.12, 54.41) * mm});
            skLineSegment(sketch, "E1340", {"start": v(-29.12, 54.41) * mm, "end": v(-29.28, 54.92) * mm});
            skLineSegment(sketch, "E1341", {"start": v(-29.28, 54.92) * mm, "end": v(-29.3, 55.51) * mm});
            skLineSegment(sketch, "E1342", {"start": v(-29.3, 55.51) * mm, "end": v(-29.13, 56.16) * mm});
            skLineSegment(sketch, "E1343", {"start": v(-29.13, 56.16) * mm, "end": v(-28.76, 56.87) * mm});
            skLineSegment(sketch, "E1344", {"start": v(37.33, 56.2) * mm, "end": v(37.19, 56.47) * mm});
            skLineSegment(sketch, "E1345", {"start": v(37.19, 56.47) * mm, "end": v(36.68, 56.81) * mm});
            skLineSegment(sketch, "E1346", {"start": v(36.68, 56.81) * mm, "end": v(35.84, 57.2) * mm});
            skLineSegment(sketch, "E1347", {"start": v(35.84, 57.2) * mm, "end": v(34.7, 57.57) * mm});
            skLineSegment(sketch, "E1348", {"start": v(34.7, 57.57) * mm, "end": v(33.32, 57.89) * mm});
            skLineSegment(sketch, "E1349", {"start": v(33.32, 57.89) * mm, "end": v(31.7, 58.1) * mm});
            skLineSegment(sketch, "E1350", {"start": v(31.7, 58.1) * mm, "end": v(29.91, 58.17) * mm});
            skLineSegment(sketch, "E1351", {"start": v(29.91, 58.17) * mm, "end": v(27.97, 58.05) * mm});
            skLineSegment(sketch, "E1352", {"start": v(27.97, 58.05) * mm, "end": v(26.24, 57.71) * mm});
            skLineSegment(sketch, "E1353", {"start": v(26.24, 57.71) * mm, "end": v(24.65, 57.17) * mm});
            skLineSegment(sketch, "E1354", {"start": v(24.65, 57.17) * mm, "end": v(23.19, 56.48) * mm});
            skLineSegment(sketch, "E1355", {"start": v(23.19, 56.48) * mm, "end": v(21.85, 55.7) * mm});
            skLineSegment(sketch, "E1356", {"start": v(21.85, 55.7) * mm, "end": v(20.63, 54.88) * mm});
            skLineSegment(sketch, "E1357", {"start": v(20.63, 54.88) * mm, "end": v(19.5, 54.08) * mm});
            skLineSegment(sketch, "E1358", {"start": v(19.5, 54.08) * mm, "end": v(18.48, 53.37) * mm});
            skLineSegment(sketch, "E1359", {"start": v(18.48, 53.37) * mm, "end": v(17.53, 52.8) * mm});
            skLineSegment(sketch, "E1360", {"start": v(17.53, 52.8) * mm, "end": v(16.67, 52.39) * mm});
            skLineSegment(sketch, "E1361", {"start": v(16.67, 52.39) * mm, "end": v(15.7, 52) * mm});
            skLineSegment(sketch, "E1362", {"start": v(15.7, 52) * mm, "end": v(14.64, 51.67) * mm});
            skLineSegment(sketch, "E1363", {"start": v(14.64, 51.67) * mm, "end": v(13.55, 51.4) * mm});
            skLineSegment(sketch, "E1364", {"start": v(13.55, 51.4) * mm, "end": v(12.47, 51.2) * mm});
            skLineSegment(sketch, "E1365", {"start": v(12.47, 51.2) * mm, "end": v(11.44, 51.11) * mm});
            skLineSegment(sketch, "E1366", {"start": v(11.44, 51.11) * mm, "end": v(10.5, 51.13) * mm});
            skLineSegment(sketch, "E1367", {"start": v(10.5, 51.13) * mm, "end": v(9.69, 51.28) * mm});
            skLineSegment(sketch, "E1368", {"start": v(9.69, 51.28) * mm, "end": v(9.05, 51.39) * mm});
            skLineSegment(sketch, "E1369", {"start": v(9.05, 51.39) * mm, "end": v(8.58, 51.29) * mm});
            skLineSegment(sketch, "E1370", {"start": v(8.58, 51.29) * mm, "end": v(8.27, 51.04) * mm});
            skLineSegment(sketch, "E1371", {"start": v(8.27, 51.04) * mm, "end": v(8.1, 50.7) * mm});
            skLineSegment(sketch, "E1372", {"start": v(8.1, 50.7) * mm, "end": v(8.04, 50.3) * mm});
            skLineSegment(sketch, "E1373", {"start": v(8.04, 50.3) * mm, "end": v(8.09, 49.9) * mm});
            skLineSegment(sketch, "E1374", {"start": v(8.09, 49.9) * mm, "end": v(8.22, 49.56) * mm});
            skLineSegment(sketch, "E1375", {"start": v(8.22, 49.56) * mm, "end": v(8.41, 49.33) * mm});
            skLineSegment(sketch, "E1376", {"start": v(8.41, 49.33) * mm, "end": v(8.63, 49.2) * mm});
            skLineSegment(sketch, "E1377", {"start": v(8.63, 49.2) * mm, "end": v(8.85, 49.1) * mm});
            skLineSegment(sketch, "E1378", {"start": v(8.85, 49.1) * mm, "end": v(9.1, 49.04) * mm});
            skLineSegment(sketch, "E1379", {"start": v(9.1, 49.04) * mm, "end": v(9.43, 49.04) * mm});
            skLineSegment(sketch, "E1380", {"start": v(9.43, 49.04) * mm, "end": v(9.85, 49.1) * mm});
            skLineSegment(sketch, "E1381", {"start": v(9.85, 49.1) * mm, "end": v(10.4, 49.24) * mm});
            skLineSegment(sketch, "E1382", {"start": v(10.4, 49.24) * mm, "end": v(11.1, 49.45) * mm});
            skLineSegment(sketch, "E1383", {"start": v(11.1, 49.45) * mm, "end": v(11.97, 49.76) * mm});
            skLineSegment(sketch, "E1384", {"start": v(11.97, 49.76) * mm, "end": v(12.4, 49.9) * mm});
            skLineSegment(sketch, "E1385", {"start": v(12.4, 49.9) * mm, "end": v(12.88, 50.02) * mm});
            skLineSegment(sketch, "E1386", {"start": v(12.88, 50.02) * mm, "end": v(13.38, 50.13) * mm});
            skLineSegment(sketch, "E1387", {"start": v(13.38, 50.13) * mm, "end": v(13.9, 50.23) * mm});
            skLineSegment(sketch, "E1388", {"start": v(13.9, 50.23) * mm, "end": v(14.44, 50.32) * mm});
            skLineSegment(sketch, "E1389", {"start": v(14.44, 50.32) * mm, "end": v(14.98, 50.4) * mm});
            skLineSegment(sketch, "E1390", {"start": v(14.98, 50.4) * mm, "end": v(15.54, 50.48) * mm});
            skLineSegment(sketch, "E1391", {"start": v(15.54, 50.48) * mm, "end": v(16.1, 50.55) * mm});
            skLineSegment(sketch, "E1392", {"start": v(16.1, 50.55) * mm, "end": v(17.62, 50.65) * mm});
            skLineSegment(sketch, "E1393", {"start": v(17.62, 50.65) * mm, "end": v(19.13, 50.6) * mm});
            skLineSegment(sketch, "E1394", {"start": v(19.13, 50.6) * mm, "end": v(20.6, 50.45) * mm});
            skLineSegment(sketch, "E1395", {"start": v(20.6, 50.45) * mm, "end": v(22.04, 50.24) * mm});
            skLineSegment(sketch, "E1396", {"start": v(22.04, 50.24) * mm, "end": v(23.4, 50.02) * mm});
            skLineSegment(sketch, "E1397", {"start": v(23.4, 50.02) * mm, "end": v(24.7, 49.82) * mm});
            skLineSegment(sketch, "E1398", {"start": v(24.7, 49.82) * mm, "end": v(25.88, 49.68) * mm});
            skLineSegment(sketch, "E1399", {"start": v(25.88, 49.68) * mm, "end": v(26.95, 49.66) * mm});
            skLineSegment(sketch, "E1400", {"start": v(26.95, 49.66) * mm, "end": v(28.9, 49.84) * mm});
            skLineSegment(sketch, "E1401", {"start": v(28.9, 49.84) * mm, "end": v(30.71, 50.2) * mm});
            skLineSegment(sketch, "E1402", {"start": v(30.71, 50.2) * mm, "end": v(32.34, 50.75) * mm});
            skLineSegment(sketch, "E1403", {"start": v(32.34, 50.75) * mm, "end": v(33.78, 51.47) * mm});
            skLineSegment(sketch, "E1404", {"start": v(33.78, 51.47) * mm, "end": v(35.02, 52.37) * mm});
            skLineSegment(sketch, "E1405", {"start": v(35.02, 52.37) * mm, "end": v(36.03, 53.46) * mm});
            skLineSegment(sketch, "E1406", {"start": v(36.03, 53.46) * mm, "end": v(36.8, 54.74) * mm});
            skLineSegment(sketch, "E1407", {"start": v(36.8, 54.74) * mm, "end": v(37.33, 56.2) * mm});
            skLineSegment(sketch, "E1408", {"start": v(28.16, 56.87) * mm, "end": v(28.27, 56.9) * mm});
            skLineSegment(sketch, "E1409", {"start": v(28.27, 56.9) * mm, "end": v(28.56, 56.96) * mm});
            skLineSegment(sketch, "E1410", {"start": v(28.56, 56.96) * mm, "end": v(29, 57.04) * mm});
            skLineSegment(sketch, "E1411", {"start": v(29, 57.04) * mm, "end": v(29.52, 57.12) * mm});
            skLineSegment(sketch, "E1412", {"start": v(29.52, 57.12) * mm, "end": v(30.1, 57.17) * mm});
            skLineSegment(sketch, "E1413", {"start": v(30.1, 57.17) * mm, "end": v(30.7, 57.17) * mm});
            skLineSegment(sketch, "E1414", {"start": v(30.7, 57.17) * mm, "end": v(31.27, 57.1) * mm});
            skLineSegment(sketch, "E1415", {"start": v(31.27, 57.1) * mm, "end": v(31.77, 56.95) * mm});
            skLineSegment(sketch, "E1416", {"start": v(31.77, 56.95) * mm, "end": v(31.8, 56.7) * mm});
            skLineSegment(sketch, "E1417", {"start": v(31.8, 56.7) * mm, "end": v(31.85, 56.05) * mm});
            skLineSegment(sketch, "E1418", {"start": v(31.85, 56.05) * mm, "end": v(31.83, 55.1) * mm});
            skLineSegment(sketch, "E1419", {"start": v(31.83, 55.1) * mm, "end": v(31.66, 54) * mm});
            skLineSegment(sketch, "E1420", {"start": v(31.66, 54) * mm, "end": v(31.24, 52.86) * mm});
            skLineSegment(sketch, "E1421", {"start": v(31.24, 52.86) * mm, "end": v(30.5, 51.82) * mm});
            skLineSegment(sketch, "E1422", {"start": v(30.5, 51.82) * mm, "end": v(29.36, 51) * mm});
            skLineSegment(sketch, "E1423", {"start": v(29.36, 51) * mm, "end": v(27.72, 50.5) * mm});
            skLineSegment(sketch, "E1424", {"start": v(27.72, 50.5) * mm, "end": v(26.11, 50.46) * mm});
            skLineSegment(sketch, "E1425", {"start": v(26.11, 50.46) * mm, "end": v(24.83, 50.76) * mm});
            skLineSegment(sketch, "E1426", {"start": v(24.83, 50.76) * mm, "end": v(23.83, 51.3) * mm});
            skLineSegment(sketch, "E1427", {"start": v(23.83, 51.3) * mm, "end": v(23.1, 52) * mm});
            skLineSegment(sketch, "E1428", {"start": v(23.1, 52) * mm, "end": v(22.58, 52.7) * mm});
            skLineSegment(sketch, "E1429", {"start": v(22.58, 52.7) * mm, "end": v(22.26, 53.35) * mm});
            skLineSegment(sketch, "E1430", {"start": v(22.26, 53.35) * mm, "end": v(22.09, 53.8) * mm});
            skLineSegment(sketch, "E1431", {"start": v(22.09, 53.8) * mm, "end": v(22.04, 53.99) * mm});
            skLineSegment(sketch, "E1432", {"start": v(22.04, 53.99) * mm, "end": v(22.1, 54.07) * mm});
            skLineSegment(sketch, "E1433", {"start": v(22.1, 54.07) * mm, "end": v(22.26, 54.27) * mm});
            skLineSegment(sketch, "E1434", {"start": v(22.26, 54.27) * mm, "end": v(22.55, 54.55) * mm});
            skLineSegment(sketch, "E1435", {"start": v(22.55, 54.55) * mm, "end": v(22.96, 54.86) * mm});
            skLineSegment(sketch, "E1436", {"start": v(22.96, 54.86) * mm, "end": v(23.49, 55.14) * mm});
            skLineSegment(sketch, "E1437", {"start": v(23.49, 55.14) * mm, "end": v(24.15, 55.35) * mm});
            skLineSegment(sketch, "E1438", {"start": v(24.15, 55.35) * mm, "end": v(24.94, 55.43) * mm});
            skLineSegment(sketch, "E1439", {"start": v(24.94, 55.43) * mm, "end": v(25.86, 55.34) * mm});
            skLineSegment(sketch, "E1440", {"start": v(25.86, 55.34) * mm, "end": v(25.88, 55.31) * mm});
            skLineSegment(sketch, "E1441", {"start": v(25.88, 55.31) * mm, "end": v(25.94, 55.25) * mm});
            skLineSegment(sketch, "E1442", {"start": v(25.94, 55.25) * mm, "end": v(25.99, 55.15) * mm});
            skLineSegment(sketch, "E1443", {"start": v(25.99, 55.15) * mm, "end": v(26.02, 55.03) * mm});
            skLineSegment(sketch, "E1444", {"start": v(26.02, 55.03) * mm, "end": v(26, 54.91) * mm});
            skLineSegment(sketch, "E1445", {"start": v(26, 54.91) * mm, "end": v(25.9, 54.8) * mm});
            skLineSegment(sketch, "E1446", {"start": v(25.9, 54.8) * mm, "end": v(25.68, 54.7) * mm});
            skLineSegment(sketch, "E1447", {"start": v(25.68, 54.7) * mm, "end": v(25.34, 54.61) * mm});
            skLineSegment(sketch, "E1448", {"start": v(25.34, 54.61) * mm, "end": v(25.03, 54.5) * mm});
            skLineSegment(sketch, "E1449", {"start": v(25.03, 54.5) * mm, "end": v(24.92, 54.32) * mm});
            skLineSegment(sketch, "E1450", {"start": v(24.92, 54.32) * mm, "end": v(24.97, 54.09) * mm});
            skLineSegment(sketch, "E1451", {"start": v(24.97, 54.09) * mm, "end": v(25.17, 53.84) * mm});
            skLineSegment(sketch, "E1452", {"start": v(25.17, 53.84) * mm, "end": v(25.5, 53.6) * mm});
            skLineSegment(sketch, "E1453", {"start": v(25.5, 53.6) * mm, "end": v(25.9, 53.42) * mm});
            skLineSegment(sketch, "E1454", {"start": v(25.9, 53.42) * mm, "end": v(26.4, 53.31) * mm});
            skLineSegment(sketch, "E1455", {"start": v(26.4, 53.31) * mm, "end": v(26.93, 53.31) * mm});
            skLineSegment(sketch, "E1456", {"start": v(26.93, 53.31) * mm, "end": v(27.4, 53.43) * mm});
            skLineSegment(sketch, "E1457", {"start": v(27.4, 53.43) * mm, "end": v(27.85, 53.66) * mm});
            skLineSegment(sketch, "E1458", {"start": v(27.85, 53.66) * mm, "end": v(28.23, 53.99) * mm});
            skLineSegment(sketch, "E1459", {"start": v(28.23, 53.99) * mm, "end": v(28.52, 54.41) * mm});
            skLineSegment(sketch, "E1460", {"start": v(28.52, 54.41) * mm, "end": v(28.7, 54.92) * mm});
            skLineSegment(sketch, "E1461", {"start": v(28.7, 54.92) * mm, "end": v(28.7, 55.51) * mm});
            skLineSegment(sketch, "E1462", {"start": v(28.7, 55.51) * mm, "end": v(28.54, 56.16) * mm});
            skLineSegment(sketch, "E1463", {"start": v(28.54, 56.16) * mm, "end": v(28.16, 56.87) * mm});
            skLineSegment(sketch, "E1464", {"start": v(-42.38, 58.22) * mm, "end": v(-43.9, 57.8) * mm});
            skLineSegment(sketch, "E1465", {"start": v(-43.9, 57.8) * mm, "end": v(-47.94, 56.41) * mm});
            skLineSegment(sketch, "E1466", {"start": v(-47.94, 56.41) * mm, "end": v(-53.69, 53.77) * mm});
            skLineSegment(sketch, "E1467", {"start": v(-53.69, 53.77) * mm, "end": v(-60.35, 49.62) * mm});
            skLineSegment(sketch, "E1468", {"start": v(-60.35, 49.62) * mm, "end": v(-67.15, 43.72) * mm});
            skLineSegment(sketch, "E1469", {"start": v(-67.15, 43.72) * mm, "end": v(-73.27, 35.81) * mm});
            skLineSegment(sketch, "E1470", {"start": v(-73.27, 35.81) * mm, "end": v(-77.92, 25.64) * mm});
            skLineSegment(sketch, "E1471", {"start": v(-77.92, 25.64) * mm, "end": v(-80.3, 12.94) * mm});
            skLineSegment(sketch, "E1472", {"start": v(-80.3, 12.94) * mm, "end": v(-79.98, 13.27) * mm});
            skLineSegment(sketch, "E1473", {"start": v(-79.98, 13.27) * mm, "end": v(-79.06, 14.14) * mm});
            skLineSegment(sketch, "E1474", {"start": v(-79.06, 14.14) * mm, "end": v(-77.66, 15.4) * mm});
            skLineSegment(sketch, "E1475", {"start": v(-77.66, 15.4) * mm, "end": v(-75.86, 16.9) * mm});
            skLineSegment(sketch, "E1476", {"start": v(-75.86, 16.9) * mm, "end": v(-73.77, 18.47) * mm});
            skLineSegment(sketch, "E1477", {"start": v(-73.77, 18.47) * mm, "end": v(-71.5, 19.96) * mm});
            skLineSegment(sketch, "E1478", {"start": v(-71.5, 19.96) * mm, "end": v(-69.11, 21.2) * mm});
            skLineSegment(sketch, "E1479", {"start": v(-69.11, 21.2) * mm, "end": v(-66.73, 22.03) * mm});
            skLineSegment(sketch, "E1480", {"start": v(-66.73, 22.03) * mm, "end": v(-67.13, 21.53) * mm});
            skLineSegment(sketch, "E1481", {"start": v(-67.13, 21.53) * mm, "end": v(-68.2, 20) * mm});
            skLineSegment(sketch, "E1482", {"start": v(-68.2, 20) * mm, "end": v(-69.7, 17.46) * mm});
            skLineSegment(sketch, "E1483", {"start": v(-69.7, 17.46) * mm, "end": v(-71.46, 13.9) * mm});
            skLineSegment(sketch, "E1484", {"start": v(-71.46, 13.9) * mm, "end": v(-73.23, 9.34) * mm});
            skLineSegment(sketch, "E1485", {"start": v(-73.23, 9.34) * mm, "end": v(-74.83, 3.75) * mm});
            skLineSegment(sketch, "E1486", {"start": v(-74.83, 3.75) * mm, "end": v(-76.04, -2.85) * mm});
            skLineSegment(sketch, "E1487", {"start": v(-76.04, -2.85) * mm, "end": v(-76.64, -10.46) * mm});
            skLineSegment(sketch, "E1488", {"start": v(-76.64, -10.46) * mm, "end": v(-75.95, -9.8) * mm});
            skLineSegment(sketch, "E1489", {"start": v(-75.95, -9.8) * mm, "end": v(-74.05, -8.04) * mm});
            skLineSegment(sketch, "E1490", {"start": v(-74.05, -8.04) * mm, "end": v(-71.2, -5.53) * mm});
            skLineSegment(sketch, "E1491", {"start": v(-71.2, -5.53) * mm, "end": v(-67.7, -2.61) * mm});
            skLineSegment(sketch, "E1492", {"start": v(-67.7, -2.61) * mm, "end": v(-63.78, 0.36) * mm});
            skLineSegment(sketch, "E1493", {"start": v(-63.78, 0.36) * mm, "end": v(-59.73, 3.04) * mm});
            skLineSegment(sketch, "E1494", {"start": v(-59.73, 3.04) * mm, "end": v(-55.8, 5.08) * mm});
            skLineSegment(sketch, "E1495", {"start": v(-55.8, 5.08) * mm, "end": v(-52.29, 6.13) * mm});
            skLineSegment(sketch, "E1496", {"start": v(-52.29, 6.13) * mm, "end": v(-52.68, 5.6) * mm});
            skLineSegment(sketch, "E1497", {"start": v(-52.68, 5.6) * mm, "end": v(-53.7, 4.06) * mm});
            skLineSegment(sketch, "E1498", {"start": v(-53.7, 4.06) * mm, "end": v(-55.16, 1.55) * mm});
            skLineSegment(sketch, "E1499", {"start": v(-55.16, 1.55) * mm, "end": v(-56.83, -1.9) * mm});
            skLineSegment(sketch, "E1500", {"start": v(-56.83, -1.9) * mm, "end": v(-58.5, -6.21) * mm});
            skLineSegment(sketch, "E1501", {"start": v(-58.5, -6.21) * mm, "end": v(-59.95, -11.37) * mm});
            skLineSegment(sketch, "E1502", {"start": v(-59.95, -11.37) * mm, "end": v(-60.98, -17.32) * mm});
            skLineSegment(sketch, "E1503", {"start": v(-60.98, -17.32) * mm, "end": v(-61.37, -24) * mm});
            skLineSegment(sketch, "E1504", {"start": v(-61.37, -24) * mm, "end": v(-60.81, -23.48) * mm});
            skLineSegment(sketch, "E1505", {"start": v(-60.81, -23.48) * mm, "end": v(-59.23, -22.1) * mm});
            skLineSegment(sketch, "E1506", {"start": v(-59.23, -22.1) * mm, "end": v(-56.71, -20.15) * mm});
            skLineSegment(sketch, "E1507", {"start": v(-56.71, -20.15) * mm, "end": v(-53.38, -17.9) * mm});
            skLineSegment(sketch, "E1508", {"start": v(-53.38, -17.9) * mm, "end": v(-49.34, -15.67) * mm});
            skLineSegment(sketch, "E1509", {"start": v(-49.34, -15.67) * mm, "end": v(-44.69, -13.72) * mm});
            skLineSegment(sketch, "E1510", {"start": v(-44.69, -13.72) * mm, "end": v(-39.54, -12.34) * mm});
            skLineSegment(sketch, "E1511", {"start": v(-39.54, -12.34) * mm, "end": v(-34, -11.81) * mm});
            skLineSegment(sketch, "E1512", {"start": v(-34, -11.81) * mm, "end": v(-34.26, -11.44) * mm});
            skLineSegment(sketch, "E1513", {"start": v(-34.26, -11.44) * mm, "end": v(-34.91, -10.37) * mm});
            skLineSegment(sketch, "E1514", {"start": v(-34.91, -10.37) * mm, "end": v(-35.83, -8.63) * mm});
            skLineSegment(sketch, "E1515", {"start": v(-35.83, -8.63) * mm, "end": v(-36.88, -6.27) * mm});
            skLineSegment(sketch, "E1516", {"start": v(-36.88, -6.27) * mm, "end": v(-37.92, -3.34) * mm});
            skLineSegment(sketch, "E1517", {"start": v(-37.92, -3.34) * mm, "end": v(-38.8, 0.11) * mm});
            skLineSegment(sketch, "E1518", {"start": v(-38.8, 0.11) * mm, "end": v(-39.4, 4.05) * mm});
            skLineSegment(sketch, "E1519", {"start": v(-39.4, 4.05) * mm, "end": v(-39.58, 8.42) * mm});
            skLineSegment(sketch, "E1520", {"start": v(-39.58, 8.42) * mm, "end": v(-39.74, 8.01) * mm});
            skLineSegment(sketch, "E1521", {"start": v(-39.74, 8.01) * mm, "end": v(-40.13, 6.89) * mm});
            skLineSegment(sketch, "E1522", {"start": v(-40.13, 6.89) * mm, "end": v(-40.68, 5.2) * mm});
            skLineSegment(sketch, "E1523", {"start": v(-40.68, 5.2) * mm, "end": v(-41.28, 3.1) * mm});
            skLineSegment(sketch, "E1524", {"start": v(-41.28, 3.1) * mm, "end": v(-41.84, 0.73) * mm});
            skLineSegment(sketch, "E1525", {"start": v(-41.84, 0.73) * mm, "end": v(-42.28, -1.76) * mm});
            skLineSegment(sketch, "E1526", {"start": v(-42.28, -1.76) * mm, "end": v(-42.49, -4.2) * mm});
            skLineSegment(sketch, "E1527", {"start": v(-42.49, -4.2) * mm, "end": v(-42.38, -6.45) * mm});
            skLineSegment(sketch, "E1528", {"start": v(-42.38, -6.45) * mm, "end": v(-42.87, -6.68) * mm});
            skLineSegment(sketch, "E1529", {"start": v(-42.87, -6.68) * mm, "end": v(-44.19, -7.33) * mm});
            skLineSegment(sketch, "E1530", {"start": v(-44.19, -7.33) * mm, "end": v(-46.1, -8.3) * mm});
            skLineSegment(sketch, "E1531", {"start": v(-46.1, -8.3) * mm, "end": v(-48.39, -9.55) * mm});
            skLineSegment(sketch, "E1532", {"start": v(-48.39, -9.55) * mm, "end": v(-50.8, -10.97) * mm});
            skLineSegment(sketch, "E1533", {"start": v(-50.8, -10.97) * mm, "end": v(-53.14, -12.5) * mm});
            skLineSegment(sketch, "E1534", {"start": v(-53.14, -12.5) * mm, "end": v(-55.15, -14.04) * mm});
            skLineSegment(sketch, "E1535", {"start": v(-55.15, -14.04) * mm, "end": v(-56.62, -15.54) * mm});
            skLineSegment(sketch, "E1536", {"start": v(-56.62, -15.54) * mm, "end": v(-56.5, -14.82) * mm});
            skLineSegment(sketch, "E1537", {"start": v(-56.5, -14.82) * mm, "end": v(-56.14, -12.85) * mm});
            skLineSegment(sketch, "E1538", {"start": v(-56.14, -12.85) * mm, "end": v(-55.5, -9.94) * mm});
            skLineSegment(sketch, "E1539", {"start": v(-55.5, -9.94) * mm, "end": v(-54.57, -6.39) * mm});
            skLineSegment(sketch, "E1540", {"start": v(-54.57, -6.39) * mm, "end": v(-53.32, -2.5) * mm});
            skLineSegment(sketch, "E1541", {"start": v(-53.32, -2.5) * mm, "end": v(-51.72, 1.41) * mm});
            skLineSegment(sketch, "E1542", {"start": v(-51.72, 1.41) * mm, "end": v(-49.76, 5.06) * mm});
            skLineSegment(sketch, "E1543", {"start": v(-49.76, 5.06) * mm, "end": v(-47.4, 8.13) * mm});
            skLineSegment(sketch, "E1544", {"start": v(-47.4, 8.13) * mm, "end": v(-47.95, 8.25) * mm});
            skLineSegment(sketch, "E1545", {"start": v(-47.95, 8.25) * mm, "end": v(-49.51, 8.47) * mm});
            skLineSegment(sketch, "E1546", {"start": v(-49.51, 8.47) * mm, "end": v(-51.96, 8.53) * mm});
            skLineSegment(sketch, "E1547", {"start": v(-51.96, 8.53) * mm, "end": v(-55.17, 8.18) * mm});
            skLineSegment(sketch, "E1548", {"start": v(-55.17, 8.18) * mm, "end": v(-59, 7.17) * mm});
            skLineSegment(sketch, "E1549", {"start": v(-59, 7.17) * mm, "end": v(-63.34, 5.26) * mm});
            skLineSegment(sketch, "E1550", {"start": v(-63.34, 5.26) * mm, "end": v(-68.04, 2.2) * mm});
            skLineSegment(sketch, "E1551", {"start": v(-68.04, 2.2) * mm, "end": v(-72.98, -2.27) * mm});
            skLineSegment(sketch, "E1552", {"start": v(-72.98, -2.27) * mm, "end": v(-72.8, -1.39) * mm});
            skLineSegment(sketch, "E1553", {"start": v(-72.8, -1.39) * mm, "end": v(-72.22, 1.01) * mm});
            skLineSegment(sketch, "E1554", {"start": v(-72.22, 1.01) * mm, "end": v(-71.28, 4.55) * mm});
            skLineSegment(sketch, "E1555", {"start": v(-71.28, 4.55) * mm, "end": v(-69.97, 8.84) * mm});
            skLineSegment(sketch, "E1556", {"start": v(-69.97, 8.84) * mm, "end": v(-68.3, 13.5) * mm});
            skLineSegment(sketch, "E1557", {"start": v(-68.3, 13.5) * mm, "end": v(-66.27, 18.16) * mm});
            skLineSegment(sketch, "E1558", {"start": v(-66.27, 18.16) * mm, "end": v(-63.89, 22.44) * mm});
            skLineSegment(sketch, "E1559", {"start": v(-63.89, 22.44) * mm, "end": v(-61.16, 25.95) * mm});
            skLineSegment(sketch, "E1560", {"start": v(-61.16, 25.95) * mm, "end": v(-61.46, 25.91) * mm});
            skLineSegment(sketch, "E1561", {"start": v(-61.46, 25.91) * mm, "end": v(-62.33, 25.78) * mm});
            skLineSegment(sketch, "E1562", {"start": v(-62.33, 25.78) * mm, "end": v(-63.7, 25.5) * mm});
            skLineSegment(sketch, "E1563", {"start": v(-63.7, 25.5) * mm, "end": v(-65.47, 25.03) * mm});
            skLineSegment(sketch, "E1564", {"start": v(-65.47, 25.03) * mm, "end": v(-67.6, 24.32) * mm});
            skLineSegment(sketch, "E1565", {"start": v(-67.6, 24.32) * mm, "end": v(-70, 23.33) * mm});
            skLineSegment(sketch, "E1566", {"start": v(-70, 23.33) * mm, "end": v(-72.62, 22.01) * mm});
            skLineSegment(sketch, "E1567", {"start": v(-72.62, 22.01) * mm, "end": v(-75.36, 20.32) * mm});
            skLineSegment(sketch, "E1568", {"start": v(-75.36, 20.32) * mm, "end": v(-75.07, 21.49) * mm});
            skLineSegment(sketch, "E1569", {"start": v(-75.07, 21.49) * mm, "end": v(-74.06, 24.67) * mm});
            skLineSegment(sketch, "E1570", {"start": v(-74.06, 24.67) * mm, "end": v(-72.15, 29.36) * mm});
            skLineSegment(sketch, "E1571", {"start": v(-72.15, 29.36) * mm, "end": v(-69.15, 35.07) * mm});
            skLineSegment(sketch, "E1572", {"start": v(-69.15, 35.07) * mm, "end": v(-64.87, 41.31) * mm});
            skLineSegment(sketch, "E1573", {"start": v(-64.87, 41.31) * mm, "end": v(-59.1, 47.58) * mm});
            skLineSegment(sketch, "E1574", {"start": v(-59.1, 47.58) * mm, "end": v(-51.67, 53.38) * mm});
            skLineSegment(sketch, "E1575", {"start": v(-51.67, 53.38) * mm, "end": v(-42.38, 58.22) * mm});
            skLineSegment(sketch, "E1576", {"start": v(-34, 71.13) * mm, "end": v(-35.45, 71.55) * mm});
            skLineSegment(sketch, "E1577", {"start": v(-35.45, 71.55) * mm, "end": v(-37.02, 71.87) * mm});
            skLineSegment(sketch, "E1578", {"start": v(-37.02, 71.87) * mm, "end": v(-38.7, 72.09) * mm});
            skLineSegment(sketch, "E1579", {"start": v(-38.7, 72.09) * mm, "end": v(-40.46, 72.24) * mm});
            skLineSegment(sketch, "E1580", {"start": v(-40.46, 72.24) * mm, "end": v(-42.3, 72.34) * mm});
            skLineSegment(sketch, "E1581", {"start": v(-42.3, 72.34) * mm, "end": v(-44.17, 72.4) * mm});
            skLineSegment(sketch, "E1582", {"start": v(-44.17, 72.4) * mm, "end": v(-46.08, 72.47) * mm});
            skLineSegment(sketch, "E1583", {"start": v(-46.08, 72.47) * mm, "end": v(-48, 72.55) * mm});
            skLineSegment(sketch, "E1584", {"start": v(-48, 72.55) * mm, "end": v(-49.25, 72.7) * mm});
            skLineSegment(sketch, "E1585", {"start": v(-49.25, 72.7) * mm, "end": v(-50.61, 73.01) * mm});
            skLineSegment(sketch, "E1586", {"start": v(-50.61, 73.01) * mm, "end": v(-52.06, 73.37) * mm});
            skLineSegment(sketch, "E1587", {"start": v(-52.06, 73.37) * mm, "end": v(-53.6, 73.69) * mm});
            skLineSegment(sketch, "E1588", {"start": v(-53.6, 73.69) * mm, "end": v(-55.2, 73.88) * mm});
            skLineSegment(sketch, "E1589", {"start": v(-55.2, 73.88) * mm, "end": v(-56.84, 73.85) * mm});
            skLineSegment(sketch, "E1590", {"start": v(-56.84, 73.85) * mm, "end": v(-58.52, 73.5) * mm});
            skLineSegment(sketch, "E1591", {"start": v(-58.52, 73.5) * mm, "end": v(-60.23, 72.75) * mm});
            skLineSegment(sketch, "E1592", {"start": v(-60.23, 72.75) * mm, "end": v(-61.77, 70.92) * mm});
            skLineSegment(sketch, "E1593", {"start": v(-61.77, 70.92) * mm, "end": v(-61.57, 68.55) * mm});
            skLineSegment(sketch, "E1594", {"start": v(-61.57, 68.55) * mm, "end": v(-60.1, 65.89) * mm});
            skLineSegment(sketch, "E1595", {"start": v(-60.1, 65.89) * mm, "end": v(-57.83, 63.16) * mm});
            skLineSegment(sketch, "E1596", {"start": v(-57.83, 63.16) * mm, "end": v(-55.24, 60.63) * mm});
            skLineSegment(sketch, "E1597", {"start": v(-55.24, 60.63) * mm, "end": v(-52.8, 58.52) * mm});
            skLineSegment(sketch, "E1598", {"start": v(-52.8, 58.52) * mm, "end": v(-50.99, 57.07) * mm});
            skLineSegment(sketch, "E1599", {"start": v(-50.99, 57.07) * mm, "end": v(-50.28, 56.54) * mm});
            skLineSegment(sketch, "E1600", {"start": v(-50.28, 56.54) * mm, "end": v(-49.87, 56.91) * mm});
            skLineSegment(sketch, "E1601", {"start": v(-49.87, 56.91) * mm, "end": v(-48.7, 57.9) * mm});
            skLineSegment(sketch, "E1602", {"start": v(-48.7, 57.9) * mm, "end": v(-46.89, 59.28) * mm});
            skLineSegment(sketch, "E1603", {"start": v(-46.89, 59.28) * mm, "end": v(-44.55, 60.87) * mm});
            skLineSegment(sketch, "E1604", {"start": v(-44.55, 60.87) * mm, "end": v(-41.81, 62.45) * mm});
            skLineSegment(sketch, "E1605", {"start": v(-41.81, 62.45) * mm, "end": v(-38.77, 63.82) * mm});
            skLineSegment(sketch, "E1606", {"start": v(-38.77, 63.82) * mm, "end": v(-35.56, 64.78) * mm});
            skLineSegment(sketch, "E1607", {"start": v(-35.56, 64.78) * mm, "end": v(-32.28, 65.13) * mm});
            skLineSegment(sketch, "E1608", {"start": v(-32.28, 65.13) * mm, "end": v(-28.5, 64.97) * mm});
            skLineSegment(sketch, "E1609", {"start": v(-28.5, 64.97) * mm, "end": v(-25.47, 64.63) * mm});
            skLineSegment(sketch, "E1610", {"start": v(-25.47, 64.63) * mm, "end": v(-23.08, 64.17) * mm});
            skLineSegment(sketch, "E1611", {"start": v(-23.08, 64.17) * mm, "end": v(-21.28, 63.66) * mm});
            skLineSegment(sketch, "E1612", {"start": v(-21.28, 63.66) * mm, "end": v(-20, 63.15) * mm});
            skLineSegment(sketch, "E1613", {"start": v(-20, 63.15) * mm, "end": v(-19.18, 62.7) * mm});
            skLineSegment(sketch, "E1614", {"start": v(-19.18, 62.7) * mm, "end": v(-18.73, 62.4) * mm});
            skLineSegment(sketch, "E1615", {"start": v(-18.73, 62.4) * mm, "end": v(-18.6, 62.28) * mm});
            skLineSegment(sketch, "E1616", {"start": v(-18.6, 62.28) * mm, "end": v(-18.86, 62.6) * mm});
            skLineSegment(sketch, "E1617", {"start": v(-18.86, 62.6) * mm, "end": v(-19.63, 63.42) * mm});
            skLineSegment(sketch, "E1618", {"start": v(-19.63, 63.42) * mm, "end": v(-20.93, 64.54) * mm});
            skLineSegment(sketch, "E1619", {"start": v(-20.93, 64.54) * mm, "end": v(-22.78, 65.75) * mm});
            skLineSegment(sketch, "E1620", {"start": v(-22.78, 65.75) * mm, "end": v(-25.18, 66.85) * mm});
            skLineSegment(sketch, "E1621", {"start": v(-25.18, 66.85) * mm, "end": v(-28.15, 67.62) * mm});
            skLineSegment(sketch, "E1622", {"start": v(-28.15, 67.62) * mm, "end": v(-31.7, 67.86) * mm});
            skLineSegment(sketch, "E1623", {"start": v(-31.7, 67.86) * mm, "end": v(-35.83, 67.36) * mm});
            skLineSegment(sketch, "E1624", {"start": v(-35.83, 67.36) * mm, "end": v(-38.08, 66.85) * mm});
            skLineSegment(sketch, "E1625", {"start": v(-38.08, 66.85) * mm, "end": v(-40.04, 66.35) * mm});
            skLineSegment(sketch, "E1626", {"start": v(-40.04, 66.35) * mm, "end": v(-41.78, 65.9) * mm});
            skLineSegment(sketch, "E1627", {"start": v(-41.78, 65.9) * mm, "end": v(-43.38, 65.52) * mm});
            skLineSegment(sketch, "E1628", {"start": v(-43.38, 65.52) * mm, "end": v(-44.9, 65.27) * mm});
            skLineSegment(sketch, "E1629", {"start": v(-44.9, 65.27) * mm, "end": v(-46.44, 65.17) * mm});
            skLineSegment(sketch, "E1630", {"start": v(-46.44, 65.17) * mm, "end": v(-48.04, 65.25) * mm});
            skLineSegment(sketch, "E1631", {"start": v(-48.04, 65.25) * mm, "end": v(-49.79, 65.56) * mm});
            skLineSegment(sketch, "E1632", {"start": v(-49.79, 65.56) * mm, "end": v(-51.63, 66.1) * mm});
            skLineSegment(sketch, "E1633", {"start": v(-51.63, 66.1) * mm, "end": v(-53.4, 66.85) * mm});
            skLineSegment(sketch, "E1634", {"start": v(-53.4, 66.85) * mm, "end": v(-55.04, 67.72) * mm});
            skLineSegment(sketch, "E1635", {"start": v(-55.04, 67.72) * mm, "end": v(-56.45, 68.63) * mm});
            skLineSegment(sketch, "E1636", {"start": v(-56.45, 68.63) * mm, "end": v(-57.56, 69.54) * mm});
            skLineSegment(sketch, "E1637", {"start": v(-57.56, 69.54) * mm, "end": v(-58.3, 70.36) * mm});
            skLineSegment(sketch, "E1638", {"start": v(-58.3, 70.36) * mm, "end": v(-58.57, 71.02) * mm});
            skLineSegment(sketch, "E1639", {"start": v(-58.57, 71.02) * mm, "end": v(-58.32, 71.46) * mm});
            skLineSegment(sketch, "E1640", {"start": v(-58.32, 71.46) * mm, "end": v(-57.7, 71.73) * mm});
            skLineSegment(sketch, "E1641", {"start": v(-57.7, 71.73) * mm, "end": v(-56.98, 71.92) * mm});
            skLineSegment(sketch, "E1642", {"start": v(-56.98, 71.92) * mm, "end": v(-56.1, 72.02) * mm});
            skLineSegment(sketch, "E1643", {"start": v(-56.1, 72.02) * mm, "end": v(-55.08, 72.04) * mm});
            skLineSegment(sketch, "E1644", {"start": v(-55.08, 72.04) * mm, "end": v(-53.9, 71.98) * mm});
            skLineSegment(sketch, "E1645", {"start": v(-53.9, 71.98) * mm, "end": v(-52.51, 71.84) * mm});
            skLineSegment(sketch, "E1646", {"start": v(-52.51, 71.84) * mm, "end": v(-50.93, 71.6) * mm});
            skLineSegment(sketch, "E1647", {"start": v(-50.93, 71.6) * mm, "end": v(-49.13, 71.3) * mm});
            skLineSegment(sketch, "E1648", {"start": v(-49.13, 71.3) * mm, "end": v(-47.46, 71.1) * mm});
            skLineSegment(sketch, "E1649", {"start": v(-47.46, 71.1) * mm, "end": v(-45.27, 71) * mm});
            skLineSegment(sketch, "E1650", {"start": v(-45.27, 71) * mm, "end": v(-42.78, 70.96) * mm});
            skLineSegment(sketch, "E1651", {"start": v(-42.78, 70.96) * mm, "end": v(-40.24, 70.97) * mm});
            skLineSegment(sketch, "E1652", {"start": v(-40.24, 70.97) * mm, "end": v(-37.86, 71) * mm});
            skLineSegment(sketch, "E1653", {"start": v(-37.86, 71) * mm, "end": v(-35.87, 71.06) * mm});
            skLineSegment(sketch, "E1654", {"start": v(-35.87, 71.06) * mm, "end": v(-34.51, 71.1) * mm});
            skLineSegment(sketch, "E1655", {"start": v(-34.51, 71.1) * mm, "end": v(-34, 71.13) * mm});
            skLineSegment(sketch, "E1656", {"start": v(-0.3, 72.61) * mm, "end": v(6.32, 73.37) * mm});
            skLineSegment(sketch, "E1657", {"start": v(6.32, 73.37) * mm, "end": v(12.58, 73.47) * mm});
            skLineSegment(sketch, "E1658", {"start": v(12.58, 73.47) * mm, "end": v(18.32, 73.09) * mm});
            skLineSegment(sketch, "E1659", {"start": v(18.32, 73.09) * mm, "end": v(23.38, 72.4) * mm});
            skLineSegment(sketch, "E1660", {"start": v(23.38, 72.4) * mm, "end": v(27.6, 71.56) * mm});
            skLineSegment(sketch, "E1661", {"start": v(27.6, 71.56) * mm, "end": v(30.82, 70.75) * mm});
            skLineSegment(sketch, "E1662", {"start": v(30.82, 70.75) * mm, "end": v(32.87, 70.14) * mm});
            skLineSegment(sketch, "E1663", {"start": v(32.87, 70.14) * mm, "end": v(33.59, 69.9) * mm});
            skLineSegment(sketch, "E1664", {"start": v(33.59, 69.9) * mm, "end": v(32.92, 70.26) * mm});
            skLineSegment(sketch, "E1665", {"start": v(32.92, 70.26) * mm, "end": v(31, 71.19) * mm});
            skLineSegment(sketch, "E1666", {"start": v(31, 71.19) * mm, "end": v(27.95, 72.41) * mm});
            skLineSegment(sketch, "E1667", {"start": v(27.95, 72.41) * mm, "end": v(23.87, 73.68) * mm});
            skLineSegment(sketch, "E1668", {"start": v(23.87, 73.68) * mm, "end": v(18.9, 74.72) * mm});
            skLineSegment(sketch, "E1669", {"start": v(18.9, 74.72) * mm, "end": v(13.13, 75.29) * mm});
            skLineSegment(sketch, "E1670", {"start": v(13.13, 75.29) * mm, "end": v(6.7, 75.11) * mm});
            skLineSegment(sketch, "E1671", {"start": v(6.7, 75.11) * mm, "end": v(-0.3, 73.94) * mm});
            skLineSegment(sketch, "E1672", {"start": v(-0.3, 73.94) * mm, "end": v(-7.29, 75.11) * mm});
            skLineSegment(sketch, "E1673", {"start": v(-7.29, 75.11) * mm, "end": v(-13.72, 75.29) * mm});
            skLineSegment(sketch, "E1674", {"start": v(-13.72, 75.29) * mm, "end": v(-19.49, 74.72) * mm});
            skLineSegment(sketch, "E1675", {"start": v(-19.49, 74.72) * mm, "end": v(-24.47, 73.68) * mm});
            skLineSegment(sketch, "E1676", {"start": v(-24.47, 73.68) * mm, "end": v(-28.54, 72.41) * mm});
            skLineSegment(sketch, "E1677", {"start": v(-28.54, 72.41) * mm, "end": v(-31.6, 71.19) * mm});
            skLineSegment(sketch, "E1678", {"start": v(-31.6, 71.19) * mm, "end": v(-33.51, 70.26) * mm});
            skLineSegment(sketch, "E1679", {"start": v(-33.51, 70.26) * mm, "end": v(-34.18, 69.9) * mm});
            skLineSegment(sketch, "E1680", {"start": v(-34.18, 69.9) * mm, "end": v(-33.46, 70.14) * mm});
            skLineSegment(sketch, "E1681", {"start": v(-33.46, 70.14) * mm, "end": v(-31.41, 70.75) * mm});
            skLineSegment(sketch, "E1682", {"start": v(-31.41, 70.75) * mm, "end": v(-28.2, 71.56) * mm});
            skLineSegment(sketch, "E1683", {"start": v(-28.2, 71.56) * mm, "end": v(-23.98, 72.4) * mm});
            skLineSegment(sketch, "E1684", {"start": v(-23.98, 72.4) * mm, "end": v(-18.92, 73.09) * mm});
            skLineSegment(sketch, "E1685", {"start": v(-18.92, 73.09) * mm, "end": v(-13.17, 73.47) * mm});
            skLineSegment(sketch, "E1686", {"start": v(-13.17, 73.47) * mm, "end": v(-6.91, 73.37) * mm});
            skLineSegment(sketch, "E1687", {"start": v(-6.91, 73.37) * mm, "end": v(-0.3, 72.61) * mm});
            skLineSegment(sketch, "E1688", {"start": v(-0.13, -69.53) * mm, "end": v(0.9, -68.2) * mm});
            skLineSegment(sketch, "E1689", {"start": v(0.9, -68.2) * mm, "end": v(1.62, -66.68) * mm});
            skLineSegment(sketch, "E1690", {"start": v(1.62, -66.68) * mm, "end": v(2.08, -65.07) * mm});
            skLineSegment(sketch, "E1691", {"start": v(2.08, -65.07) * mm, "end": v(2.34, -63.5) * mm});
            skLineSegment(sketch, "E1692", {"start": v(2.34, -63.5) * mm, "end": v(2.45, -62.06) * mm});
            skLineSegment(sketch, "E1693", {"start": v(2.45, -62.06) * mm, "end": v(2.46, -60.9) * mm});
            skLineSegment(sketch, "E1694", {"start": v(2.46, -60.9) * mm, "end": v(2.42, -60.11) * mm});
            skLineSegment(sketch, "E1695", {"start": v(2.42, -60.11) * mm, "end": v(2.4, -59.83) * mm});
            skLineSegment(sketch, "E1696", {"start": v(2.4, -59.83) * mm, "end": v(3.45, -60.1) * mm});
            skLineSegment(sketch, "E1697", {"start": v(3.45, -60.1) * mm, "end": v(4.33, -60.44) * mm});
            skLineSegment(sketch, "E1698", {"start": v(4.33, -60.44) * mm, "end": v(5.06, -60.8) * mm});
            skLineSegment(sketch, "E1699", {"start": v(5.06, -60.8) * mm, "end": v(5.64, -61.17) * mm});
            skLineSegment(sketch, "E1700", {"start": v(5.64, -61.17) * mm, "end": v(6.09, -61.5) * mm});
            skLineSegment(sketch, "E1701", {"start": v(6.09, -61.5) * mm, "end": v(6.4, -61.78) * mm});
            skLineSegment(sketch, "E1702", {"start": v(6.4, -61.78) * mm, "end": v(6.57, -61.96) * mm});
            skLineSegment(sketch, "E1703", {"start": v(6.57, -61.96) * mm, "end": v(6.63, -62.03) * mm});
            skLineSegment(sketch, "E1704", {"start": v(6.63, -62.03) * mm, "end": v(6.89, -61.71) * mm});
            skLineSegment(sketch, "E1705", {"start": v(6.89, -61.71) * mm, "end": v(7.07, -61.1) * mm});
            skLineSegment(sketch, "E1706", {"start": v(7.07, -61.1) * mm, "end": v(7.2, -60.3) * mm});
            skLineSegment(sketch, "E1707", {"start": v(7.2, -60.3) * mm, "end": v(7.27, -59.41) * mm});
            skLineSegment(sketch, "E1708", {"start": v(7.27, -59.41) * mm, "end": v(7.31, -58.54) * mm});
            skLineSegment(sketch, "E1709", {"start": v(7.31, -58.54) * mm, "end": v(7.33, -57.78) * mm});
            skLineSegment(sketch, "E1710", {"start": v(7.33, -57.78) * mm, "end": v(7.33, -57.26) * mm});
            skLineSegment(sketch, "E1711", {"start": v(7.33, -57.26) * mm, "end": v(7.32, -57.06) * mm});
            skLineSegment(sketch, "E1712", {"start": v(7.32, -57.06) * mm, "end": v(7.96, -57.16) * mm});
            skLineSegment(sketch, "E1713", {"start": v(7.96, -57.16) * mm, "end": v(8.54, -57.35) * mm});
            skLineSegment(sketch, "E1714", {"start": v(8.54, -57.35) * mm, "end": v(9.05, -57.6) * mm});
            skLineSegment(sketch, "E1715", {"start": v(9.05, -57.6) * mm, "end": v(9.48, -57.86) * mm});
            skLineSegment(sketch, "E1716", {"start": v(9.48, -57.86) * mm, "end": v(9.84, -58.11) * mm});
            skLineSegment(sketch, "E1717", {"start": v(9.84, -58.11) * mm, "end": v(10.1, -58.33) * mm});
            skLineSegment(sketch, "E1718", {"start": v(10.1, -58.33) * mm, "end": v(10.27, -58.49) * mm});
            skLineSegment(sketch, "E1719", {"start": v(10.27, -58.49) * mm, "end": v(10.32, -58.55) * mm});
            skLineSegment(sketch, "E1720", {"start": v(10.32, -58.55) * mm, "end": v(10.66, -58.3) * mm});
            skLineSegment(sketch, "E1721", {"start": v(10.66, -58.3) * mm, "end": v(11.02, -57.86) * mm});
            skLineSegment(sketch, "E1722", {"start": v(11.02, -57.86) * mm, "end": v(11.38, -57.3) * mm});
            skLineSegment(sketch, "E1723", {"start": v(11.38, -57.3) * mm, "end": v(11.71, -56.69) * mm});
            skLineSegment(sketch, "E1724", {"start": v(11.71, -56.69) * mm, "end": v(12.01, -56.1) * mm});
            skLineSegment(sketch, "E1725", {"start": v(12.01, -56.1) * mm, "end": v(12.25, -55.59) * mm});
            skLineSegment(sketch, "E1726", {"start": v(12.25, -55.59) * mm, "end": v(12.4, -55.23) * mm});
            skLineSegment(sketch, "E1727", {"start": v(12.4, -55.23) * mm, "end": v(12.47, -55.1) * mm});
            skLineSegment(sketch, "E1728", {"start": v(12.47, -55.1) * mm, "end": v(12.46, -55.38) * mm});
            skLineSegment(sketch, "E1729", {"start": v(12.46, -55.38) * mm, "end": v(12.42, -56.16) * mm});
            skLineSegment(sketch, "E1730", {"start": v(12.42, -56.16) * mm, "end": v(12.32, -57.31) * mm});
            skLineSegment(sketch, "E1731", {"start": v(12.32, -57.31) * mm, "end": v(12.15, -58.72) * mm});
            skLineSegment(sketch, "E1732", {"start": v(12.15, -58.72) * mm, "end": v(11.87, -60.27) * mm});
            skLineSegment(sketch, "E1733", {"start": v(11.87, -60.27) * mm, "end": v(11.48, -61.84) * mm});
            skLineSegment(sketch, "E1734", {"start": v(11.48, -61.84) * mm, "end": v(10.94, -63.3) * mm});
            skLineSegment(sketch, "E1735", {"start": v(10.94, -63.3) * mm, "end": v(10.23, -64.55) * mm});
            skLineSegment(sketch, "E1736", {"start": v(10.23, -64.55) * mm, "end": v(10.22, -64.41) * mm});
            skLineSegment(sketch, "E1737", {"start": v(10.22, -64.41) * mm, "end": v(10.18, -64.05) * mm});
            skLineSegment(sketch, "E1738", {"start": v(10.18, -64.05) * mm, "end": v(10.09, -63.55) * mm});
            skLineSegment(sketch, "E1739", {"start": v(10.09, -63.55) * mm, "end": v(9.93, -62.98) * mm});
            skLineSegment(sketch, "E1740", {"start": v(9.93, -62.98) * mm, "end": v(9.7, -62.43) * mm});
            skLineSegment(sketch, "E1741", {"start": v(9.7, -62.43) * mm, "end": v(9.37, -61.96) * mm});
            skLineSegment(sketch, "E1742", {"start": v(9.37, -61.96) * mm, "end": v(8.93, -61.67) * mm});
            skLineSegment(sketch, "E1743", {"start": v(8.93, -61.67) * mm, "end": v(8.37, -61.62) * mm});
            skLineSegment(sketch, "E1744", {"start": v(8.37, -61.62) * mm, "end": v(8.38, -61.76) * mm});
            skLineSegment(sketch, "E1745", {"start": v(8.38, -61.76) * mm, "end": v(8.4, -62.15) * mm});
            skLineSegment(sketch, "E1746", {"start": v(8.4, -62.15) * mm, "end": v(8.4, -62.74) * mm});
            skLineSegment(sketch, "E1747", {"start": v(8.4, -62.74) * mm, "end": v(8.35, -63.47) * mm});
            skLineSegment(sketch, "E1748", {"start": v(8.35, -63.47) * mm, "end": v(8.21, -64.3) * mm});
            skLineSegment(sketch, "E1749", {"start": v(8.21, -64.3) * mm, "end": v(7.95, -65.18) * mm});
            skLineSegment(sketch, "E1750", {"start": v(7.95, -65.18) * mm, "end": v(7.54, -66.05) * mm});
            skLineSegment(sketch, "E1751", {"start": v(7.54, -66.05) * mm, "end": v(6.94, -66.86) * mm});
            skLineSegment(sketch, "E1752", {"start": v(6.94, -66.86) * mm, "end": v(6.9, -66.74) * mm});
            skLineSegment(sketch, "E1753", {"start": v(6.9, -66.74) * mm, "end": v(6.76, -66.42) * mm});
            skLineSegment(sketch, "E1754", {"start": v(6.76, -66.42) * mm, "end": v(6.55, -65.97) * mm});
            skLineSegment(sketch, "E1755", {"start": v(6.55, -65.97) * mm, "end": v(6.25, -65.45) * mm});
            skLineSegment(sketch, "E1756", {"start": v(6.25, -65.45) * mm, "end": v(5.88, -64.94) * mm});
            skLineSegment(sketch, "E1757", {"start": v(5.88, -64.94) * mm, "end": v(5.44, -64.5) * mm});
            skLineSegment(sketch, "E1758", {"start": v(5.44, -64.5) * mm, "end": v(4.94, -64.2) * mm});
            skLineSegment(sketch, "E1759", {"start": v(4.94, -64.2) * mm, "end": v(4.37, -64.1) * mm});
            skLineSegment(sketch, "E1760", {"start": v(4.37, -64.1) * mm, "end": v(4.38, -64.32) * mm});
            skLineSegment(sketch, "E1761", {"start": v(4.38, -64.32) * mm, "end": v(4.37, -64.92) * mm});
            skLineSegment(sketch, "E1762", {"start": v(4.37, -64.92) * mm, "end": v(4.27, -65.85) * mm});
            skLineSegment(sketch, "E1763", {"start": v(4.27, -65.85) * mm, "end": v(4, -67.04) * mm});
            skLineSegment(sketch, "E1764", {"start": v(4, -67.04) * mm, "end": v(3.5, -68.44) * mm});
            skLineSegment(sketch, "E1765", {"start": v(3.5, -68.44) * mm, "end": v(2.69, -70) * mm});
            skLineSegment(sketch, "E1766", {"start": v(2.69, -70) * mm, "end": v(1.5, -71.64) * mm});
            skLineSegment(sketch, "E1767", {"start": v(1.5, -71.64) * mm, "end": v(-0.13, -73.3) * mm});
            skLineSegment(sketch, "E1768", {"start": v(-0.13, -73.3) * mm, "end": v(-1.76, -71.64) * mm});
            skLineSegment(sketch, "E1769", {"start": v(-1.76, -71.64) * mm, "end": v(-2.94, -70) * mm});
            skLineSegment(sketch, "E1770", {"start": v(-2.94, -70) * mm, "end": v(-3.75, -68.44) * mm});
            skLineSegment(sketch, "E1771", {"start": v(-3.75, -68.44) * mm, "end": v(-4.25, -67.04) * mm});
            skLineSegment(sketch, "E1772", {"start": v(-4.25, -67.04) * mm, "end": v(-4.52, -65.85) * mm});
            skLineSegment(sketch, "E1773", {"start": v(-4.52, -65.85) * mm, "end": v(-4.62, -64.92) * mm});
            skLineSegment(sketch, "E1774", {"start": v(-4.62, -64.92) * mm, "end": v(-4.63, -64.32) * mm});
            skLineSegment(sketch, "E1775", {"start": v(-4.63, -64.32) * mm, "end": v(-4.62, -64.1) * mm});
            skLineSegment(sketch, "E1776", {"start": v(-4.62, -64.1) * mm, "end": v(-5.19, -64.2) * mm});
            skLineSegment(sketch, "E1777", {"start": v(-5.19, -64.2) * mm, "end": v(-5.7, -64.5) * mm});
            skLineSegment(sketch, "E1778", {"start": v(-5.7, -64.5) * mm, "end": v(-6.14, -64.94) * mm});
            skLineSegment(sketch, "E1779", {"start": v(-6.14, -64.94) * mm, "end": v(-6.5, -65.45) * mm});
            skLineSegment(sketch, "E1780", {"start": v(-6.5, -65.45) * mm, "end": v(-6.8, -65.97) * mm});
            skLineSegment(sketch, "E1781", {"start": v(-6.8, -65.97) * mm, "end": v(-7.02, -66.42) * mm});
            skLineSegment(sketch, "E1782", {"start": v(-7.02, -66.42) * mm, "end": v(-7.15, -66.74) * mm});
            skLineSegment(sketch, "E1783", {"start": v(-7.15, -66.74) * mm, "end": v(-7.2, -66.86) * mm});
            skLineSegment(sketch, "E1784", {"start": v(-7.2, -66.86) * mm, "end": v(-7.8, -66.05) * mm});
            skLineSegment(sketch, "E1785", {"start": v(-7.8, -66.05) * mm, "end": v(-8.2, -65.18) * mm});
            skLineSegment(sketch, "E1786", {"start": v(-8.2, -65.18) * mm, "end": v(-8.47, -64.3) * mm});
            skLineSegment(sketch, "E1787", {"start": v(-8.47, -64.3) * mm, "end": v(-8.6, -63.47) * mm});
            skLineSegment(sketch, "E1788", {"start": v(-8.6, -63.47) * mm, "end": v(-8.66, -62.74) * mm});
            skLineSegment(sketch, "E1789", {"start": v(-8.66, -62.74) * mm, "end": v(-8.66, -62.15) * mm});
            skLineSegment(sketch, "E1790", {"start": v(-8.66, -62.15) * mm, "end": v(-8.63, -61.76) * mm});
            skLineSegment(sketch, "E1791", {"start": v(-8.63, -61.76) * mm, "end": v(-8.62, -61.62) * mm});
            skLineSegment(sketch, "E1792", {"start": v(-8.62, -61.62) * mm, "end": v(-9.18, -61.67) * mm});
            skLineSegment(sketch, "E1793", {"start": v(-9.18, -61.67) * mm, "end": v(-9.62, -61.96) * mm});
            skLineSegment(sketch, "E1794", {"start": v(-9.62, -61.96) * mm, "end": v(-9.95, -62.43) * mm});
            skLineSegment(sketch, "E1795", {"start": v(-9.95, -62.43) * mm, "end": v(-10.18, -62.98) * mm});
            skLineSegment(sketch, "E1796", {"start": v(-10.18, -62.98) * mm, "end": v(-10.34, -63.55) * mm});
            skLineSegment(sketch, "E1797", {"start": v(-10.34, -63.55) * mm, "end": v(-10.43, -64.05) * mm});
            skLineSegment(sketch, "E1798", {"start": v(-10.43, -64.05) * mm, "end": v(-10.47, -64.41) * mm});
            skLineSegment(sketch, "E1799", {"start": v(-10.47, -64.41) * mm, "end": v(-10.48, -64.55) * mm});
            skLineSegment(sketch, "E1800", {"start": v(-10.48, -64.55) * mm, "end": v(-11.2, -63.3) * mm});
            skLineSegment(sketch, "E1801", {"start": v(-11.2, -63.3) * mm, "end": v(-11.73, -61.84) * mm});
            skLineSegment(sketch, "E1802", {"start": v(-11.73, -61.84) * mm, "end": v(-12.13, -60.27) * mm});
            skLineSegment(sketch, "E1803", {"start": v(-12.13, -60.27) * mm, "end": v(-12.4, -58.72) * mm});
            skLineSegment(sketch, "E1804", {"start": v(-12.4, -58.72) * mm, "end": v(-12.57, -57.31) * mm});
            skLineSegment(sketch, "E1805", {"start": v(-12.57, -57.31) * mm, "end": v(-12.67, -56.16) * mm});
            skLineSegment(sketch, "E1806", {"start": v(-12.67, -56.16) * mm, "end": v(-12.7, -55.38) * mm});
            skLineSegment(sketch, "E1807", {"start": v(-12.7, -55.38) * mm, "end": v(-12.72, -55.1) * mm});
            skLineSegment(sketch, "E1808", {"start": v(-12.72, -55.1) * mm, "end": v(-12.66, -55.23) * mm});
            skLineSegment(sketch, "E1809", {"start": v(-12.66, -55.23) * mm, "end": v(-12.5, -55.59) * mm});
            skLineSegment(sketch, "E1810", {"start": v(-12.5, -55.59) * mm, "end": v(-12.27, -56.1) * mm});
            skLineSegment(sketch, "E1811", {"start": v(-12.27, -56.1) * mm, "end": v(-11.97, -56.69) * mm});
            skLineSegment(sketch, "E1812", {"start": v(-11.97, -56.69) * mm, "end": v(-11.63, -57.3) * mm});
            skLineSegment(sketch, "E1813", {"start": v(-11.63, -57.3) * mm, "end": v(-11.27, -57.86) * mm});
            skLineSegment(sketch, "E1814", {"start": v(-11.27, -57.86) * mm, "end": v(-10.91, -58.3) * mm});
            skLineSegment(sketch, "E1815", {"start": v(-10.91, -58.3) * mm, "end": v(-10.58, -58.55) * mm});
            skLineSegment(sketch, "E1816", {"start": v(-10.58, -58.55) * mm, "end": v(-10.52, -58.49) * mm});
            skLineSegment(sketch, "E1817", {"start": v(-10.52, -58.49) * mm, "end": v(-10.36, -58.33) * mm});
            skLineSegment(sketch, "E1818", {"start": v(-10.36, -58.33) * mm, "end": v(-10.1, -58.11) * mm});
            skLineSegment(sketch, "E1819", {"start": v(-10.1, -58.11) * mm, "end": v(-9.74, -57.86) * mm});
            skLineSegment(sketch, "E1820", {"start": v(-9.74, -57.86) * mm, "end": v(-9.3, -57.6) * mm});
            skLineSegment(sketch, "E1821", {"start": v(-9.3, -57.6) * mm, "end": v(-8.79, -57.35) * mm});
            skLineSegment(sketch, "E1822", {"start": v(-8.79, -57.35) * mm, "end": v(-8.21, -57.16) * mm});
            skLineSegment(sketch, "E1823", {"start": v(-8.21, -57.16) * mm, "end": v(-7.58, -57.06) * mm});
            skLineSegment(sketch, "E1824", {"start": v(-7.58, -57.06) * mm, "end": v(-7.58, -57.26) * mm});
            skLineSegment(sketch, "E1825", {"start": v(-7.58, -57.26) * mm, "end": v(-7.58, -57.78) * mm});
            skLineSegment(sketch, "E1826", {"start": v(-7.58, -57.78) * mm, "end": v(-7.57, -58.54) * mm});
            skLineSegment(sketch, "E1827", {"start": v(-7.57, -58.54) * mm, "end": v(-7.53, -59.41) * mm});
            skLineSegment(sketch, "E1828", {"start": v(-7.53, -59.41) * mm, "end": v(-7.45, -60.3) * mm});
            skLineSegment(sketch, "E1829", {"start": v(-7.45, -60.3) * mm, "end": v(-7.32, -61.1) * mm});
            skLineSegment(sketch, "E1830", {"start": v(-7.32, -61.1) * mm, "end": v(-7.14, -61.71) * mm});
            skLineSegment(sketch, "E1831", {"start": v(-7.14, -61.71) * mm, "end": v(-6.89, -62.03) * mm});
            skLineSegment(sketch, "E1832", {"start": v(-6.89, -62.03) * mm, "end": v(-6.83, -61.96) * mm});
            skLineSegment(sketch, "E1833", {"start": v(-6.83, -61.96) * mm, "end": v(-6.65, -61.78) * mm});
            skLineSegment(sketch, "E1834", {"start": v(-6.65, -61.78) * mm, "end": v(-6.34, -61.5) * mm});
            skLineSegment(sketch, "E1835", {"start": v(-6.34, -61.5) * mm, "end": v(-5.9, -61.17) * mm});
            skLineSegment(sketch, "E1836", {"start": v(-5.9, -61.17) * mm, "end": v(-5.32, -60.8) * mm});
            skLineSegment(sketch, "E1837", {"start": v(-5.32, -60.8) * mm, "end": v(-4.59, -60.44) * mm});
            skLineSegment(sketch, "E1838", {"start": v(-4.59, -60.44) * mm, "end": v(-3.7, -60.1) * mm});
            skLineSegment(sketch, "E1839", {"start": v(-3.7, -60.1) * mm, "end": v(-2.65, -59.83) * mm});
            skLineSegment(sketch, "E1840", {"start": v(-2.65, -59.83) * mm, "end": v(-2.68, -60.12) * mm});
            skLineSegment(sketch, "E1841", {"start": v(-2.68, -60.12) * mm, "end": v(-2.72, -60.9) * mm});
            skLineSegment(sketch, "E1842", {"start": v(-2.72, -60.9) * mm, "end": v(-2.73, -62.08) * mm});
            skLineSegment(sketch, "E1843", {"start": v(-2.73, -62.08) * mm, "end": v(-2.63, -63.51) * mm});
            skLineSegment(sketch, "E1844", {"start": v(-2.63, -63.51) * mm, "end": v(-2.38, -65.1) * mm});
            skLineSegment(sketch, "E1845", {"start": v(-2.38, -65.1) * mm, "end": v(-1.92, -66.7) * mm});
            skLineSegment(sketch, "E1846", {"start": v(-1.92, -66.7) * mm, "end": v(-1.19, -68.22) * mm});
            skLineSegment(sketch, "E1847", {"start": v(-1.19, -68.22) * mm, "end": v(-0.13, -69.53) * mm});
            skLineSegment(sketch, "E1848", {"start": v(-15.95, 41.9) * mm, "end": v(-16.7, 41.92) * mm});
            skLineSegment(sketch, "E1849", {"start": v(-16.7, 41.92) * mm, "end": v(-18.68, 41.85) * mm});
            skLineSegment(sketch, "E1850", {"start": v(-18.68, 41.85) * mm, "end": v(-21.54, 41.52) * mm});
            skLineSegment(sketch, "E1851", {"start": v(-21.54, 41.52) * mm, "end": v(-24.89, 40.75) * mm});
            skLineSegment(sketch, "E1852", {"start": v(-24.89, 40.75) * mm, "end": v(-28.36, 39.36) * mm});
            skLineSegment(sketch, "E1853", {"start": v(-28.36, 39.36) * mm, "end": v(-31.58, 37.18) * mm});
            skLineSegment(sketch, "E1854", {"start": v(-31.58, 37.18) * mm, "end": v(-34.17, 34.02) * mm});
            skLineSegment(sketch, "E1855", {"start": v(-34.17, 34.02) * mm, "end": v(-35.76, 29.72) * mm});
            skLineSegment(sketch, "E1856", {"start": v(-35.76, 29.72) * mm, "end": v(-36.07, 29) * mm});
            skLineSegment(sketch, "E1857", {"start": v(-36.07, 29) * mm, "end": v(-36.9, 26.94) * mm});
            skLineSegment(sketch, "E1858", {"start": v(-36.9, 26.94) * mm, "end": v(-38.1, 23.7) * mm});
            skLineSegment(sketch, "E1859", {"start": v(-38.1, 23.7) * mm, "end": v(-39.5, 19.43) * mm});
            skLineSegment(sketch, "E1860", {"start": v(-39.5, 19.43) * mm, "end": v(-40.93, 14.28) * mm});
            skLineSegment(sketch, "E1861", {"start": v(-40.93, 14.28) * mm, "end": v(-42.23, 8.42) * mm});
            skLineSegment(sketch, "E1862", {"start": v(-42.23, 8.42) * mm, "end": v(-43.24, 2) * mm});
            skLineSegment(sketch, "E1863", {"start": v(-43.24, 2) * mm, "end": v(-43.8, -4.84) * mm});
            skLineSegment(sketch, "E1864", {"start": v(-43.8, -4.84) * mm, "end": v(-44.16, -4.98) * mm});
            skLineSegment(sketch, "E1865", {"start": v(-44.16, -4.98) * mm, "end": v(-45.14, -5.38) * mm});
            skLineSegment(sketch, "E1866", {"start": v(-45.14, -5.38) * mm, "end": v(-46.56, -6) * mm});
            skLineSegment(sketch, "E1867", {"start": v(-46.56, -6) * mm, "end": v(-48.25, -6.84) * mm});
            skLineSegment(sketch, "E1868", {"start": v(-48.25, -6.84) * mm, "end": v(-50.05, -7.85) * mm});
            skLineSegment(sketch, "E1869", {"start": v(-50.05, -7.85) * mm, "end": v(-51.78, -9.02) * mm});
            skLineSegment(sketch, "E1870", {"start": v(-51.78, -9.02) * mm, "end": v(-53.28, -10.31) * mm});
            skLineSegment(sketch, "E1871", {"start": v(-53.28, -10.31) * mm, "end": v(-54.38, -11.7) * mm});
            skLineSegment(sketch, "E1872", {"start": v(-54.38, -11.7) * mm, "end": v(-54.2, -11) * mm});
            skLineSegment(sketch, "E1873", {"start": v(-54.2, -11) * mm, "end": v(-53.7, -9.1) * mm});
            skLineSegment(sketch, "E1874", {"start": v(-53.7, -9.1) * mm, "end": v(-52.9, -6.33) * mm});
            skLineSegment(sketch, "E1875", {"start": v(-52.9, -6.33) * mm, "end": v(-51.8, -3) * mm});
            skLineSegment(sketch, "E1876", {"start": v(-51.8, -3) * mm, "end": v(-50.45, 0.54) * mm});
            skLineSegment(sketch, "E1877", {"start": v(-50.45, 0.54) * mm, "end": v(-48.85, 4) * mm});
            skLineSegment(sketch, "E1878", {"start": v(-48.85, 4) * mm, "end": v(-47.04, 7.03) * mm});
            skLineSegment(sketch, "E1879", {"start": v(-47.04, 7.03) * mm, "end": v(-45.03, 9.31) * mm});
            skLineSegment(sketch, "E1880", {"start": v(-45.03, 9.31) * mm, "end": v(-45.74, 9.5) * mm});
            skLineSegment(sketch, "E1881", {"start": v(-45.74, 9.5) * mm, "end": v(-47.7, 9.86) * mm});
            skLineSegment(sketch, "E1882", {"start": v(-47.7, 9.86) * mm, "end": v(-50.64, 10.15) * mm});
            skLineSegment(sketch, "E1883", {"start": v(-50.64, 10.15) * mm, "end": v(-54.33, 10.08) * mm});
            skLineSegment(sketch, "E1884", {"start": v(-54.33, 10.08) * mm, "end": v(-58.5, 9.4) * mm});
            skLineSegment(sketch, "E1885", {"start": v(-58.5, 9.4) * mm, "end": v(-62.92, 7.85) * mm});
            skLineSegment(sketch, "E1886", {"start": v(-62.92, 7.85) * mm, "end": v(-67.32, 5.14) * mm});
            skLineSegment(sketch, "E1887", {"start": v(-67.32, 5.14) * mm, "end": v(-71.44, 1.02) * mm});
            skLineSegment(sketch, "E1888", {"start": v(-71.44, 1.02) * mm, "end": v(-71.2, 1.95) * mm});
            skLineSegment(sketch, "E1889", {"start": v(-71.2, 1.95) * mm, "end": v(-70.46, 4.45) * mm});
            skLineSegment(sketch, "E1890", {"start": v(-70.46, 4.45) * mm, "end": v(-69.28, 8.08) * mm});
            skLineSegment(sketch, "E1891", {"start": v(-69.28, 8.08) * mm, "end": v(-67.68, 12.43) * mm});
            skLineSegment(sketch, "E1892", {"start": v(-67.68, 12.43) * mm, "end": v(-65.68, 17.07) * mm});
            skLineSegment(sketch, "E1893", {"start": v(-65.68, 17.07) * mm, "end": v(-63.3, 21.56) * mm});
            skLineSegment(sketch, "E1894", {"start": v(-63.3, 21.56) * mm, "end": v(-60.6, 25.48) * mm});
            skLineSegment(sketch, "E1895", {"start": v(-60.6, 25.48) * mm, "end": v(-57.56, 28.4) * mm});
            skLineSegment(sketch, "E1896", {"start": v(-57.56, 28.4) * mm, "end": v(-58.07, 28.35) * mm});
            skLineSegment(sketch, "E1897", {"start": v(-58.07, 28.35) * mm, "end": v(-59.45, 28.18) * mm});
            skLineSegment(sketch, "E1898", {"start": v(-59.45, 28.18) * mm, "end": v(-61.48, 27.87) * mm});
            skLineSegment(sketch, "E1899", {"start": v(-61.48, 27.87) * mm, "end": v(-63.95, 27.38) * mm});
            skLineSegment(sketch, "E1900", {"start": v(-63.95, 27.38) * mm, "end": v(-66.61, 26.67) * mm});
            skLineSegment(sketch, "E1901", {"start": v(-66.61, 26.67) * mm, "end": v(-69.27, 25.73) * mm});
            skLineSegment(sketch, "E1902", {"start": v(-69.27, 25.73) * mm, "end": v(-71.7, 24.5) * mm});
            skLineSegment(sketch, "E1903", {"start": v(-71.7, 24.5) * mm, "end": v(-73.66, 22.98) * mm});
            skLineSegment(sketch, "E1904", {"start": v(-73.66, 22.98) * mm, "end": v(-73.35, 23.91) * mm});
            skLineSegment(sketch, "E1905", {"start": v(-73.35, 23.91) * mm, "end": v(-72.33, 26.49) * mm});
            skLineSegment(sketch, "E1906", {"start": v(-72.33, 26.49) * mm, "end": v(-70.4, 30.39) * mm});
            skLineSegment(sketch, "E1907", {"start": v(-70.4, 30.39) * mm, "end": v(-67.43, 35.28) * mm});
            skLineSegment(sketch, "E1908", {"start": v(-67.43, 35.28) * mm, "end": v(-63.23, 40.84) * mm});
            skLineSegment(sketch, "E1909", {"start": v(-63.23, 40.84) * mm, "end": v(-57.63, 46.73) * mm});
            skLineSegment(sketch, "E1910", {"start": v(-57.63, 46.73) * mm, "end": v(-50.47, 52.63) * mm});
            skLineSegment(sketch, "E1911", {"start": v(-50.47, 52.63) * mm, "end": v(-41.57, 58.22) * mm});
            skLineSegment(sketch, "E1912", {"start": v(-41.57, 58.22) * mm, "end": v(-40.86, 58.57) * mm});
            skLineSegment(sketch, "E1913", {"start": v(-40.86, 58.57) * mm, "end": v(-38.93, 59.43) * mm});
            skLineSegment(sketch, "E1914", {"start": v(-38.93, 59.43) * mm, "end": v(-36, 60.49) * mm});
            skLineSegment(sketch, "E1915", {"start": v(-36, 60.49) * mm, "end": v(-32.33, 61.44) * mm});
            skLineSegment(sketch, "E1916", {"start": v(-32.33, 61.44) * mm, "end": v(-28.16, 62) * mm});
            skLineSegment(sketch, "E1917", {"start": v(-28.16, 62) * mm, "end": v(-23.75, 61.85) * mm});
            skLineSegment(sketch, "E1918", {"start": v(-23.75, 61.85) * mm, "end": v(-19.35, 60.69) * mm});
            skLineSegment(sketch, "E1919", {"start": v(-19.35, 60.69) * mm, "end": v(-15.19, 58.22) * mm});
            skLineSegment(sketch, "E1920", {"start": v(-15.19, 58.22) * mm, "end": v(-15.8, 58.47) * mm});
            skLineSegment(sketch, "E1921", {"start": v(-15.8, 58.47) * mm, "end": v(-17.52, 59.07) * mm});
            skLineSegment(sketch, "E1922", {"start": v(-17.52, 59.07) * mm, "end": v(-20.14, 59.76) * mm});
            skLineSegment(sketch, "E1923", {"start": v(-20.14, 59.76) * mm, "end": v(-23.45, 60.3) * mm});
            skLineSegment(sketch, "E1924", {"start": v(-23.45, 60.3) * mm, "end": v(-27.25, 60.43) * mm});
            skLineSegment(sketch, "E1925", {"start": v(-27.25, 60.43) * mm, "end": v(-31.35, 59.91) * mm});
            skLineSegment(sketch, "E1926", {"start": v(-31.35, 59.91) * mm, "end": v(-35.52, 58.5) * mm});
            skLineSegment(sketch, "E1927", {"start": v(-35.52, 58.5) * mm, "end": v(-39.58, 55.92) * mm});
            skLineSegment(sketch, "E1928", {"start": v(-39.58, 55.92) * mm, "end": v(-42.88, 52.97) * mm});
            skLineSegment(sketch, "E1929", {"start": v(-42.88, 52.97) * mm, "end": v(-45.03, 50.53) * mm});
            skLineSegment(sketch, "E1930", {"start": v(-45.03, 50.53) * mm, "end": v(-46.22, 48.55) * mm});
            skLineSegment(sketch, "E1931", {"start": v(-46.22, 48.55) * mm, "end": v(-46.64, 47.01) * mm});
            skLineSegment(sketch, "E1932", {"start": v(-46.64, 47.01) * mm, "end": v(-46.48, 45.85) * mm});
            skLineSegment(sketch, "E1933", {"start": v(-46.48, 45.85) * mm, "end": v(-45.93, 45.04) * mm});
            skLineSegment(sketch, "E1934", {"start": v(-45.93, 45.04) * mm, "end": v(-45.18, 44.53) * mm});
            skLineSegment(sketch, "E1935", {"start": v(-45.18, 44.53) * mm, "end": v(-44.42, 44.27) * mm});
            skLineSegment(sketch, "E1936", {"start": v(-44.42, 44.27) * mm, "end": v(-42.66, 44.51) * mm});
            skLineSegment(sketch, "E1937", {"start": v(-42.66, 44.51) * mm, "end": v(-39.1, 45.32) * mm});
            skLineSegment(sketch, "E1938", {"start": v(-39.1, 45.32) * mm, "end": v(-34.26, 46.42) * mm});
            skLineSegment(sketch, "E1939", {"start": v(-34.26, 46.42) * mm, "end": v(-28.63, 47.54) * mm});
            skLineSegment(sketch, "E1940", {"start": v(-28.63, 47.54) * mm, "end": v(-22.73, 48.4) * mm});
            skLineSegment(sketch, "E1941", {"start": v(-22.73, 48.4) * mm, "end": v(-17.07, 48.7) * mm});
            skLineSegment(sketch, "E1942", {"start": v(-17.07, 48.7) * mm, "end": v(-12.14, 48.2) * mm});
            skLineSegment(sketch, "E1943", {"start": v(-12.14, 48.2) * mm, "end": v(-8.46, 46.6) * mm});
            skLineSegment(sketch, "E1944", {"start": v(-8.46, 46.6) * mm, "end": v(-9.05, 46.72) * mm});
            skLineSegment(sketch, "E1945", {"start": v(-9.05, 46.72) * mm, "end": v(-10.7, 46.98) * mm});
            skLineSegment(sketch, "E1946", {"start": v(-10.7, 46.98) * mm, "end": v(-13.22, 47.23) * mm});
            skLineSegment(sketch, "E1947", {"start": v(-13.22, 47.23) * mm, "end": v(-16.46, 47.32) * mm});
            skLineSegment(sketch, "E1948", {"start": v(-16.46, 47.32) * mm, "end": v(-20.24, 47.1) * mm});
            skLineSegment(sketch, "E1949", {"start": v(-20.24, 47.1) * mm, "end": v(-24.4, 46.43) * mm});
            skLineSegment(sketch, "E1950", {"start": v(-24.4, 46.43) * mm, "end": v(-28.74, 45.16) * mm});
            skLineSegment(sketch, "E1951", {"start": v(-28.74, 45.16) * mm, "end": v(-33.12, 43.13) * mm});
            skLineSegment(sketch, "E1952", {"start": v(-33.12, 43.13) * mm, "end": v(-32.77, 43.25) * mm});
            skLineSegment(sketch, "E1953", {"start": v(-32.77, 43.25) * mm, "end": v(-31.76, 43.52) * mm});
            skLineSegment(sketch, "E1954", {"start": v(-31.76, 43.52) * mm, "end": v(-30.17, 43.84) * mm});
            skLineSegment(sketch, "E1955", {"start": v(-30.17, 43.84) * mm, "end": v(-28.07, 44.07) * mm});
            skLineSegment(sketch, "E1956", {"start": v(-28.07, 44.07) * mm, "end": v(-25.52, 44.12) * mm});
            skLineSegment(sketch, "E1957", {"start": v(-25.52, 44.12) * mm, "end": v(-22.6, 43.85) * mm});
            skLineSegment(sketch, "E1958", {"start": v(-22.6, 43.85) * mm, "end": v(-19.4, 43.15) * mm});
            skLineSegment(sketch, "E1959", {"start": v(-19.4, 43.15) * mm, "end": v(-15.95, 41.9) * mm});
            skLineSegment(sketch, "E1960", {"start": v(-57.16, 70.98) * mm, "end": v(-56.95, 70.78) * mm});
            skLineSegment(sketch, "E1961", {"start": v(-56.95, 70.78) * mm, "end": v(-56.37, 70.28) * mm});
            skLineSegment(sketch, "E1962", {"start": v(-56.37, 70.28) * mm, "end": v(-55.43, 69.55) * mm});
            skLineSegment(sketch, "E1963", {"start": v(-55.43, 69.55) * mm, "end": v(-54.18, 68.72) * mm});
            skLineSegment(sketch, "E1964", {"start": v(-54.18, 68.72) * mm, "end": v(-52.63, 67.89) * mm});
            skLineSegment(sketch, "E1965", {"start": v(-52.63, 67.89) * mm, "end": v(-50.84, 67.14) * mm});
            skLineSegment(sketch, "E1966", {"start": v(-50.84, 67.14) * mm, "end": v(-48.82, 66.6) * mm});
            skLineSegment(sketch, "E1967", {"start": v(-48.82, 66.6) * mm, "end": v(-46.6, 66.37) * mm});
            skLineSegment(sketch, "E1968", {"start": v(-46.6, 66.37) * mm, "end": v(-44, 66.62) * mm});
            skLineSegment(sketch, "E1969", {"start": v(-44, 66.62) * mm, "end": v(-40.84, 67.28) * mm});
            skLineSegment(sketch, "E1970", {"start": v(-40.84, 67.28) * mm, "end": v(-37.2, 68.07) * mm});
            skLineSegment(sketch, "E1971", {"start": v(-37.2, 68.07) * mm, "end": v(-33.2, 68.7) * mm});
            skLineSegment(sketch, "E1972", {"start": v(-33.2, 68.7) * mm, "end": v(-28.9, 68.88) * mm});
            skLineSegment(sketch, "E1973", {"start": v(-28.9, 68.88) * mm, "end": v(-24.39, 68.31) * mm});
            skLineSegment(sketch, "E1974", {"start": v(-24.39, 68.31) * mm, "end": v(-19.77, 66.73) * mm});
            skLineSegment(sketch, "E1975", {"start": v(-19.77, 66.73) * mm, "end": v(-15.12, 63.82) * mm});
            skLineSegment(sketch, "E1976", {"start": v(-15.12, 63.82) * mm, "end": v(-15.18, 64.03) * mm});
            skLineSegment(sketch, "E1977", {"start": v(-15.18, 64.03) * mm, "end": v(-15.37, 64.59) * mm});
            skLineSegment(sketch, "E1978", {"start": v(-15.37, 64.59) * mm, "end": v(-15.7, 65.4) * mm});
            skLineSegment(sketch, "E1979", {"start": v(-15.7, 65.4) * mm, "end": v(-16.16, 66.38) * mm});
            skLineSegment(sketch, "E1980", {"start": v(-16.16, 66.38) * mm, "end": v(-16.77, 67.41) * mm});
            skLineSegment(sketch, "E1981", {"start": v(-16.77, 67.41) * mm, "end": v(-17.54, 68.42) * mm});
            skLineSegment(sketch, "E1982", {"start": v(-17.54, 68.42) * mm, "end": v(-18.47, 69.3) * mm});
            skLineSegment(sketch, "E1983", {"start": v(-18.47, 69.3) * mm, "end": v(-19.57, 69.94) * mm});
            skLineSegment(sketch, "E1984", {"start": v(-19.57, 69.94) * mm, "end": v(-19.1, 69.94) * mm});
            skLineSegment(sketch, "E1985", {"start": v(-19.1, 69.94) * mm, "end": v(-17.81, 69.92) * mm});
            skLineSegment(sketch, "E1986", {"start": v(-17.81, 69.92) * mm, "end": v(-15.94, 69.84) * mm});
            skLineSegment(sketch, "E1987", {"start": v(-15.94, 69.84) * mm, "end": v(-13.69, 69.67) * mm});
            skLineSegment(sketch, "E1988", {"start": v(-13.69, 69.67) * mm, "end": v(-11.28, 69.38) * mm});
            skLineSegment(sketch, "E1989", {"start": v(-11.28, 69.38) * mm, "end": v(-8.93, 68.93) * mm});
            skLineSegment(sketch, "E1990", {"start": v(-8.93, 68.93) * mm, "end": v(-6.86, 68.28) * mm});
            skLineSegment(sketch, "E1991", {"start": v(-6.86, 68.28) * mm, "end": v(-5.28, 67.4) * mm});
            skLineSegment(sketch, "E1992", {"start": v(-5.28, 67.4) * mm, "end": v(-5.14, 67.48) * mm});
            skLineSegment(sketch, "E1993", {"start": v(-5.14, 67.48) * mm, "end": v(-4.77, 67.7) * mm});
            skLineSegment(sketch, "E1994", {"start": v(-4.77, 67.7) * mm, "end": v(-4.24, 68.04) * mm});
            skLineSegment(sketch, "E1995", {"start": v(-4.24, 68.04) * mm, "end": v(-3.63, 68.48) * mm});
            skLineSegment(sketch, "E1996", {"start": v(-3.63, 68.48) * mm, "end": v(-3, 69.02) * mm});
            skLineSegment(sketch, "E1997", {"start": v(-3, 69.02) * mm, "end": v(-2.42, 69.62) * mm});
            skLineSegment(sketch, "E1998", {"start": v(-2.42, 69.62) * mm, "end": v(-1.97, 70.28) * mm});
            skLineSegment(sketch, "E1999", {"start": v(-1.97, 70.28) * mm, "end": v(-1.73, 70.98) * mm});
            skLineSegment(sketch, "E2000", {"start": v(-1.73, 70.98) * mm, "end": v(-2.53, 71.59) * mm});
            skLineSegment(sketch, "E2001", {"start": v(-2.53, 71.59) * mm, "end": v(-4.97, 72) * mm});
            skLineSegment(sketch, "E2002", {"start": v(-4.97, 72) * mm, "end": v(-8.67, 72.18) * mm});
            skLineSegment(sketch, "E2003", {"start": v(-8.67, 72.18) * mm, "end": v(-13.3, 72.14) * mm});
            skLineSegment(sketch, "E2004", {"start": v(-13.3, 72.14) * mm, "end": v(-18.5, 71.86) * mm});
            skLineSegment(sketch, "E2005", {"start": v(-18.5, 71.86) * mm, "end": v(-23.91, 71.32) * mm});
            skLineSegment(sketch, "E2006", {"start": v(-23.91, 71.32) * mm, "end": v(-29.2, 70.51) * mm});
            skLineSegment(sketch, "E2007", {"start": v(-29.2, 70.51) * mm, "end": v(-34, 69.43) * mm});
            skLineSegment(sketch, "E2008", {"start": v(-34, 69.43) * mm, "end": v(-36.42, 68.91) * mm});
            skLineSegment(sketch, "E2009", {"start": v(-36.42, 68.91) * mm, "end": v(-39.44, 68.51) * mm});
            skLineSegment(sketch, "E2010", {"start": v(-39.44, 68.51) * mm, "end": v(-42.84, 68.27) * mm});
            skLineSegment(sketch, "E2011", {"start": v(-42.84, 68.27) * mm, "end": v(-46.38, 68.23) * mm});
            skLineSegment(sketch, "E2012", {"start": v(-46.38, 68.23) * mm, "end": v(-49.82, 68.43) * mm});
            skLineSegment(sketch, "E2013", {"start": v(-49.82, 68.43) * mm, "end": v(-52.92, 68.93) * mm});
            skLineSegment(sketch, "E2014", {"start": v(-52.92, 68.93) * mm, "end": v(-55.45, 69.77) * mm});
            skLineSegment(sketch, "E2015", {"start": v(-55.45, 69.77) * mm, "end": v(-57.16, 70.98) * mm});
            skLineSegment(sketch, "E2016", {"start": v(42.38, 58.22) * mm, "end": v(43.9, 57.8) * mm});
            skLineSegment(sketch, "E2017", {"start": v(43.9, 57.8) * mm, "end": v(47.94, 56.41) * mm});
            skLineSegment(sketch, "E2018", {"start": v(47.94, 56.41) * mm, "end": v(53.69, 53.77) * mm});
            skLineSegment(sketch, "E2019", {"start": v(53.69, 53.77) * mm, "end": v(60.36, 49.62) * mm});
            skLineSegment(sketch, "E2020", {"start": v(60.36, 49.62) * mm, "end": v(67.15, 43.72) * mm});
            skLineSegment(sketch, "E2021", {"start": v(67.15, 43.72) * mm, "end": v(73.27, 35.81) * mm});
            skLineSegment(sketch, "E2022", {"start": v(73.27, 35.81) * mm, "end": v(77.92, 25.64) * mm});
            skLineSegment(sketch, "E2023", {"start": v(77.92, 25.64) * mm, "end": v(80.3, 12.94) * mm});
            skLineSegment(sketch, "E2024", {"start": v(80.3, 12.94) * mm, "end": v(79.98, 13.27) * mm});
            skLineSegment(sketch, "E2025", {"start": v(79.98, 13.27) * mm, "end": v(79.06, 14.14) * mm});
            skLineSegment(sketch, "E2026", {"start": v(79.06, 14.14) * mm, "end": v(77.66, 15.4) * mm});
            skLineSegment(sketch, "E2027", {"start": v(77.66, 15.4) * mm, "end": v(75.86, 16.9) * mm});
            skLineSegment(sketch, "E2028", {"start": v(75.86, 16.9) * mm, "end": v(73.77, 18.47) * mm});
            skLineSegment(sketch, "E2029", {"start": v(73.77, 18.47) * mm, "end": v(71.5, 19.96) * mm});
            skLineSegment(sketch, "E2030", {"start": v(71.5, 19.96) * mm, "end": v(69.11, 21.2) * mm});
            skLineSegment(sketch, "E2031", {"start": v(69.11, 21.2) * mm, "end": v(66.73, 22.03) * mm});
            skLineSegment(sketch, "E2032", {"start": v(66.73, 22.03) * mm, "end": v(67.14, 21.53) * mm});
            skLineSegment(sketch, "E2033", {"start": v(67.14, 21.53) * mm, "end": v(68.2, 20) * mm});
            skLineSegment(sketch, "E2034", {"start": v(68.2, 20) * mm, "end": v(69.7, 17.46) * mm});
            skLineSegment(sketch, "E2035", {"start": v(69.7, 17.46) * mm, "end": v(71.46, 13.9) * mm});
            skLineSegment(sketch, "E2036", {"start": v(71.46, 13.9) * mm, "end": v(73.23, 9.34) * mm});
            skLineSegment(sketch, "E2037", {"start": v(73.23, 9.34) * mm, "end": v(74.83, 3.75) * mm});
            skLineSegment(sketch, "E2038", {"start": v(74.83, 3.75) * mm, "end": v(76.04, -2.85) * mm});
            skLineSegment(sketch, "E2039", {"start": v(76.04, -2.85) * mm, "end": v(76.64, -10.46) * mm});
            skLineSegment(sketch, "E2040", {"start": v(76.64, -10.46) * mm, "end": v(75.95, -9.8) * mm});
            skLineSegment(sketch, "E2041", {"start": v(75.95, -9.8) * mm, "end": v(74.05, -8.04) * mm});
            skLineSegment(sketch, "E2042", {"start": v(74.05, -8.04) * mm, "end": v(71.21, -5.53) * mm});
            skLineSegment(sketch, "E2043", {"start": v(71.21, -5.53) * mm, "end": v(67.7, -2.61) * mm});
            skLineSegment(sketch, "E2044", {"start": v(67.7, -2.61) * mm, "end": v(63.78, 0.36) * mm});
            skLineSegment(sketch, "E2045", {"start": v(63.78, 0.36) * mm, "end": v(59.73, 3.04) * mm});
            skLineSegment(sketch, "E2046", {"start": v(59.73, 3.04) * mm, "end": v(55.8, 5.08) * mm});
            skLineSegment(sketch, "E2047", {"start": v(55.8, 5.08) * mm, "end": v(52.29, 6.13) * mm});
            skLineSegment(sketch, "E2048", {"start": v(52.29, 6.13) * mm, "end": v(52.68, 5.6) * mm});
            skLineSegment(sketch, "E2049", {"start": v(52.68, 5.6) * mm, "end": v(53.7, 4.06) * mm});
            skLineSegment(sketch, "E2050", {"start": v(53.7, 4.06) * mm, "end": v(55.16, 1.55) * mm});
            skLineSegment(sketch, "E2051", {"start": v(55.16, 1.55) * mm, "end": v(56.83, -1.9) * mm});
            skLineSegment(sketch, "E2052", {"start": v(56.83, -1.9) * mm, "end": v(58.5, -6.21) * mm});
            skLineSegment(sketch, "E2053", {"start": v(58.5, -6.21) * mm, "end": v(59.95, -11.37) * mm});
            skLineSegment(sketch, "E2054", {"start": v(59.95, -11.37) * mm, "end": v(60.98, -17.32) * mm});
            skLineSegment(sketch, "E2055", {"start": v(60.98, -17.32) * mm, "end": v(61.37, -24) * mm});
            skLineSegment(sketch, "E2056", {"start": v(61.37, -24) * mm, "end": v(60.81, -23.48) * mm});
            skLineSegment(sketch, "E2057", {"start": v(60.81, -23.48) * mm, "end": v(59.23, -22.1) * mm});
            skLineSegment(sketch, "E2058", {"start": v(59.23, -22.1) * mm, "end": v(56.71, -20.15) * mm});
            skLineSegment(sketch, "E2059", {"start": v(56.71, -20.15) * mm, "end": v(53.38, -17.9) * mm});
            skLineSegment(sketch, "E2060", {"start": v(53.38, -17.9) * mm, "end": v(49.34, -15.67) * mm});
            skLineSegment(sketch, "E2061", {"start": v(49.34, -15.67) * mm, "end": v(44.69, -13.72) * mm});
            skLineSegment(sketch, "E2062", {"start": v(44.69, -13.72) * mm, "end": v(39.54, -12.34) * mm});
            skLineSegment(sketch, "E2063", {"start": v(39.54, -12.34) * mm, "end": v(34.01, -11.81) * mm});
            skLineSegment(sketch, "E2064", {"start": v(34.01, -11.81) * mm, "end": v(34.26, -11.44) * mm});
            skLineSegment(sketch, "E2065", {"start": v(34.26, -11.44) * mm, "end": v(34.91, -10.37) * mm});
            skLineSegment(sketch, "E2066", {"start": v(34.91, -10.37) * mm, "end": v(35.83, -8.63) * mm});
            skLineSegment(sketch, "E2067", {"start": v(35.83, -8.63) * mm, "end": v(36.88, -6.27) * mm});
            skLineSegment(sketch, "E2068", {"start": v(36.88, -6.27) * mm, "end": v(37.92, -3.34) * mm});
            skLineSegment(sketch, "E2069", {"start": v(37.92, -3.34) * mm, "end": v(38.8, 0.11) * mm});
            skLineSegment(sketch, "E2070", {"start": v(38.8, 0.11) * mm, "end": v(39.4, 4.05) * mm});
            skLineSegment(sketch, "E2071", {"start": v(39.4, 4.05) * mm, "end": v(39.58, 8.42) * mm});
            skLineSegment(sketch, "E2072", {"start": v(39.58, 8.42) * mm, "end": v(39.74, 8.01) * mm});
            skLineSegment(sketch, "E2073", {"start": v(39.74, 8.01) * mm, "end": v(40.13, 6.89) * mm});
            skLineSegment(sketch, "E2074", {"start": v(40.13, 6.89) * mm, "end": v(40.68, 5.2) * mm});
            skLineSegment(sketch, "E2075", {"start": v(40.68, 5.2) * mm, "end": v(41.28, 3.1) * mm});
            skLineSegment(sketch, "E2076", {"start": v(41.28, 3.1) * mm, "end": v(41.84, 0.73) * mm});
            skLineSegment(sketch, "E2077", {"start": v(41.84, 0.73) * mm, "end": v(42.28, -1.76) * mm});
            skLineSegment(sketch, "E2078", {"start": v(42.28, -1.76) * mm, "end": v(42.49, -4.2) * mm});
            skLineSegment(sketch, "E2079", {"start": v(42.49, -4.2) * mm, "end": v(42.38, -6.45) * mm});
            skLineSegment(sketch, "E2080", {"start": v(42.38, -6.45) * mm, "end": v(42.87, -6.68) * mm});
            skLineSegment(sketch, "E2081", {"start": v(42.87, -6.68) * mm, "end": v(44.2, -7.33) * mm});
            skLineSegment(sketch, "E2082", {"start": v(44.2, -7.33) * mm, "end": v(46.1, -8.3) * mm});
            skLineSegment(sketch, "E2083", {"start": v(46.1, -8.3) * mm, "end": v(48.39, -9.55) * mm});
            skLineSegment(sketch, "E2084", {"start": v(48.39, -9.55) * mm, "end": v(50.8, -10.97) * mm});
            skLineSegment(sketch, "E2085", {"start": v(50.8, -10.97) * mm, "end": v(53.14, -12.5) * mm});
            skLineSegment(sketch, "E2086", {"start": v(53.14, -12.5) * mm, "end": v(55.15, -14.04) * mm});
            skLineSegment(sketch, "E2087", {"start": v(55.15, -14.04) * mm, "end": v(56.62, -15.54) * mm});
            skLineSegment(sketch, "E2088", {"start": v(56.62, -15.54) * mm, "end": v(56.5, -14.82) * mm});
            skLineSegment(sketch, "E2089", {"start": v(56.5, -14.82) * mm, "end": v(56.14, -12.85) * mm});
            skLineSegment(sketch, "E2090", {"start": v(56.14, -12.85) * mm, "end": v(55.5, -9.94) * mm});
            skLineSegment(sketch, "E2091", {"start": v(55.5, -9.94) * mm, "end": v(54.57, -6.39) * mm});
            skLineSegment(sketch, "E2092", {"start": v(54.57, -6.39) * mm, "end": v(53.32, -2.5) * mm});
            skLineSegment(sketch, "E2093", {"start": v(53.32, -2.5) * mm, "end": v(51.73, 1.41) * mm});
            skLineSegment(sketch, "E2094", {"start": v(51.73, 1.41) * mm, "end": v(49.76, 5.06) * mm});
            skLineSegment(sketch, "E2095", {"start": v(49.76, 5.06) * mm, "end": v(47.4, 8.13) * mm});
            skLineSegment(sketch, "E2096", {"start": v(47.4, 8.13) * mm, "end": v(47.95, 8.25) * mm});
            skLineSegment(sketch, "E2097", {"start": v(47.95, 8.25) * mm, "end": v(49.51, 8.47) * mm});
            skLineSegment(sketch, "E2098", {"start": v(49.51, 8.47) * mm, "end": v(51.96, 8.53) * mm});
            skLineSegment(sketch, "E2099", {"start": v(51.96, 8.53) * mm, "end": v(55.17, 8.18) * mm});
            skLineSegment(sketch, "E2100", {"start": v(55.17, 8.18) * mm, "end": v(59, 7.17) * mm});
            skLineSegment(sketch, "E2101", {"start": v(59, 7.17) * mm, "end": v(63.34, 5.26) * mm});
            skLineSegment(sketch, "E2102", {"start": v(63.34, 5.26) * mm, "end": v(68.04, 2.2) * mm});
            skLineSegment(sketch, "E2103", {"start": v(68.04, 2.2) * mm, "end": v(72.98, -2.27) * mm});
            skLineSegment(sketch, "E2104", {"start": v(72.98, -2.27) * mm, "end": v(72.8, -1.39) * mm});
            skLineSegment(sketch, "E2105", {"start": v(72.8, -1.39) * mm, "end": v(72.22, 1.01) * mm});
            skLineSegment(sketch, "E2106", {"start": v(72.22, 1.01) * mm, "end": v(71.28, 4.55) * mm});
            skLineSegment(sketch, "E2107", {"start": v(71.28, 4.55) * mm, "end": v(69.97, 8.84) * mm});
            skLineSegment(sketch, "E2108", {"start": v(69.97, 8.84) * mm, "end": v(68.3, 13.5) * mm});
            skLineSegment(sketch, "E2109", {"start": v(68.3, 13.5) * mm, "end": v(66.27, 18.16) * mm});
            skLineSegment(sketch, "E2110", {"start": v(66.27, 18.16) * mm, "end": v(63.89, 22.44) * mm});
            skLineSegment(sketch, "E2111", {"start": v(63.89, 22.44) * mm, "end": v(61.16, 25.95) * mm});
            skLineSegment(sketch, "E2112", {"start": v(61.16, 25.95) * mm, "end": v(61.47, 25.91) * mm});
            skLineSegment(sketch, "E2113", {"start": v(61.47, 25.91) * mm, "end": v(62.33, 25.78) * mm});
            skLineSegment(sketch, "E2114", {"start": v(62.33, 25.78) * mm, "end": v(63.7, 25.5) * mm});
            skLineSegment(sketch, "E2115", {"start": v(63.7, 25.5) * mm, "end": v(65.47, 25.03) * mm});
            skLineSegment(sketch, "E2116", {"start": v(65.47, 25.03) * mm, "end": v(67.6, 24.32) * mm});
            skLineSegment(sketch, "E2117", {"start": v(67.6, 24.32) * mm, "end": v(70, 23.33) * mm});
            skLineSegment(sketch, "E2118", {"start": v(70, 23.33) * mm, "end": v(72.62, 22.01) * mm});
            skLineSegment(sketch, "E2119", {"start": v(72.62, 22.01) * mm, "end": v(75.36, 20.32) * mm});
            skLineSegment(sketch, "E2120", {"start": v(75.36, 20.32) * mm, "end": v(75.07, 21.49) * mm});
            skLineSegment(sketch, "E2121", {"start": v(75.07, 21.49) * mm, "end": v(74.06, 24.67) * mm});
            skLineSegment(sketch, "E2122", {"start": v(74.06, 24.67) * mm, "end": v(72.16, 29.36) * mm});
            skLineSegment(sketch, "E2123", {"start": v(72.16, 29.36) * mm, "end": v(69.15, 35.07) * mm});
            skLineSegment(sketch, "E2124", {"start": v(69.15, 35.07) * mm, "end": v(64.87, 41.31) * mm});
            skLineSegment(sketch, "E2125", {"start": v(64.87, 41.31) * mm, "end": v(59.1, 47.58) * mm});
            skLineSegment(sketch, "E2126", {"start": v(59.1, 47.58) * mm, "end": v(51.67, 53.38) * mm});
            skLineSegment(sketch, "E2127", {"start": v(51.67, 53.38) * mm, "end": v(42.38, 58.22) * mm});
            skLineSegment(sketch, "E2128", {"start": v(34, 71.13) * mm, "end": v(35.45, 71.55) * mm});
            skLineSegment(sketch, "E2129", {"start": v(35.45, 71.55) * mm, "end": v(37.02, 71.87) * mm});
            skLineSegment(sketch, "E2130", {"start": v(37.02, 71.87) * mm, "end": v(38.7, 72.09) * mm});
            skLineSegment(sketch, "E2131", {"start": v(38.7, 72.09) * mm, "end": v(40.46, 72.24) * mm});
            skLineSegment(sketch, "E2132", {"start": v(40.46, 72.24) * mm, "end": v(42.3, 72.34) * mm});
            skLineSegment(sketch, "E2133", {"start": v(42.3, 72.34) * mm, "end": v(44.17, 72.4) * mm});
            skLineSegment(sketch, "E2134", {"start": v(44.17, 72.4) * mm, "end": v(46.08, 72.47) * mm});
            skLineSegment(sketch, "E2135", {"start": v(46.08, 72.47) * mm, "end": v(48, 72.55) * mm});
            skLineSegment(sketch, "E2136", {"start": v(48, 72.55) * mm, "end": v(49.25, 72.7) * mm});
            skLineSegment(sketch, "E2137", {"start": v(49.25, 72.7) * mm, "end": v(50.61, 73.01) * mm});
            skLineSegment(sketch, "E2138", {"start": v(50.61, 73.01) * mm, "end": v(52.07, 73.37) * mm});
            skLineSegment(sketch, "E2139", {"start": v(52.07, 73.37) * mm, "end": v(53.6, 73.69) * mm});
            skLineSegment(sketch, "E2140", {"start": v(53.6, 73.69) * mm, "end": v(55.2, 73.88) * mm});
            skLineSegment(sketch, "E2141", {"start": v(55.2, 73.88) * mm, "end": v(56.84, 73.85) * mm});
            skLineSegment(sketch, "E2142", {"start": v(56.84, 73.85) * mm, "end": v(58.52, 73.5) * mm});
            skLineSegment(sketch, "E2143", {"start": v(58.52, 73.5) * mm, "end": v(60.23, 72.75) * mm});
            skLineSegment(sketch, "E2144", {"start": v(60.23, 72.75) * mm, "end": v(61.77, 70.92) * mm});
            skLineSegment(sketch, "E2145", {"start": v(61.77, 70.92) * mm, "end": v(61.57, 68.55) * mm});
            skLineSegment(sketch, "E2146", {"start": v(61.57, 68.55) * mm, "end": v(60.1, 65.89) * mm});
            skLineSegment(sketch, "E2147", {"start": v(60.1, 65.89) * mm, "end": v(57.83, 63.16) * mm});
            skLineSegment(sketch, "E2148", {"start": v(57.83, 63.16) * mm, "end": v(55.24, 60.63) * mm});
            skLineSegment(sketch, "E2149", {"start": v(55.24, 60.63) * mm, "end": v(52.8, 58.52) * mm});
            skLineSegment(sketch, "E2150", {"start": v(52.8, 58.52) * mm, "end": v(51, 57.07) * mm});
            skLineSegment(sketch, "E2151", {"start": v(51, 57.07) * mm, "end": v(50.28, 56.54) * mm});
            skLineSegment(sketch, "E2152", {"start": v(50.28, 56.54) * mm, "end": v(49.87, 56.91) * mm});
            skLineSegment(sketch, "E2153", {"start": v(49.87, 56.91) * mm, "end": v(48.7, 57.9) * mm});
            skLineSegment(sketch, "E2154", {"start": v(48.7, 57.9) * mm, "end": v(46.89, 59.28) * mm});
            skLineSegment(sketch, "E2155", {"start": v(46.89, 59.28) * mm, "end": v(44.55, 60.87) * mm});
            skLineSegment(sketch, "E2156", {"start": v(44.55, 60.87) * mm, "end": v(41.81, 62.45) * mm});
            skLineSegment(sketch, "E2157", {"start": v(41.81, 62.45) * mm, "end": v(38.77, 63.82) * mm});
            skLineSegment(sketch, "E2158", {"start": v(38.77, 63.82) * mm, "end": v(35.56, 64.78) * mm});
            skLineSegment(sketch, "E2159", {"start": v(35.56, 64.78) * mm, "end": v(32.28, 65.13) * mm});
            skLineSegment(sketch, "E2160", {"start": v(32.28, 65.13) * mm, "end": v(28.51, 64.97) * mm});
            skLineSegment(sketch, "E2161", {"start": v(28.51, 64.97) * mm, "end": v(25.47, 64.63) * mm});
            skLineSegment(sketch, "E2162", {"start": v(25.47, 64.63) * mm, "end": v(23.08, 64.17) * mm});
            skLineSegment(sketch, "E2163", {"start": v(23.08, 64.17) * mm, "end": v(21.28, 63.66) * mm});
            skLineSegment(sketch, "E2164", {"start": v(21.28, 63.66) * mm, "end": v(20, 63.15) * mm});
            skLineSegment(sketch, "E2165", {"start": v(20, 63.15) * mm, "end": v(19.18, 62.7) * mm});
            skLineSegment(sketch, "E2166", {"start": v(19.18, 62.7) * mm, "end": v(18.73, 62.4) * mm});
            skLineSegment(sketch, "E2167", {"start": v(18.73, 62.4) * mm, "end": v(18.6, 62.28) * mm});
            skLineSegment(sketch, "E2168", {"start": v(18.6, 62.28) * mm, "end": v(18.86, 62.6) * mm});
            skLineSegment(sketch, "E2169", {"start": v(18.86, 62.6) * mm, "end": v(19.63, 63.42) * mm});
            skLineSegment(sketch, "E2170", {"start": v(19.63, 63.42) * mm, "end": v(20.94, 64.54) * mm});
            skLineSegment(sketch, "E2171", {"start": v(20.94, 64.54) * mm, "end": v(22.78, 65.75) * mm});
            skLineSegment(sketch, "E2172", {"start": v(22.78, 65.75) * mm, "end": v(25.19, 66.85) * mm});
            skLineSegment(sketch, "E2173", {"start": v(25.19, 66.85) * mm, "end": v(28.15, 67.62) * mm});
            skLineSegment(sketch, "E2174", {"start": v(28.15, 67.62) * mm, "end": v(31.7, 67.86) * mm});
            skLineSegment(sketch, "E2175", {"start": v(31.7, 67.86) * mm, "end": v(35.83, 67.36) * mm});
            skLineSegment(sketch, "E2176", {"start": v(35.83, 67.36) * mm, "end": v(38.08, 66.85) * mm});
            skLineSegment(sketch, "E2177", {"start": v(38.08, 66.85) * mm, "end": v(40.04, 66.35) * mm});
            skLineSegment(sketch, "E2178", {"start": v(40.04, 66.35) * mm, "end": v(41.78, 65.9) * mm});
            skLineSegment(sketch, "E2179", {"start": v(41.78, 65.9) * mm, "end": v(43.38, 65.52) * mm});
            skLineSegment(sketch, "E2180", {"start": v(43.38, 65.52) * mm, "end": v(44.9, 65.27) * mm});
            skLineSegment(sketch, "E2181", {"start": v(44.9, 65.27) * mm, "end": v(46.44, 65.17) * mm});
            skLineSegment(sketch, "E2182", {"start": v(46.44, 65.17) * mm, "end": v(48.04, 65.25) * mm});
            skLineSegment(sketch, "E2183", {"start": v(48.04, 65.25) * mm, "end": v(49.79, 65.56) * mm});
            skLineSegment(sketch, "E2184", {"start": v(49.79, 65.56) * mm, "end": v(51.63, 66.1) * mm});
            skLineSegment(sketch, "E2185", {"start": v(51.63, 66.1) * mm, "end": v(53.4, 66.85) * mm});
            skLineSegment(sketch, "E2186", {"start": v(53.4, 66.85) * mm, "end": v(55.04, 67.72) * mm});
            skLineSegment(sketch, "E2187", {"start": v(55.04, 67.72) * mm, "end": v(56.45, 68.63) * mm});
            skLineSegment(sketch, "E2188", {"start": v(56.45, 68.63) * mm, "end": v(57.56, 69.54) * mm});
            skLineSegment(sketch, "E2189", {"start": v(57.56, 69.54) * mm, "end": v(58.3, 70.36) * mm});
            skLineSegment(sketch, "E2190", {"start": v(58.3, 70.36) * mm, "end": v(58.58, 71.02) * mm});
            skLineSegment(sketch, "E2191", {"start": v(58.58, 71.02) * mm, "end": v(58.32, 71.46) * mm});
            skLineSegment(sketch, "E2192", {"start": v(58.32, 71.46) * mm, "end": v(57.7, 71.73) * mm});
            skLineSegment(sketch, "E2193", {"start": v(57.7, 71.73) * mm, "end": v(56.98, 71.92) * mm});
            skLineSegment(sketch, "E2194", {"start": v(56.98, 71.92) * mm, "end": v(56.1, 72.02) * mm});
            skLineSegment(sketch, "E2195", {"start": v(56.1, 72.02) * mm, "end": v(55.08, 72.04) * mm});
            skLineSegment(sketch, "E2196", {"start": v(55.08, 72.04) * mm, "end": v(53.9, 71.98) * mm});
            skLineSegment(sketch, "E2197", {"start": v(53.9, 71.98) * mm, "end": v(52.51, 71.84) * mm});
            skLineSegment(sketch, "E2198", {"start": v(52.51, 71.84) * mm, "end": v(50.93, 71.6) * mm});
            skLineSegment(sketch, "E2199", {"start": v(50.93, 71.6) * mm, "end": v(49.13, 71.3) * mm});
            skLineSegment(sketch, "E2200", {"start": v(49.13, 71.3) * mm, "end": v(47.46, 71.1) * mm});
            skLineSegment(sketch, "E2201", {"start": v(47.46, 71.1) * mm, "end": v(45.27, 71) * mm});
            skLineSegment(sketch, "E2202", {"start": v(45.27, 71) * mm, "end": v(42.78, 70.96) * mm});
            skLineSegment(sketch, "E2203", {"start": v(42.78, 70.96) * mm, "end": v(40.24, 70.97) * mm});
            skLineSegment(sketch, "E2204", {"start": v(40.24, 70.97) * mm, "end": v(37.86, 71) * mm});
            skLineSegment(sketch, "E2205", {"start": v(37.86, 71) * mm, "end": v(35.87, 71.06) * mm});
            skLineSegment(sketch, "E2206", {"start": v(35.87, 71.06) * mm, "end": v(34.51, 71.1) * mm});
            skLineSegment(sketch, "E2207", {"start": v(34.51, 71.1) * mm, "end": v(34, 71.13) * mm});
            skLineSegment(sketch, "E2208", {"start": v(15.95, 41.9) * mm, "end": v(16.7, 41.92) * mm});
            skLineSegment(sketch, "E2209", {"start": v(16.7, 41.92) * mm, "end": v(18.68, 41.85) * mm});
            skLineSegment(sketch, "E2210", {"start": v(18.68, 41.85) * mm, "end": v(21.54, 41.52) * mm});
            skLineSegment(sketch, "E2211", {"start": v(21.54, 41.52) * mm, "end": v(24.9, 40.75) * mm});
            skLineSegment(sketch, "E2212", {"start": v(24.9, 40.75) * mm, "end": v(28.36, 39.36) * mm});
            skLineSegment(sketch, "E2213", {"start": v(28.36, 39.36) * mm, "end": v(31.58, 37.18) * mm});
            skLineSegment(sketch, "E2214", {"start": v(31.58, 37.18) * mm, "end": v(34.17, 34.02) * mm});
            skLineSegment(sketch, "E2215", {"start": v(34.17, 34.02) * mm, "end": v(35.76, 29.72) * mm});
            skLineSegment(sketch, "E2216", {"start": v(35.76, 29.72) * mm, "end": v(36.07, 29) * mm});
            skLineSegment(sketch, "E2217", {"start": v(36.07, 29) * mm, "end": v(36.9, 26.94) * mm});
            skLineSegment(sketch, "E2218", {"start": v(36.9, 26.94) * mm, "end": v(38.1, 23.7) * mm});
            skLineSegment(sketch, "E2219", {"start": v(38.1, 23.7) * mm, "end": v(39.5, 19.43) * mm});
            skLineSegment(sketch, "E2220", {"start": v(39.5, 19.43) * mm, "end": v(40.93, 14.28) * mm});
            skLineSegment(sketch, "E2221", {"start": v(40.93, 14.28) * mm, "end": v(42.23, 8.42) * mm});
            skLineSegment(sketch, "E2222", {"start": v(42.23, 8.42) * mm, "end": v(43.24, 2) * mm});
            skLineSegment(sketch, "E2223", {"start": v(43.24, 2) * mm, "end": v(43.8, -4.84) * mm});
            skLineSegment(sketch, "E2224", {"start": v(43.8, -4.84) * mm, "end": v(44.16, -4.98) * mm});
            skLineSegment(sketch, "E2225", {"start": v(44.16, -4.98) * mm, "end": v(45.14, -5.38) * mm});
            skLineSegment(sketch, "E2226", {"start": v(45.14, -5.38) * mm, "end": v(46.56, -6) * mm});
            skLineSegment(sketch, "E2227", {"start": v(46.56, -6) * mm, "end": v(48.25, -6.84) * mm});
            skLineSegment(sketch, "E2228", {"start": v(48.25, -6.84) * mm, "end": v(50.05, -7.85) * mm});
            skLineSegment(sketch, "E2229", {"start": v(50.05, -7.85) * mm, "end": v(51.78, -9.02) * mm});
            skLineSegment(sketch, "E2230", {"start": v(51.78, -9.02) * mm, "end": v(53.28, -10.31) * mm});
            skLineSegment(sketch, "E2231", {"start": v(53.28, -10.31) * mm, "end": v(54.38, -11.7) * mm});
            skLineSegment(sketch, "E2232", {"start": v(54.38, -11.7) * mm, "end": v(54.2, -11) * mm});
            skLineSegment(sketch, "E2233", {"start": v(54.2, -11) * mm, "end": v(53.7, -9.1) * mm});
            skLineSegment(sketch, "E2234", {"start": v(53.7, -9.1) * mm, "end": v(52.9, -6.33) * mm});
            skLineSegment(sketch, "E2235", {"start": v(52.9, -6.33) * mm, "end": v(51.8, -3) * mm});
            skLineSegment(sketch, "E2236", {"start": v(51.8, -3) * mm, "end": v(50.45, 0.54) * mm});
            skLineSegment(sketch, "E2237", {"start": v(50.45, 0.54) * mm, "end": v(48.85, 4) * mm});
            skLineSegment(sketch, "E2238", {"start": v(48.85, 4) * mm, "end": v(47.04, 7.03) * mm});
            skLineSegment(sketch, "E2239", {"start": v(47.04, 7.03) * mm, "end": v(45.03, 9.31) * mm});
            skLineSegment(sketch, "E2240", {"start": v(45.03, 9.31) * mm, "end": v(45.74, 9.5) * mm});
            skLineSegment(sketch, "E2241", {"start": v(45.74, 9.5) * mm, "end": v(47.7, 9.86) * mm});
            skLineSegment(sketch, "E2242", {"start": v(47.7, 9.86) * mm, "end": v(50.64, 10.15) * mm});
            skLineSegment(sketch, "E2243", {"start": v(50.64, 10.15) * mm, "end": v(54.33, 10.08) * mm});
            skLineSegment(sketch, "E2244", {"start": v(54.33, 10.08) * mm, "end": v(58.5, 9.4) * mm});
            skLineSegment(sketch, "E2245", {"start": v(58.5, 9.4) * mm, "end": v(62.92, 7.85) * mm});
            skLineSegment(sketch, "E2246", {"start": v(62.92, 7.85) * mm, "end": v(67.32, 5.14) * mm});
            skLineSegment(sketch, "E2247", {"start": v(67.32, 5.14) * mm, "end": v(71.44, 1.02) * mm});
            skLineSegment(sketch, "E2248", {"start": v(71.44, 1.02) * mm, "end": v(71.2, 1.95) * mm});
            skLineSegment(sketch, "E2249", {"start": v(71.2, 1.95) * mm, "end": v(70.46, 4.45) * mm});
            skLineSegment(sketch, "E2250", {"start": v(70.46, 4.45) * mm, "end": v(69.28, 8.08) * mm});
            skLineSegment(sketch, "E2251", {"start": v(69.28, 8.08) * mm, "end": v(67.68, 12.43) * mm});
            skLineSegment(sketch, "E2252", {"start": v(67.68, 12.43) * mm, "end": v(65.68, 17.07) * mm});
            skLineSegment(sketch, "E2253", {"start": v(65.68, 17.07) * mm, "end": v(63.3, 21.56) * mm});
            skLineSegment(sketch, "E2254", {"start": v(63.3, 21.56) * mm, "end": v(60.6, 25.48) * mm});
            skLineSegment(sketch, "E2255", {"start": v(60.6, 25.48) * mm, "end": v(57.56, 28.4) * mm});
            skLineSegment(sketch, "E2256", {"start": v(57.56, 28.4) * mm, "end": v(58.07, 28.35) * mm});
            skLineSegment(sketch, "E2257", {"start": v(58.07, 28.35) * mm, "end": v(59.45, 28.18) * mm});
            skLineSegment(sketch, "E2258", {"start": v(59.45, 28.18) * mm, "end": v(61.48, 27.87) * mm});
            skLineSegment(sketch, "E2259", {"start": v(61.48, 27.87) * mm, "end": v(63.95, 27.38) * mm});
            skLineSegment(sketch, "E2260", {"start": v(63.95, 27.38) * mm, "end": v(66.62, 26.67) * mm});
            skLineSegment(sketch, "E2261", {"start": v(66.62, 26.67) * mm, "end": v(69.27, 25.73) * mm});
            skLineSegment(sketch, "E2262", {"start": v(69.27, 25.73) * mm, "end": v(71.7, 24.5) * mm});
            skLineSegment(sketch, "E2263", {"start": v(71.7, 24.5) * mm, "end": v(73.66, 22.98) * mm});
            skLineSegment(sketch, "E2264", {"start": v(73.66, 22.98) * mm, "end": v(73.35, 23.91) * mm});
            skLineSegment(sketch, "E2265", {"start": v(73.35, 23.91) * mm, "end": v(72.33, 26.49) * mm});
            skLineSegment(sketch, "E2266", {"start": v(72.33, 26.49) * mm, "end": v(70.4, 30.39) * mm});
            skLineSegment(sketch, "E2267", {"start": v(70.4, 30.39) * mm, "end": v(67.43, 35.28) * mm});
            skLineSegment(sketch, "E2268", {"start": v(67.43, 35.28) * mm, "end": v(63.23, 40.84) * mm});
            skLineSegment(sketch, "E2269", {"start": v(63.23, 40.84) * mm, "end": v(57.63, 46.73) * mm});
            skLineSegment(sketch, "E2270", {"start": v(57.63, 46.73) * mm, "end": v(50.47, 52.63) * mm});
            skLineSegment(sketch, "E2271", {"start": v(50.47, 52.63) * mm, "end": v(41.57, 58.22) * mm});
            skLineSegment(sketch, "E2272", {"start": v(41.57, 58.22) * mm, "end": v(40.86, 58.57) * mm});
            skLineSegment(sketch, "E2273", {"start": v(40.86, 58.57) * mm, "end": v(38.93, 59.43) * mm});
            skLineSegment(sketch, "E2274", {"start": v(38.93, 59.43) * mm, "end": v(36, 60.49) * mm});
            skLineSegment(sketch, "E2275", {"start": v(36, 60.49) * mm, "end": v(32.33, 61.44) * mm});
            skLineSegment(sketch, "E2276", {"start": v(32.33, 61.44) * mm, "end": v(28.16, 62) * mm});
            skLineSegment(sketch, "E2277", {"start": v(28.16, 62) * mm, "end": v(23.75, 61.85) * mm});
            skLineSegment(sketch, "E2278", {"start": v(23.75, 61.85) * mm, "end": v(19.35, 60.69) * mm});
            skLineSegment(sketch, "E2279", {"start": v(19.35, 60.69) * mm, "end": v(15.19, 58.22) * mm});
            skLineSegment(sketch, "E2280", {"start": v(15.19, 58.22) * mm, "end": v(15.8, 58.47) * mm});
            skLineSegment(sketch, "E2281", {"start": v(15.8, 58.47) * mm, "end": v(17.52, 59.07) * mm});
            skLineSegment(sketch, "E2282", {"start": v(17.52, 59.07) * mm, "end": v(20.14, 59.76) * mm});
            skLineSegment(sketch, "E2283", {"start": v(20.14, 59.76) * mm, "end": v(23.45, 60.3) * mm});
            skLineSegment(sketch, "E2284", {"start": v(23.45, 60.3) * mm, "end": v(27.25, 60.43) * mm});
            skLineSegment(sketch, "E2285", {"start": v(27.25, 60.43) * mm, "end": v(31.35, 59.91) * mm});
            skLineSegment(sketch, "E2286", {"start": v(31.35, 59.91) * mm, "end": v(35.52, 58.5) * mm});
            skLineSegment(sketch, "E2287", {"start": v(35.52, 58.5) * mm, "end": v(39.58, 55.92) * mm});
            skLineSegment(sketch, "E2288", {"start": v(39.58, 55.92) * mm, "end": v(42.88, 52.97) * mm});
            skLineSegment(sketch, "E2289", {"start": v(42.88, 52.97) * mm, "end": v(45.03, 50.53) * mm});
            skLineSegment(sketch, "E2290", {"start": v(45.03, 50.53) * mm, "end": v(46.22, 48.55) * mm});
            skLineSegment(sketch, "E2291", {"start": v(46.22, 48.55) * mm, "end": v(46.64, 47.01) * mm});
            skLineSegment(sketch, "E2292", {"start": v(46.64, 47.01) * mm, "end": v(46.48, 45.85) * mm});
            skLineSegment(sketch, "E2293", {"start": v(46.48, 45.85) * mm, "end": v(45.93, 45.04) * mm});
            skLineSegment(sketch, "E2294", {"start": v(45.93, 45.04) * mm, "end": v(45.18, 44.53) * mm});
            skLineSegment(sketch, "E2295", {"start": v(45.18, 44.53) * mm, "end": v(44.42, 44.27) * mm});
            skLineSegment(sketch, "E2296", {"start": v(44.42, 44.27) * mm, "end": v(42.66, 44.51) * mm});
            skLineSegment(sketch, "E2297", {"start": v(42.66, 44.51) * mm, "end": v(39.1, 45.32) * mm});
            skLineSegment(sketch, "E2298", {"start": v(39.1, 45.32) * mm, "end": v(34.26, 46.42) * mm});
            skLineSegment(sketch, "E2299", {"start": v(34.26, 46.42) * mm, "end": v(28.63, 47.54) * mm});
            skLineSegment(sketch, "E2300", {"start": v(28.63, 47.54) * mm, "end": v(22.73, 48.4) * mm});
            skLineSegment(sketch, "E2301", {"start": v(22.73, 48.4) * mm, "end": v(17.07, 48.7) * mm});
            skLineSegment(sketch, "E2302", {"start": v(17.07, 48.7) * mm, "end": v(12.14, 48.2) * mm});
            skLineSegment(sketch, "E2303", {"start": v(12.14, 48.2) * mm, "end": v(8.46, 46.6) * mm});
            skLineSegment(sketch, "E2304", {"start": v(8.46, 46.6) * mm, "end": v(9.05, 46.72) * mm});
            skLineSegment(sketch, "E2305", {"start": v(9.05, 46.72) * mm, "end": v(10.69, 46.98) * mm});
            skLineSegment(sketch, "E2306", {"start": v(10.69, 46.98) * mm, "end": v(13.22, 47.23) * mm});
            skLineSegment(sketch, "E2307", {"start": v(13.22, 47.23) * mm, "end": v(16.46, 47.32) * mm});
            skLineSegment(sketch, "E2308", {"start": v(16.46, 47.32) * mm, "end": v(20.24, 47.1) * mm});
            skLineSegment(sketch, "E2309", {"start": v(20.24, 47.1) * mm, "end": v(24.4, 46.43) * mm});
            skLineSegment(sketch, "E2310", {"start": v(24.4, 46.43) * mm, "end": v(28.74, 45.16) * mm});
            skLineSegment(sketch, "E2311", {"start": v(28.74, 45.16) * mm, "end": v(33.12, 43.13) * mm});
            skLineSegment(sketch, "E2312", {"start": v(33.12, 43.13) * mm, "end": v(32.77, 43.25) * mm});
            skLineSegment(sketch, "E2313", {"start": v(32.77, 43.25) * mm, "end": v(31.76, 43.52) * mm});
            skLineSegment(sketch, "E2314", {"start": v(31.76, 43.52) * mm, "end": v(30.17, 43.84) * mm});
            skLineSegment(sketch, "E2315", {"start": v(30.17, 43.84) * mm, "end": v(28.07, 44.07) * mm});
            skLineSegment(sketch, "E2316", {"start": v(28.07, 44.07) * mm, "end": v(25.52, 44.12) * mm});
            skLineSegment(sketch, "E2317", {"start": v(25.52, 44.12) * mm, "end": v(22.6, 43.85) * mm});
            skLineSegment(sketch, "E2318", {"start": v(22.6, 43.85) * mm, "end": v(19.4, 43.15) * mm});
            skLineSegment(sketch, "E2319", {"start": v(19.4, 43.15) * mm, "end": v(15.95, 41.9) * mm});
            skLineSegment(sketch, "E2320", {"start": v(57.16, 70.98) * mm, "end": v(56.96, 70.78) * mm});
            skLineSegment(sketch, "E2321", {"start": v(56.96, 70.78) * mm, "end": v(56.37, 70.28) * mm});
            skLineSegment(sketch, "E2322", {"start": v(56.37, 70.28) * mm, "end": v(55.43, 69.55) * mm});
            skLineSegment(sketch, "E2323", {"start": v(55.43, 69.55) * mm, "end": v(54.18, 68.72) * mm});
            skLineSegment(sketch, "E2324", {"start": v(54.18, 68.72) * mm, "end": v(52.63, 67.89) * mm});
            skLineSegment(sketch, "E2325", {"start": v(52.63, 67.89) * mm, "end": v(50.84, 67.14) * mm});
            skLineSegment(sketch, "E2326", {"start": v(50.84, 67.14) * mm, "end": v(48.82, 66.6) * mm});
            skLineSegment(sketch, "E2327", {"start": v(48.82, 66.6) * mm, "end": v(46.6, 66.37) * mm});
            skLineSegment(sketch, "E2328", {"start": v(46.6, 66.37) * mm, "end": v(44, 66.62) * mm});
            skLineSegment(sketch, "E2329", {"start": v(44, 66.62) * mm, "end": v(40.84, 67.28) * mm});
            skLineSegment(sketch, "E2330", {"start": v(40.84, 67.28) * mm, "end": v(37.2, 68.07) * mm});
            skLineSegment(sketch, "E2331", {"start": v(37.2, 68.07) * mm, "end": v(33.2, 68.7) * mm});
            skLineSegment(sketch, "E2332", {"start": v(33.2, 68.7) * mm, "end": v(28.9, 68.88) * mm});
            skLineSegment(sketch, "E2333", {"start": v(28.9, 68.88) * mm, "end": v(24.39, 68.31) * mm});
            skLineSegment(sketch, "E2334", {"start": v(24.39, 68.31) * mm, "end": v(19.77, 66.73) * mm});
            skLineSegment(sketch, "E2335", {"start": v(19.77, 66.73) * mm, "end": v(15.12, 63.82) * mm});
            skLineSegment(sketch, "E2336", {"start": v(15.12, 63.82) * mm, "end": v(15.18, 64.03) * mm});
            skLineSegment(sketch, "E2337", {"start": v(15.18, 64.03) * mm, "end": v(15.37, 64.59) * mm});
            skLineSegment(sketch, "E2338", {"start": v(15.37, 64.59) * mm, "end": v(15.7, 65.4) * mm});
            skLineSegment(sketch, "E2339", {"start": v(15.7, 65.4) * mm, "end": v(16.16, 66.38) * mm});
            skLineSegment(sketch, "E2340", {"start": v(16.16, 66.38) * mm, "end": v(16.77, 67.41) * mm});
            skLineSegment(sketch, "E2341", {"start": v(16.77, 67.41) * mm, "end": v(17.54, 68.42) * mm});
            skLineSegment(sketch, "E2342", {"start": v(17.54, 68.42) * mm, "end": v(18.47, 69.3) * mm});
            skLineSegment(sketch, "E2343", {"start": v(18.47, 69.3) * mm, "end": v(19.58, 69.94) * mm});
            skLineSegment(sketch, "E2344", {"start": v(19.58, 69.94) * mm, "end": v(19.1, 69.94) * mm});
            skLineSegment(sketch, "E2345", {"start": v(19.1, 69.94) * mm, "end": v(17.81, 69.92) * mm});
            skLineSegment(sketch, "E2346", {"start": v(17.81, 69.92) * mm, "end": v(15.94, 69.84) * mm});
            skLineSegment(sketch, "E2347", {"start": v(15.94, 69.84) * mm, "end": v(13.69, 69.67) * mm});
            skLineSegment(sketch, "E2348", {"start": v(13.69, 69.67) * mm, "end": v(11.28, 69.38) * mm});
            skLineSegment(sketch, "E2349", {"start": v(11.28, 69.38) * mm, "end": v(8.93, 68.93) * mm});
            skLineSegment(sketch, "E2350", {"start": v(8.93, 68.93) * mm, "end": v(6.86, 68.28) * mm});
            skLineSegment(sketch, "E2351", {"start": v(6.86, 68.28) * mm, "end": v(5.28, 67.4) * mm});
            skLineSegment(sketch, "E2352", {"start": v(5.28, 67.4) * mm, "end": v(5.15, 67.48) * mm});
            skLineSegment(sketch, "E2353", {"start": v(5.15, 67.48) * mm, "end": v(4.77, 67.7) * mm});
            skLineSegment(sketch, "E2354", {"start": v(4.77, 67.7) * mm, "end": v(4.24, 68.04) * mm});
            skLineSegment(sketch, "E2355", {"start": v(4.24, 68.04) * mm, "end": v(3.63, 68.48) * mm});
            skLineSegment(sketch, "E2356", {"start": v(3.63, 68.48) * mm, "end": v(3, 69.02) * mm});
            skLineSegment(sketch, "E2357", {"start": v(3, 69.02) * mm, "end": v(2.42, 69.62) * mm});
            skLineSegment(sketch, "E2358", {"start": v(2.42, 69.62) * mm, "end": v(1.97, 70.28) * mm});
            skLineSegment(sketch, "E2359", {"start": v(1.97, 70.28) * mm, "end": v(1.73, 70.98) * mm});
            skLineSegment(sketch, "E2360", {"start": v(1.73, 70.98) * mm, "end": v(2.53, 71.59) * mm});
            skLineSegment(sketch, "E2361", {"start": v(2.53, 71.59) * mm, "end": v(4.97, 72) * mm});
            skLineSegment(sketch, "E2362", {"start": v(4.97, 72) * mm, "end": v(8.67, 72.18) * mm});
            skLineSegment(sketch, "E2363", {"start": v(8.67, 72.18) * mm, "end": v(13.3, 72.14) * mm});
            skLineSegment(sketch, "E2364", {"start": v(13.3, 72.14) * mm, "end": v(18.5, 71.86) * mm});
            skLineSegment(sketch, "E2365", {"start": v(18.5, 71.86) * mm, "end": v(23.91, 71.32) * mm});
            skLineSegment(sketch, "E2366", {"start": v(23.91, 71.32) * mm, "end": v(29.2, 70.51) * mm});
            skLineSegment(sketch, "E2367", {"start": v(29.2, 70.51) * mm, "end": v(34, 69.43) * mm});
            skLineSegment(sketch, "E2368", {"start": v(34, 69.43) * mm, "end": v(36.42, 68.91) * mm});
            skLineSegment(sketch, "E2369", {"start": v(36.42, 68.91) * mm, "end": v(39.44, 68.51) * mm});
            skLineSegment(sketch, "E2370", {"start": v(39.44, 68.51) * mm, "end": v(42.84, 68.27) * mm});
            skLineSegment(sketch, "E2371", {"start": v(42.84, 68.27) * mm, "end": v(46.38, 68.23) * mm});
            skLineSegment(sketch, "E2372", {"start": v(46.38, 68.23) * mm, "end": v(49.82, 68.43) * mm});
            skLineSegment(sketch, "E2373", {"start": v(49.82, 68.43) * mm, "end": v(52.92, 68.93) * mm});
            skLineSegment(sketch, "E2374", {"start": v(52.92, 68.93) * mm, "end": v(55.45, 69.77) * mm});
            skLineSegment(sketch, "E2375", {"start": v(55.45, 69.77) * mm, "end": v(57.16, 70.98) * mm});
            skLineSegment(sketch, "E2376", {"start": v(-16.23, 37.17) * mm, "end": v(-17.68, 37.42) * mm});
            skLineSegment(sketch, "E2377", {"start": v(-17.68, 37.42) * mm, "end": v(-21.6, 38.1) * mm});
            skLineSegment(sketch, "E2378", {"start": v(-21.6, 38.1) * mm, "end": v(-27.3, 39.05) * mm});
            skLineSegment(sketch, "E2379", {"start": v(-27.3, 39.05) * mm, "end": v(-34.17, 40.14) * mm});
            skLineSegment(sketch, "E2380", {"start": v(-34.17, 40.14) * mm, "end": v(-41.52, 41.23) * mm});
            skLineSegment(sketch, "E2381", {"start": v(-41.52, 41.23) * mm, "end": v(-48.7, 42.18) * mm});
            skLineSegment(sketch, "E2382", {"start": v(-48.7, 42.18) * mm, "end": v(-55.07, 42.85) * mm});
            skLineSegment(sketch, "E2383", {"start": v(-55.07, 42.85) * mm, "end": v(-59.95, 43.1) * mm});
            skLineSegment(sketch, "E2384", {"start": v(-59.95, 43.1) * mm, "end": v(-58.32, 42.85) * mm});
            skLineSegment(sketch, "E2385", {"start": v(-58.32, 42.85) * mm, "end": v(-53.97, 42.2) * mm});
            skLineSegment(sketch, "E2386", {"start": v(-53.97, 42.2) * mm, "end": v(-47.72, 41.27) * mm});
            skLineSegment(sketch, "E2387", {"start": v(-47.72, 41.27) * mm, "end": v(-40.37, 40.2) * mm});
            skLineSegment(sketch, "E2388", {"start": v(-40.37, 40.2) * mm, "end": v(-32.74, 39.14) * mm});
            skLineSegment(sketch, "E2389", {"start": v(-32.74, 39.14) * mm, "end": v(-25.63, 38.18) * mm});
            skLineSegment(sketch, "E2390", {"start": v(-25.63, 38.18) * mm, "end": v(-19.86, 37.48) * mm});
            skLineSegment(sketch, "E2391", {"start": v(-19.86, 37.48) * mm, "end": v(-16.23, 37.17) * mm});
            skLineSegment(sketch, "E2392", {"start": v(-18.02, 35.71) * mm, "end": v(-19.52, 35.74) * mm});
            skLineSegment(sketch, "E2393", {"start": v(-19.52, 35.74) * mm, "end": v(-23.56, 35.83) * mm});
            skLineSegment(sketch, "E2394", {"start": v(-23.56, 35.83) * mm, "end": v(-29.46, 36) * mm});
            skLineSegment(sketch, "E2395", {"start": v(-29.46, 36) * mm, "end": v(-36.52, 36.24) * mm});
            skLineSegment(sketch, "E2396", {"start": v(-36.52, 36.24) * mm, "end": v(-44.07, 36.6) * mm});
            skLineSegment(sketch, "E2397", {"start": v(-44.07, 36.6) * mm, "end": v(-51.4, 37.06) * mm});
            skLineSegment(sketch, "E2398", {"start": v(-51.4, 37.06) * mm, "end": v(-57.85, 37.65) * mm});
            skLineSegment(sketch, "E2399", {"start": v(-57.85, 37.65) * mm, "end": v(-62.7, 38.37) * mm});
            skLineSegment(sketch, "E2400", {"start": v(-62.7, 38.37) * mm, "end": v(-61.03, 38.3) * mm});
            skLineSegment(sketch, "E2401", {"start": v(-61.03, 38.3) * mm, "end": v(-56.57, 38.1) * mm});
            skLineSegment(sketch, "E2402", {"start": v(-56.57, 38.1) * mm, "end": v(-50.15, 37.8) * mm});
            skLineSegment(sketch, "E2403", {"start": v(-50.15, 37.8) * mm, "end": v(-42.61, 37.43) * mm});
            skLineSegment(sketch, "E2404", {"start": v(-42.61, 37.43) * mm, "end": v(-34.8, 37) * mm});
            skLineSegment(sketch, "E2405", {"start": v(-34.8, 37) * mm, "end": v(-27.53, 36.56) * mm});
            skLineSegment(sketch, "E2406", {"start": v(-27.53, 36.56) * mm, "end": v(-21.66, 36.12) * mm});
            skLineSegment(sketch, "E2407", {"start": v(-21.66, 36.12) * mm, "end": v(-18.02, 35.71) * mm});
            skLineSegment(sketch, "E2408", {"start": v(-20.6, 33.87) * mm, "end": v(-22.16, 33.77) * mm});
            skLineSegment(sketch, "E2409", {"start": v(-22.16, 33.77) * mm, "end": v(-26.36, 33.53) * mm});
            skLineSegment(sketch, "E2410", {"start": v(-26.36, 33.53) * mm, "end": v(-32.48, 33.2) * mm});
            skLineSegment(sketch, "E2411", {"start": v(-32.48, 33.2) * mm, "end": v(-39.8, 32.86) * mm});
            skLineSegment(sketch, "E2412", {"start": v(-39.8, 32.86) * mm, "end": v(-47.62, 32.59) * mm});
            skLineSegment(sketch, "E2413", {"start": v(-47.62, 32.59) * mm, "end": v(-55.2, 32.44) * mm});
            skLineSegment(sketch, "E2414", {"start": v(-55.2, 32.44) * mm, "end": v(-61.84, 32.5) * mm});
            skLineSegment(sketch, "E2415", {"start": v(-61.84, 32.5) * mm, "end": v(-66.8, 32.82) * mm});
            skLineSegment(sketch, "E2416", {"start": v(-66.8, 32.82) * mm, "end": v(-65.07, 32.88) * mm});
            skLineSegment(sketch, "E2417", {"start": v(-65.07, 32.88) * mm, "end": v(-60.44, 33.05) * mm});
            skLineSegment(sketch, "E2418", {"start": v(-60.44, 33.05) * mm, "end": v(-53.78, 33.29) * mm});
            skLineSegment(sketch, "E2419", {"start": v(-53.78, 33.29) * mm, "end": v(-45.97, 33.54) * mm});
            skLineSegment(sketch, "E2420", {"start": v(-45.97, 33.54) * mm, "end": v(-37.88, 33.77) * mm});
            skLineSegment(sketch, "E2421", {"start": v(-37.88, 33.77) * mm, "end": v(-30.38, 33.93) * mm});
            skLineSegment(sketch, "E2422", {"start": v(-30.38, 33.93) * mm, "end": v(-24.33, 33.98) * mm});
            skLineSegment(sketch, "E2423", {"start": v(-24.33, 33.98) * mm, "end": v(-20.6, 33.87) * mm});
            skLineSegment(sketch, "E2424", {"start": v(16.13, 37.16) * mm, "end": v(17.58, 37.41) * mm});
            skLineSegment(sketch, "E2425", {"start": v(17.58, 37.41) * mm, "end": v(21.5, 38.09) * mm});
            skLineSegment(sketch, "E2426", {"start": v(21.5, 38.09) * mm, "end": v(27.21, 39.04) * mm});
            skLineSegment(sketch, "E2427", {"start": v(27.21, 39.04) * mm, "end": v(34.07, 40.13) * mm});
            skLineSegment(sketch, "E2428", {"start": v(34.07, 40.13) * mm, "end": v(41.42, 41.22) * mm});
            skLineSegment(sketch, "E2429", {"start": v(41.42, 41.22) * mm, "end": v(48.6, 42.17) * mm});
            skLineSegment(sketch, "E2430", {"start": v(48.6, 42.17) * mm, "end": v(54.97, 42.83) * mm});
            skLineSegment(sketch, "E2431", {"start": v(54.97, 42.83) * mm, "end": v(59.85, 43.08) * mm});
            skLineSegment(sketch, "E2432", {"start": v(59.85, 43.08) * mm, "end": v(58.22, 42.84) * mm});
            skLineSegment(sketch, "E2433", {"start": v(58.22, 42.84) * mm, "end": v(53.87, 42.19) * mm});
            skLineSegment(sketch, "E2434", {"start": v(53.87, 42.19) * mm, "end": v(47.62, 41.26) * mm});
            skLineSegment(sketch, "E2435", {"start": v(47.62, 41.26) * mm, "end": v(40.27, 40.2) * mm});
            skLineSegment(sketch, "E2436", {"start": v(40.27, 40.2) * mm, "end": v(32.64, 39.12) * mm});
            skLineSegment(sketch, "E2437", {"start": v(32.64, 39.12) * mm, "end": v(25.53, 38.17) * mm});
            skLineSegment(sketch, "E2438", {"start": v(25.53, 38.17) * mm, "end": v(19.76, 37.47) * mm});
            skLineSegment(sketch, "E2439", {"start": v(19.76, 37.47) * mm, "end": v(16.13, 37.16) * mm});
            skLineSegment(sketch, "E2440", {"start": v(17.92, 35.7) * mm, "end": v(19.42, 35.73) * mm});
            skLineSegment(sketch, "E2441", {"start": v(19.42, 35.73) * mm, "end": v(23.46, 35.82) * mm});
            skLineSegment(sketch, "E2442", {"start": v(23.46, 35.82) * mm, "end": v(29.36, 35.98) * mm});
            skLineSegment(sketch, "E2443", {"start": v(29.36, 35.98) * mm, "end": v(36.42, 36.23) * mm});
            skLineSegment(sketch, "E2444", {"start": v(36.42, 36.23) * mm, "end": v(43.97, 36.59) * mm});
            skLineSegment(sketch, "E2445", {"start": v(43.97, 36.59) * mm, "end": v(51.3, 37.05) * mm});
            skLineSegment(sketch, "E2446", {"start": v(51.3, 37.05) * mm, "end": v(57.75, 37.64) * mm});
            skLineSegment(sketch, "E2447", {"start": v(57.75, 37.64) * mm, "end": v(62.6, 38.36) * mm});
            skLineSegment(sketch, "E2448", {"start": v(62.6, 38.36) * mm, "end": v(60.94, 38.3) * mm});
            skLineSegment(sketch, "E2449", {"start": v(60.94, 38.3) * mm, "end": v(56.47, 38.1) * mm});
            skLineSegment(sketch, "E2450", {"start": v(56.47, 38.1) * mm, "end": v(50.05, 37.8) * mm});
            skLineSegment(sketch, "E2451", {"start": v(50.05, 37.8) * mm, "end": v(42.52, 37.42) * mm});
            skLineSegment(sketch, "E2452", {"start": v(42.52, 37.42) * mm, "end": v(34.7, 37) * mm});
            skLineSegment(sketch, "E2453", {"start": v(34.7, 37) * mm, "end": v(27.43, 36.55) * mm});
            skLineSegment(sketch, "E2454", {"start": v(27.43, 36.55) * mm, "end": v(21.56, 36.1) * mm});
            skLineSegment(sketch, "E2455", {"start": v(21.56, 36.1) * mm, "end": v(17.92, 35.7) * mm});
            skLineSegment(sketch, "E2456", {"start": v(20.5, 33.86) * mm, "end": v(22.06, 33.76) * mm});
            skLineSegment(sketch, "E2457", {"start": v(22.06, 33.76) * mm, "end": v(26.26, 33.52) * mm});
            skLineSegment(sketch, "E2458", {"start": v(26.26, 33.52) * mm, "end": v(32.38, 33.19) * mm});
            skLineSegment(sketch, "E2459", {"start": v(32.38, 33.19) * mm, "end": v(39.71, 32.85) * mm});
            skLineSegment(sketch, "E2460", {"start": v(39.71, 32.85) * mm, "end": v(47.53, 32.57) * mm});
            skLineSegment(sketch, "E2461", {"start": v(47.53, 32.57) * mm, "end": v(55.1, 32.43) * mm});
            skLineSegment(sketch, "E2462", {"start": v(55.1, 32.43) * mm, "end": v(61.74, 32.48) * mm});
            skLineSegment(sketch, "E2463", {"start": v(61.74, 32.48) * mm, "end": v(66.7, 32.8) * mm});
            skLineSegment(sketch, "E2464", {"start": v(66.7, 32.8) * mm, "end": v(64.97, 32.87) * mm});
            skLineSegment(sketch, "E2465", {"start": v(64.97, 32.87) * mm, "end": v(60.34, 33.04) * mm});
            skLineSegment(sketch, "E2466", {"start": v(60.34, 33.04) * mm, "end": v(53.68, 33.28) * mm});
            skLineSegment(sketch, "E2467", {"start": v(53.68, 33.28) * mm, "end": v(45.88, 33.53) * mm});
            skLineSegment(sketch, "E2468", {"start": v(45.88, 33.53) * mm, "end": v(37.79, 33.76) * mm});
            skLineSegment(sketch, "E2469", {"start": v(37.79, 33.76) * mm, "end": v(30.28, 33.92) * mm});
            skLineSegment(sketch, "E2470", {"start": v(30.28, 33.92) * mm, "end": v(24.23, 33.97) * mm});
            skLineSegment(sketch, "E2471", {"start": v(24.23, 33.97) * mm, "end": v(20.5, 33.86) * mm});
            skLineSegment(sketch, "E2472", {"start": v(-17.2, 17.72) * mm, "end": v(-17.14, 17.7) * mm});
            skLineSegment(sketch, "E2473", {"start": v(-17.14, 17.7) * mm, "end": v(-16.95, 17.64) * mm});
            skLineSegment(sketch, "E2474", {"start": v(-16.95, 17.64) * mm, "end": v(-16.68, 17.53) * mm});
            skLineSegment(sketch, "E2475", {"start": v(-16.68, 17.53) * mm, "end": v(-16.34, 17.37) * mm});
            skLineSegment(sketch, "E2476", {"start": v(-16.34, 17.37) * mm, "end": v(-15.98, 17.17) * mm});
            skLineSegment(sketch, "E2477", {"start": v(-15.98, 17.17) * mm, "end": v(-15.62, 16.92) * mm});
            skLineSegment(sketch, "E2478", {"start": v(-15.62, 16.92) * mm, "end": v(-15.29, 16.63) * mm});
            skLineSegment(sketch, "E2479", {"start": v(-15.29, 16.63) * mm, "end": v(-15.02, 16.28) * mm});
            skLineSegment(sketch, "E2480", {"start": v(-15.02, 16.28) * mm, "end": v(-15.13, 15.16) * mm});
            skLineSegment(sketch, "E2481", {"start": v(-15.13, 15.16) * mm, "end": v(-15.42, 11.73) * mm});
            skLineSegment(sketch, "E2482", {"start": v(-15.42, 11.73) * mm, "end": v(-15.78, 5.9) * mm});
            skLineSegment(sketch, "E2483", {"start": v(-15.78, 5.9) * mm, "end": v(-16.13, -2.45) * mm});
            skLineSegment(sketch, "E2484", {"start": v(-16.13, -2.45) * mm, "end": v(-16.37, -13.42) * mm});
            skLineSegment(sketch, "E2485", {"start": v(-16.37, -13.42) * mm, "end": v(-16.42, -27.1) * mm});
            skLineSegment(sketch, "E2486", {"start": v(-16.42, -27.1) * mm, "end": v(-16.19, -43.58) * mm});
            skLineSegment(sketch, "E2487", {"start": v(-16.19, -43.58) * mm, "end": v(-15.57, -63) * mm});
            skLineSegment(sketch, "E2488", {"start": v(-15.57, -63) * mm, "end": v(-15.73, -62.04) * mm});
            skLineSegment(sketch, "E2489", {"start": v(-15.73, -62.04) * mm, "end": v(-16.12, -58.99) * mm});
            skLineSegment(sketch, "E2490", {"start": v(-16.12, -58.99) * mm, "end": v(-16.64, -53.58) * mm});
            skLineSegment(sketch, "E2491", {"start": v(-16.64, -53.58) * mm, "end": v(-17.18, -45.57) * mm});
            skLineSegment(sketch, "E2492", {"start": v(-17.18, -45.57) * mm, "end": v(-17.61, -34.7) * mm});
            skLineSegment(sketch, "E2493", {"start": v(-17.61, -34.7) * mm, "end": v(-17.84, -20.7) * mm});
            skLineSegment(sketch, "E2494", {"start": v(-17.84, -20.7) * mm, "end": v(-17.74, -3.3) * mm});
            skLineSegment(sketch, "E2495", {"start": v(-17.74, -3.3) * mm, "end": v(-17.2, 17.72) * mm});
            skLineSegment(sketch, "E2496", {"start": v(24.24, 17.94) * mm, "end": v(24.43, 15.33) * mm});
            skLineSegment(sketch, "E2497", {"start": v(24.43, 15.33) * mm, "end": v(24.8, 8.2) * mm});
            skLineSegment(sketch, "E2498", {"start": v(24.8, 8.2) * mm, "end": v(25.05, -2.39) * mm});
            skLineSegment(sketch, "E2499", {"start": v(25.05, -2.39) * mm, "end": v(24.9, -15.4) * mm});
            skLineSegment(sketch, "E2500", {"start": v(24.9, -15.4) * mm, "end": v(24.03, -29.77) * mm});
            skLineSegment(sketch, "E2501", {"start": v(24.03, -29.77) * mm, "end": v(22.17, -44.45) * mm});
            skLineSegment(sketch, "E2502", {"start": v(22.17, -44.45) * mm, "end": v(19.02, -58.4) * mm});
            skLineSegment(sketch, "E2503", {"start": v(19.02, -58.4) * mm, "end": v(14.27, -70.55) * mm});
            skLineSegment(sketch, "E2504", {"start": v(14.27, -70.55) * mm, "end": v(14.37, -67.96) * mm});
            skLineSegment(sketch, "E2505", {"start": v(14.37, -67.96) * mm, "end": v(14.61, -60.91) * mm});
            skLineSegment(sketch, "E2506", {"start": v(14.61, -60.91) * mm, "end": v(14.89, -50.45) * mm});
            skLineSegment(sketch, "E2507", {"start": v(14.89, -50.45) * mm, "end": v(15.1, -37.6) * mm});
            skLineSegment(sketch, "E2508", {"start": v(15.1, -37.6) * mm, "end": v(15.15, -23.45) * mm});
            skLineSegment(sketch, "E2509", {"start": v(15.15, -23.45) * mm, "end": v(14.95, -9) * mm});
            skLineSegment(sketch, "E2510", {"start": v(14.95, -9) * mm, "end": v(14.38, 4.65) * mm});
            skLineSegment(sketch, "E2511", {"start": v(14.38, 4.65) * mm, "end": v(13.36, 16.5) * mm});
            skLineSegment(sketch, "E2512", {"start": v(13.36, 16.5) * mm, "end": v(13.4, 16.6) * mm});
            skLineSegment(sketch, "E2513", {"start": v(13.4, 16.6) * mm, "end": v(13.54, 16.85) * mm});
            skLineSegment(sketch, "E2514", {"start": v(13.54, 16.85) * mm, "end": v(13.82, 17.22) * mm});
            skLineSegment(sketch, "E2515", {"start": v(13.82, 17.22) * mm, "end": v(14.27, 17.67) * mm});
            skLineSegment(sketch, "E2516", {"start": v(14.27, 17.67) * mm, "end": v(14.93, 18.14) * mm});
            skLineSegment(sketch, "E2517", {"start": v(14.93, 18.14) * mm, "end": v(15.82, 18.6) * mm});
            skLineSegment(sketch, "E2518", {"start": v(15.82, 18.6) * mm, "end": v(17, 19) * mm});
            skLineSegment(sketch, "E2519", {"start": v(17, 19) * mm, "end": v(18.48, 19.3) * mm});
            skLineSegment(sketch, "E2520", {"start": v(18.48, 19.3) * mm, "end": v(20, 19.43) * mm});
            skLineSegment(sketch, "E2521", {"start": v(20, 19.43) * mm, "end": v(21.23, 19.39) * mm});
            skLineSegment(sketch, "E2522", {"start": v(21.23, 19.39) * mm, "end": v(22.23, 19.21) * mm});
            skLineSegment(sketch, "E2523", {"start": v(22.23, 19.21) * mm, "end": v(23, 18.95) * mm});
            skLineSegment(sketch, "E2524", {"start": v(23, 18.95) * mm, "end": v(23.57, 18.65) * mm});
            skLineSegment(sketch, "E2525", {"start": v(23.57, 18.65) * mm, "end": v(23.95, 18.35) * mm});
            skLineSegment(sketch, "E2526", {"start": v(23.95, 18.35) * mm, "end": v(24.17, 18.1) * mm});
            skLineSegment(sketch, "E2527", {"start": v(24.17, 18.1) * mm, "end": v(24.24, 17.94) * mm});
            skLineSegment(sketch, "E2528", {"start": v(17.11, 17.72) * mm, "end": v(17.04, 17.7) * mm});
            skLineSegment(sketch, "E2529", {"start": v(17.04, 17.7) * mm, "end": v(16.86, 17.64) * mm});
            skLineSegment(sketch, "E2530", {"start": v(16.86, 17.64) * mm, "end": v(16.58, 17.53) * mm});
            skLineSegment(sketch, "E2531", {"start": v(16.58, 17.53) * mm, "end": v(16.25, 17.37) * mm});
            skLineSegment(sketch, "E2532", {"start": v(16.25, 17.37) * mm, "end": v(15.88, 17.17) * mm});
            skLineSegment(sketch, "E2533", {"start": v(15.88, 17.17) * mm, "end": v(15.52, 16.92) * mm});
            skLineSegment(sketch, "E2534", {"start": v(15.52, 16.92) * mm, "end": v(15.2, 16.63) * mm});
            skLineSegment(sketch, "E2535", {"start": v(15.2, 16.63) * mm, "end": v(14.92, 16.28) * mm});
            skLineSegment(sketch, "E2536", {"start": v(14.92, 16.28) * mm, "end": v(15.04, 15.16) * mm});
            skLineSegment(sketch, "E2537", {"start": v(15.04, 15.16) * mm, "end": v(15.32, 11.73) * mm});
            skLineSegment(sketch, "E2538", {"start": v(15.32, 11.73) * mm, "end": v(15.68, 5.9) * mm});
            skLineSegment(sketch, "E2539", {"start": v(15.68, 5.9) * mm, "end": v(16.03, -2.45) * mm});
            skLineSegment(sketch, "E2540", {"start": v(16.03, -2.45) * mm, "end": v(16.28, -13.42) * mm});
            skLineSegment(sketch, "E2541", {"start": v(16.28, -13.42) * mm, "end": v(16.33, -27.1) * mm});
            skLineSegment(sketch, "E2542", {"start": v(16.33, -27.1) * mm, "end": v(16.09, -43.58) * mm});
            skLineSegment(sketch, "E2543", {"start": v(16.09, -43.58) * mm, "end": v(15.48, -63) * mm});
            skLineSegment(sketch, "E2544", {"start": v(15.48, -63) * mm, "end": v(15.63, -62.04) * mm});
            skLineSegment(sketch, "E2545", {"start": v(15.63, -62.04) * mm, "end": v(16.03, -58.99) * mm});
            skLineSegment(sketch, "E2546", {"start": v(16.03, -58.99) * mm, "end": v(16.55, -53.58) * mm});
            skLineSegment(sketch, "E2547", {"start": v(16.55, -53.58) * mm, "end": v(17.08, -45.57) * mm});
            skLineSegment(sketch, "E2548", {"start": v(17.08, -45.57) * mm, "end": v(17.52, -34.7) * mm});
            skLineSegment(sketch, "E2549", {"start": v(17.52, -34.7) * mm, "end": v(17.74, -20.7) * mm});
            skLineSegment(sketch, "E2550", {"start": v(17.74, -20.7) * mm, "end": v(17.64, -3.3) * mm});
            skLineSegment(sketch, "E2551", {"start": v(17.64, -3.3) * mm, "end": v(17.11, 17.72) * mm});
            skFitSpline(sketch, "E2552", {"points": [v(-14.38, -37.28) * mm, v(0, -45.56) * mm, v(13.8, -37.88) * mm], "startDerivative": vector(0.67, -41.26) * mm, "endDerivative": vector(0.63, 38.75) * mm});
            skLineSegment(sketch, "E2553", {"start": v(0, 0) * mm, "end": v(0, -35.5) * mm, "construction": true});
            skArc(sketch, "E2554", {"start": v(0, 0) * mm, "mid": v(-2.18, 7.22) * mm, "end": v(-8, 12.02) * mm});
            skArc(sketch, "E2555", {"start": v(-8, 12.02) * mm, "mid": v(-9.64, 11.8) * mm, "end": v(-10.26, 10.28) * mm});
            skArc(sketch, "E2556", {"start": v(-12.4, -20.2) * mm, "mid": v(-9.72, -5.07) * mm, "end": v(-10.26, 10.28) * mm});
            skArc(sketch, "E2557", {"start": v(-12.4, -20.2) * mm, "mid": v(-12.24, -23.22) * mm, "end": v(-10.26, -25.51) * mm});
            skArc(sketch, "E2558", {"start": v(-4.42, -33.77) * mm, "mid": v(-6.44, -29) * mm, "end": v(-10.26, -25.51) * mm});
            skArc(sketch, "E2559", {"start": v(-4.42, -33.77) * mm, "mid": v(-4.06, -34.65) * mm, "end": v(-3.37, -35.3) * mm});
            skArc(sketch, "E2560", {"start": v(-3.37, -35.3) * mm, "mid": v(-1.71, -35.83) * mm, "end": v(0, -35.5) * mm});
            skArc(sketch, "E2561.MirrorCS", {"start": v(0, 0) * mm, "mid": v(2.18, 7.22) * mm, "end": v(8, 12.02) * mm});
            skArc(sketch, "E2562.MirrorCS", {"start": v(8, 12.02) * mm, "mid": v(9.64, 11.8) * mm, "end": v(10.26, 10.28) * mm});
            skArc(sketch, "E2563.MirrorCS", {"start": v(12.4, -20.2) * mm, "mid": v(9.72, -5.07) * mm, "end": v(10.26, 10.28) * mm});
            skArc(sketch, "E2564.MirrorCS", {"start": v(12.4, -20.2) * mm, "mid": v(12.24, -23.22) * mm, "end": v(10.26, -25.51) * mm});
            skArc(sketch, "E2565.MirrorCS", {"start": v(4.42, -33.77) * mm, "mid": v(6.44, -29) * mm, "end": v(10.26, -25.51) * mm});
            skArc(sketch, "E2566.MirrorCS", {"start": v(4.42, -33.77) * mm, "mid": v(4.06, -34.65) * mm, "end": v(3.37, -35.3) * mm});
            skArc(sketch, "E2567.MirrorCS", {"start": v(3.37, -35.3) * mm, "mid": v(1.71, -35.83) * mm, "end": v(0, -35.5) * mm});
            skLineSegment(sketch, "E2568", {"start": v(0, 27.26) * mm, "end": v(-1.66, 23.38) * mm});
            skArc(sketch, "E2569", {"start": v(-2.74, 22.6) * mm, "mid": v(-2.1, 22.84) * mm, "end": v(-1.66, 23.38) * mm});
            skArc(sketch, "E2570", {"start": v(-9.9, 23.6) * mm, "mid": v(-6.36, 22.87) * mm, "end": v(-2.74, 22.6) * mm});
            skArc(sketch, "E2571", {"start": v(-9.9, 23.6) * mm, "mid": v(-11.42, 23.77) * mm, "end": v(-12.93, 23.6) * mm});
            skArc(sketch, "E2572", {"start": v(-12.93, 23.6) * mm, "mid": v(-13.6, 23.25) * mm, "end": v(-14.03, 22.6) * mm});
            skArc(sketch, "E2573", {"start": v(-14.03, 22.6) * mm, "mid": v(-14.1, 21.22) * mm, "end": v(-13.8, 19.87) * mm});
            skArc(sketch, "E2574", {"start": v(-13.8, 19.87) * mm, "mid": v(-19.32, 21.35) * mm, "end": v(-24.95, 20.27) * mm});
            skArc(sketch, "E2575", {"start": v(-24.95, 20.27) * mm, "mid": v(-25.1, 20.1) * mm, "end": v(-25.23, 19.9) * mm});
            skArc(sketch, "E2576", {"start": v(-25.23, 19.9) * mm, "mid": v(-30.13, 4.96) * mm, "end": v(-27.81, -10.6) * mm});
            skArc(sketch, "E2577", {"start": v(-27.81, -10.6) * mm, "mid": v(-26.9, -11.82) * mm, "end": v(-25.51, -12.44) * mm});
            skLineSegment(sketch, "E2578", {"start": v(0, 27.26) * mm, "end": v(-0.19, 17.92) * mm});
            skLineSegment(sketch, "E2579.MirrorCS", {"start": v(0, 27.26) * mm, "end": v(1.66, 23.38) * mm});
            skArc(sketch, "E2580.MirrorCS", {"start": v(2.74, 22.6) * mm, "mid": v(2.1, 22.84) * mm, "end": v(1.66, 23.38) * mm});
            skArc(sketch, "E2581.MirrorCS", {"start": v(9.9, 23.6) * mm, "mid": v(6.36, 22.87) * mm, "end": v(2.74, 22.6) * mm});
            skArc(sketch, "E2582.MirrorCS", {"start": v(9.9, 23.6) * mm, "mid": v(11.42, 23.77) * mm, "end": v(12.93, 23.6) * mm});
            skArc(sketch, "E2583.MirrorCS", {"start": v(12.93, 23.6) * mm, "mid": v(13.6, 23.25) * mm, "end": v(14.03, 22.6) * mm});
            skArc(sketch, "E2584.MirrorCS", {"start": v(14.03, 22.6) * mm, "mid": v(14.1, 21.22) * mm, "end": v(13.8, 19.87) * mm});
            skArc(sketch, "E2585.MirrorCS", {"start": v(13.8, 19.87) * mm, "mid": v(19.32, 21.35) * mm, "end": v(24.95, 20.27) * mm});
            skArc(sketch, "E2586.MirrorCS", {"start": v(24.95, 20.27) * mm, "mid": v(25.1, 20.1) * mm, "end": v(25.23, 19.9) * mm});
            skArc(sketch, "E2587.MirrorCS", {"start": v(25.23, 19.9) * mm, "mid": v(30.13, 4.96) * mm, "end": v(27.81, -10.6) * mm});
            skArc(sketch, "E2588.MirrorCS", {"start": v(27.81, -10.6) * mm, "mid": v(26.9, -11.82) * mm, "end": v(25.51, -12.44) * mm});
            skSolve(sketch);
        }
        {
            var Q0;
            Q0=makeQuery(id+"F0.imprint","IMPRINT",FACE,{"disambiguationData":[TD([[makeQuery(id+"F0.imprint","IMPRINT",EDGE,{"derivedFrom":sQuery(id+"F0.wireOp",EDGE,"E2016")}),-1.0]])]});
            var Q1;
            Q1=makeQuery(id+"F0.imprint","IMPRINT",FACE,{"disambiguationData":[TD([[makeQuery(id+"F0.imprint","IMPRINT",EDGE,{"derivedFrom":sQuery(id+"F0.wireOp",EDGE,"E1464")}),1.0]])]});
            var Q2;
            Q2=makeQuery(id+"F0.imprint","IMPRINT",FACE,{"disambiguationData":[TD([[makeQuery(id+"F0.imprint","IMPRINT",EDGE,{"derivedFrom":sQuery(id+"F0.wireOp",EDGE,"E1688")}),-1.0]])]});
            var Q3;
            {var subQ8=sQuery(id+"F0.wireOp",EDGE,"E387");Q3=makeQuery(id+"F0.imprint","IMPRINT",FACE,{"disambiguationData":[TD([[makeQuery(id+"F0.imprint","IMPRINT",EDGE,{"derivedFrom":subQ8}),-1.0]])]});}
            var Q4;
            {var subQ73=sQuery(id+"F0.wireOp",EDGE,"E13");Q4=makeQuery(id+"F0.imprint","IMPRINT",FACE,{"disambiguationData":[TD([[makeQuery(id+"F0.imprint","IMPRINT",EDGE,{"derivedFrom":subQ73}),1.0]])]});}
            var Q5;
            {var subQ0=sQuery(id+"F0.wireOp",EDGE,"E509");Q5=makeQuery(id+"F0.imprint","IMPRINT",FACE,{"disambiguationData":[TD([[makeQuery(id+"F0.imprint","IMPRINT",EDGE,{"derivedFrom":subQ0}),-1.0]])]});}
            var Q6;
            {var subQ0=sQuery(id+"F0.wireOp",EDGE,"E2544");Q6=makeQuery(id+"F0.imprint","IMPRINT",FACE,{"disambiguationData":[TD([[makeQuery(id+"F0.imprint","IMPRINT",EDGE,{"derivedFrom":subQ0}),1.0]])]});}
            var Q7;
            {var subQ1=sQuery(id+"F0.wireOp",EDGE,"E509");Q7=makeQuery(id+"F0.imprint","IMPRINT",FACE,{"disambiguationData":[TD([[makeQuery(id+"F0.imprint","IMPRINT",EDGE,{"derivedFrom":subQ1}),1.0]])]});}
            var Q8;
            {var subQ5=sQuery(id+"F0.wireOp",EDGE,"E546");Q8=makeQuery(id+"F0.imprint","IMPRINT",FACE,{"disambiguationData":[TD([[makeQuery(id+"F0.imprint","IMPRINT",EDGE,{"derivedFrom":subQ5}),-1.0]])]});}
            var Q9;
            {var subQ8=sQuery(id+"F0.wireOp",EDGE,"E260");Q9=makeQuery(id+"F0.imprint","IMPRINT",FACE,{"disambiguationData":[TD([[makeQuery(id+"F0.imprint","IMPRINT",EDGE,{"derivedFrom":subQ8}),1.0]])]});}
            var Q10;
            {var subQ1=sQuery(id+"F0.wireOp",EDGE,"E257");Q10=makeQuery(id+"F0.imprint","IMPRINT",FACE,{"disambiguationData":[TD([[makeQuery(id+"F0.imprint","IMPRINT",EDGE,{"derivedFrom":subQ1}),1.0]])]});}
            var Q11;
            Q11=makeQuery(id+"F0.imprint","IMPRINT",FACE,{"disambiguationData":[TD([[makeQuery(id+"F0.imprint","IMPRINT",EDGE,{"derivedFrom":sQuery(id+"F0.wireOp",EDGE,"E288")}),-1.0]])]});
            var Q12;
            Q12=makeQuery(id+"F0.imprint","IMPRINT",FACE,{"disambiguationData":[TD([[makeQuery(id+"F0.imprint","IMPRINT",EDGE,{"derivedFrom":sQuery(id+"F0.wireOp",EDGE,"E1224")}),-1.0]])]});
            var Q13;
            Q13=makeQuery(id+"F0.imprint","IMPRINT",FACE,{"disambiguationData":[TD([[makeQuery(id+"F0.imprint","IMPRINT",EDGE,{"derivedFrom":sQuery(id+"F0.wireOp",EDGE,"E1344")}),1.0]])]});
            var Q14;
            Q14=makeQuery(id+"F0.imprint","IMPRINT",FACE,{"disambiguationData":[TD([[makeQuery(id+"F0.imprint","IMPRINT",EDGE,{"derivedFrom":sQuery(id+"F0.wireOp",EDGE,"E2128")}),-1.0]])]});
            var Q15;
            Q15=makeQuery(id+"F0.imprint","IMPRINT",FACE,{"disambiguationData":[TD([[makeQuery(id+"F0.imprint","IMPRINT",EDGE,{"derivedFrom":sQuery(id+"F0.wireOp",EDGE,"E1576")}),1.0]])]});
            var Q16;
            Q16=makeQuery(id+"F0.imprint","IMPRINT",FACE,{"disambiguationData":[TD([[makeQuery(id+"F0.imprint","IMPRINT",EDGE,{"derivedFrom":sQuery(id+"F0.wireOp",EDGE,"E1656")}),1.0]])]});
            extrude(context, id + "F1", {"entities" : qUnion([Q0, Q1, Q2, Q3, Q4, Q5, Q6, Q7, Q8, Q9, Q10, Q11, Q12, Q13, Q14, Q15, Q16]), "depth" : 2.54 * mm, "offsetDistance" : 25.4 * mm});
        }
        {
            var Q0;
            Q0=makeQuery(id+"F0.imprint","IMPRINT",FACE,{"disambiguationData":[TD([[makeQuery(id+"F0.imprint","IMPRINT",EDGE,{"derivedFrom":sQuery(id+"F0.wireOp",EDGE,"E1960")}),1.0]])]});
            var Q1;
            Q1=makeQuery(id+"F0.imprint","IMPRINT",FACE,{"disambiguationData":[TD([[makeQuery(id+"F0.imprint","IMPRINT",EDGE,{"derivedFrom":sQuery(id+"F0.wireOp",EDGE,"E2320")}),-1.0]])]});
            var Q2;
            Q2=makeQuery(id+"F0.imprint","IMPRINT",FACE,{"disambiguationData":[TD([[makeQuery(id+"F0.imprint","IMPRINT",EDGE,{"derivedFrom":sQuery(id+"F0.wireOp",EDGE,"E1408")}),-1.0]])]});
            var Q3;
            Q3=makeQuery(id+"F0.imprint","IMPRINT",FACE,{"disambiguationData":[TD([[makeQuery(id+"F0.imprint","IMPRINT",EDGE,{"derivedFrom":sQuery(id+"F0.wireOp",EDGE,"E1288")}),1.0]])]});
            var Q4;
            Q4=makeQuery(id+"F0.imprint","IMPRINT",FACE,{"disambiguationData":[TD([[makeQuery(id+"F0.imprint","IMPRINT",EDGE,{"derivedFrom":sQuery(id+"F0.wireOp",EDGE,"E1848")}),-1.0]])]});
            var Q5;
            Q5=makeQuery(id+"F0.imprint","IMPRINT",FACE,{"disambiguationData":[TD([[makeQuery(id+"F0.imprint","IMPRINT",EDGE,{"derivedFrom":sQuery(id+"F0.wireOp",EDGE,"E2208")}),1.0]])]});
            var Q6;
            Q6=makeQuery(id+"F0.imprint","IMPRINT",FACE,{"disambiguationData":[TD([[makeQuery(id+"F0.imprint","IMPRINT",EDGE,{"derivedFrom":sQuery(id+"F0.wireOp",EDGE,"E1080")}),1.0]])]});
            var Q7;
            Q7=makeQuery(id+"F0.imprint","IMPRINT",FACE,{"disambiguationData":[TD([[makeQuery(id+"F0.imprint","IMPRINT",EDGE,{"derivedFrom":sQuery(id+"F0.wireOp",EDGE,"E2554")}),1.0]])]});
            var Q8;
            Q8=makeQuery(id+"F0.imprint","IMPRINT",FACE,{"disambiguationData":[TD([[makeQuery(id+"F0.imprint","IMPRINT",EDGE,{"derivedFrom":sQuery(id+"F0.wireOp",EDGE,"E568")}),-1.0]])]});
            var Q9;
            {var subQ25=sQuery(id+"F0.wireOp",EDGE,"E560");Q9=makeQuery(id+"F0.imprint","IMPRINT",FACE,{"disambiguationData":[TD([[makeQuery(id+"F0.imprint","IMPRINT",EDGE,{"derivedFrom":subQ25}),-1.0]])]});}
            var Q10;
            {var subQ4=sQuery(id+"F0.wireOp",EDGE,"E140");Q10=makeQuery(id+"F0.imprint","IMPRINT",FACE,{"disambiguationData":[TD([[makeQuery(id+"F0.imprint","IMPRINT",EDGE,{"derivedFrom":subQ4}),1.0]])]});}
            extrude(context, id + "F2", {"entities" : qUnion([Q0, Q1, Q2, Q3, Q4, Q5, Q6, Q7, Q8, Q9, Q10]), "depth" : 2.54 * mm, "offsetDistance" : 25.4 * mm});
        }
    });
